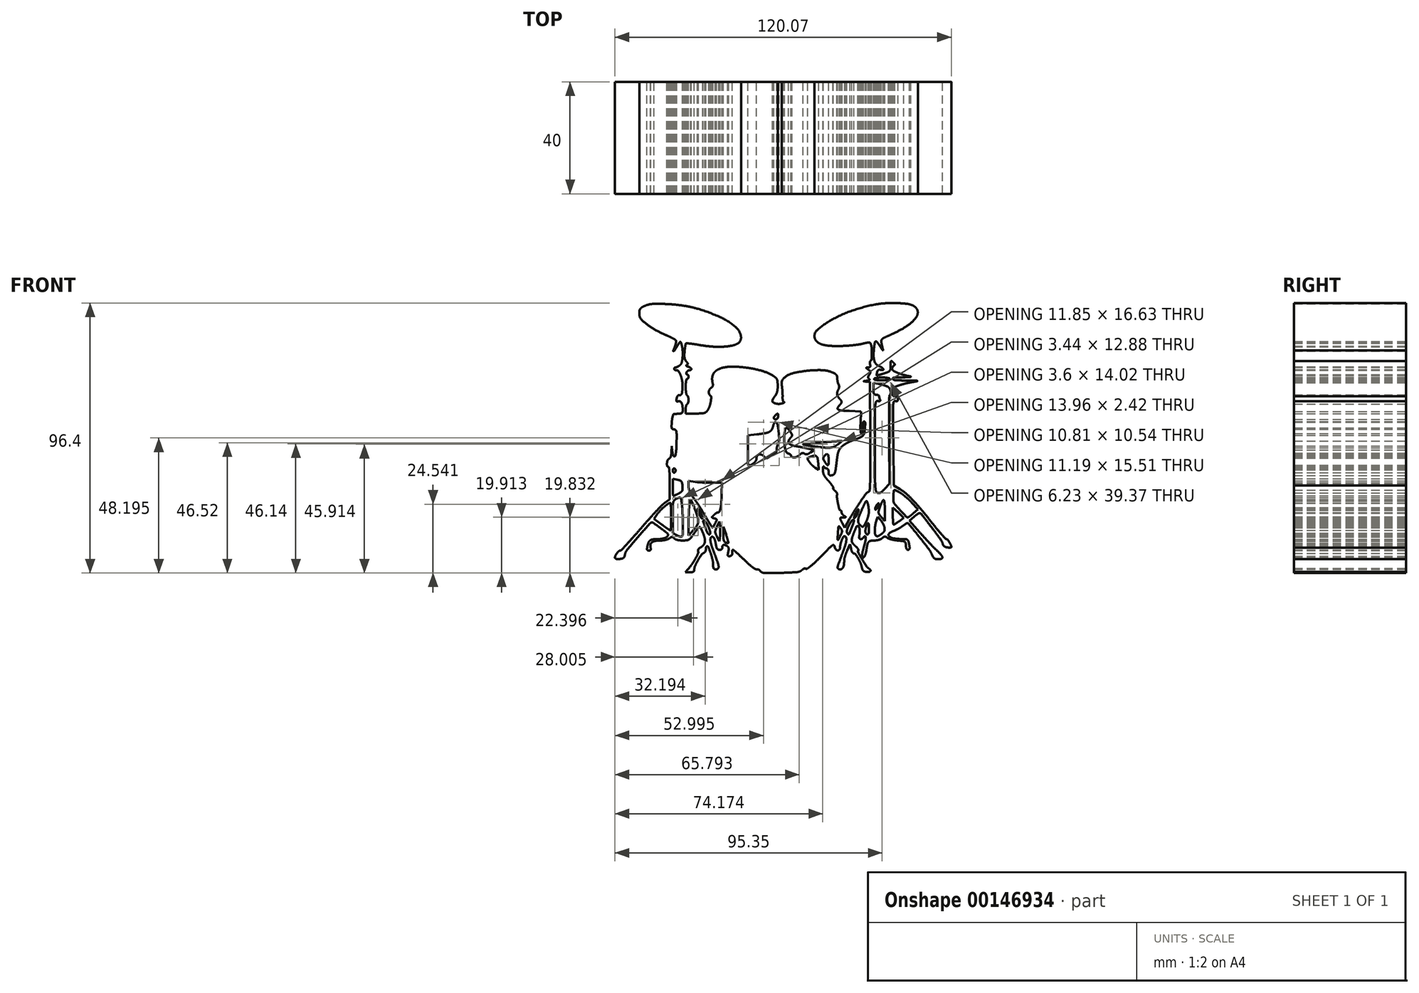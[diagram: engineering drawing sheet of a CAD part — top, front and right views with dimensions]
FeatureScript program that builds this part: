
annotation { "Feature Type Name" : "Feature", "Feature Type Description" : "" }
export const myFeature = defineFeature(function(context is Context, id is Id, definition is map)
    precondition{}
    {
        {
            var Q0;
            Q0=qCreatedBy(makeId("Front.planeOp"),FACE);
            var sketch = newSketch(context, id + "F0", { "sketchPlane" : qUnion([Q0])});
            skArc(sketch, "E0", {"start": v(19.1, 46.98) * mm, "mid": v(14.95, 46.03) * mm, "end": v(10.88, 44.78) * mm});
            skArc(sketch, "E1", {"start": v(10.88, 44.78) * mm, "mid": v(7.16, 43.3) * mm, "end": v(3.58, 41.49) * mm});
            skArc(sketch, "E2", {"start": v(3.58, 41.49) * mm, "mid": v(0.93, 39.82) * mm, "end": v(-1.54, 37.89) * mm});
            skArc(sketch, "E3", {"start": v(-1.54, 37.89) * mm, "mid": v(-2.4, 36.52) * mm, "end": v(-2.38, 34.9) * mm});
            skArc(sketch, "E4", {"start": v(-2.38, 34.9) * mm, "mid": v(-2.03, 34.18) * mm, "end": v(-1.5, 33.6) * mm});
            skArc(sketch, "E5", {"start": v(-1.5, 33.6) * mm, "mid": v(-0.72, 33.08) * mm, "end": v(0.13, 32.72) * mm});
            skArc(sketch, "E6", {"start": v(0.13, 32.72) * mm, "mid": v(1.39, 32.41) * mm, "end": v(2.67, 32.25) * mm});
            skArc(sketch, "E7", {"start": v(2.67, 32.25) * mm, "mid": v(4.53, 32.16) * mm, "end": v(6.4, 32.15) * mm});
            skArc(sketch, "E8", {"start": v(6.4, 32.15) * mm, "mid": v(7.5, 32.17) * mm, "end": v(8.58, 32.22) * mm});
            skArc(sketch, "E9", {"start": v(8.58, 32.22) * mm, "mid": v(9.74, 32.3) * mm, "end": v(10.9, 32.4) * mm});
            skArc(sketch, "E10", {"start": v(10.9, 32.4) * mm, "mid": v(11.95, 32.52) * mm, "end": v(13, 32.65) * mm});
            skArc(sketch, "E11", {"start": v(13, 32.65) * mm, "mid": v(13.74, 32.78) * mm, "end": v(14.47, 32.94) * mm});
            skArc(sketch, "E12", {"start": v(14.47, 32.94) * mm, "mid": v(15.4, 33.16) * mm, "end": v(16.35, 33.37) * mm});
            skArc(sketch, "E13", {"start": v(16.35, 33.37) * mm, "mid": v(16.7, 33.42) * mm, "end": v(17.04, 33.41) * mm});
            skArc(sketch, "E14", {"start": v(17.04, 33.41) * mm, "mid": v(17.25, 33.34) * mm, "end": v(17.42, 33.18) * mm});
            skArc(sketch, "E15", {"start": v(17.42, 33.18) * mm, "mid": v(17.58, 32.89) * mm, "end": v(17.69, 32.57) * mm});
            skArc(sketch, "E16", {"start": v(17.69, 32.57) * mm, "mid": v(17.85, 31.84) * mm, "end": v(17.93, 31.1) * mm});
            skArc(sketch, "E17", {"start": v(17.93, 31.1) * mm, "mid": v(17.98, 30.16) * mm, "end": v(17.97, 29.2) * mm});
            skArc(sketch, "E18", {"start": v(17.97, 29.2) * mm, "mid": v(17.93, 28.31) * mm, "end": v(17.86, 27.42) * mm});
            skArc(sketch, "E19", {"start": v(17.86, 27.42) * mm, "mid": v(17.76, 27.11) * mm, "end": v(17.53, 26.88) * mm});
            skArc(sketch, "E20", {"start": v(17.53, 26.88) * mm, "mid": v(17.43, 26.8) * mm, "end": v(17.37, 26.7) * mm});
            skArc(sketch, "E21", {"start": v(17.37, 26.7) * mm, "mid": v(17.31, 26.54) * mm, "end": v(17.27, 26.38) * mm});
            skArc(sketch, "E22", {"start": v(17.27, 26.38) * mm, "mid": v(17.26, 26.18) * mm, "end": v(17.26, 25.98) * mm});
            skArc(sketch, "E23", {"start": v(17.26, 25.98) * mm, "mid": v(17.28, 25.77) * mm, "end": v(17.33, 25.56) * mm});
            skArc(sketch, "E24", {"start": v(17.33, 25.56) * mm, "mid": v(17.38, 25.32) * mm, "end": v(17.4, 25.08) * mm});
            skArc(sketch, "E25", {"start": v(17.4, 25.08) * mm, "mid": v(17.39, 24.91) * mm, "end": v(17.32, 24.76) * mm});
            skArc(sketch, "E26", {"start": v(17.32, 24.76) * mm, "mid": v(17.21, 24.65) * mm, "end": v(17.07, 24.58) * mm});
            skArc(sketch, "E27", {"start": v(17.07, 24.58) * mm, "mid": v(16.86, 24.54) * mm, "end": v(16.64, 24.52) * mm});
            skArc(sketch, "E28", {"start": v(16.64, 24.52) * mm, "mid": v(16.34, 24.5) * mm, "end": v(16.04, 24.5) * mm});
            skArc(sketch, "E29", {"start": v(16.04, 24.5) * mm, "mid": v(15.98, 24.46) * mm, "end": v(15.96, 24.4) * mm});
            skArc(sketch, "E30", {"start": v(15.96, 24.4) * mm, "mid": v(15.98, 24.3) * mm, "end": v(16.04, 24.23) * mm});
            skArc(sketch, "E31", {"start": v(16.04, 24.23) * mm, "mid": v(16.36, 23.98) * mm, "end": v(16.7, 23.73) * mm});
            skArc(sketch, "E32", {"start": v(16.7, 23.73) * mm, "mid": v(16.97, 23.5) * mm, "end": v(17.22, 23.27) * mm});
            skArc(sketch, "E33", {"start": v(17.22, 23.27) * mm, "mid": v(17.35, 23.1) * mm, "end": v(17.41, 22.9) * mm});
            skArc(sketch, "E34", {"start": v(17.41, 22.9) * mm, "mid": v(17.42, 22.7) * mm, "end": v(17.36, 22.5) * mm});
            skArc(sketch, "E35", {"start": v(17.36, 22.5) * mm, "mid": v(17.2, 22.18) * mm, "end": v(17.03, 21.88) * mm});
            skArc(sketch, "E36", {"start": v(17.03, 21.88) * mm, "mid": v(16.86, 21.59) * mm, "end": v(16.7, 21.3) * mm});
            skArc(sketch, "E37", {"start": v(16.7, 21.3) * mm, "mid": v(16.64, 21.12) * mm, "end": v(16.62, 20.92) * mm});
            skArc(sketch, "E38", {"start": v(16.62, 20.92) * mm, "mid": v(16.64, 20.77) * mm, "end": v(16.71, 20.64) * mm});
            skArc(sketch, "E39", {"start": v(16.71, 20.64) * mm, "mid": v(16.85, 20.5) * mm, "end": v(17, 20.38) * mm});
            skArc(sketch, "E40", {"start": v(17, 20.38) * mm, "mid": v(17.1, 20.3) * mm, "end": v(17.16, 20.2) * mm});
            skArc(sketch, "E41", {"start": v(17.16, 20.2) * mm, "mid": v(17.16, 20.1) * mm, "end": v(17.1, 20.03) * mm});
            skArc(sketch, "E42", {"start": v(17.1, 20.03) * mm, "mid": v(16.96, 19.94) * mm, "end": v(16.79, 19.88) * mm});
            skArc(sketch, "E43", {"start": v(16.79, 19.88) * mm, "mid": v(16.47, 19.81) * mm, "end": v(16.15, 19.76) * mm});
            skArc(sketch, "E44", {"start": v(16.15, 19.76) * mm, "mid": v(15.63, 19.68) * mm, "end": v(15.11, 19.6) * mm});
            skArc(sketch, "E45", {"start": v(15.11, 19.6) * mm, "mid": v(15.07, 19.59) * mm, "end": v(15.04, 19.56) * mm});
            skArc(sketch, "E46", {"start": v(15.04, 19.56) * mm, "mid": v(15.04, 19.53) * mm, "end": v(15.07, 19.51) * mm});
            skArc(sketch, "E47", {"start": v(15.07, 19.51) * mm, "mid": v(15.53, 19.48) * mm, "end": v(16, 19.46) * mm});
            skLineSegment(sketch, "E48", {"start": v(16, 19.46) * mm, "end": v(17.34, 19.38) * mm});
            skLineSegment(sketch, "E49", {"start": v(17.34, 19.38) * mm, "end": v(17.43, -0.14) * mm});
            skArc(sketch, "E50", {"start": v(17.43, -0.14) * mm, "mid": v(17.45, -5.6) * mm, "end": v(17.46, -11.04) * mm});
            skArc(sketch, "E51", {"start": v(17.46, -11.04) * mm, "mid": v(17.44, -13.63) * mm, "end": v(17.37, -16.22) * mm});
            skArc(sketch, "E52", {"start": v(17.37, -16.22) * mm, "mid": v(17.3, -17.8) * mm, "end": v(17.2, -19.36) * mm});
            skArc(sketch, "E53", {"start": v(17.2, -19.36) * mm, "mid": v(17.07, -19.72) * mm, "end": v(16.77, -19.95) * mm});
            skArc(sketch, "E54", {"start": v(16.77, -19.95) * mm, "mid": v(16.29, -20.22) * mm, "end": v(15.9, -20.6) * mm});
            skArc(sketch, "E55", {"start": v(15.9, -20.6) * mm, "mid": v(14.97, -21.86) * mm, "end": v(14.07, -23.13) * mm});
            skArc(sketch, "E56", {"start": v(14.07, -23.13) * mm, "mid": v(13.04, -24.65) * mm, "end": v(12.06, -26.2) * mm});
            skArc(sketch, "E57", {"start": v(12.06, -26.2) * mm, "mid": v(11.07, -27.86) * mm, "end": v(10.11, -29.54) * mm});
            skLineSegment(sketch, "E58", {"start": v(10.11, -29.54) * mm, "end": v(8.3, -32.8) * mm});
            skLineSegment(sketch, "E59", {"start": v(8.3, -32.8) * mm, "end": v(7.47, -31.22) * mm});
            skArc(sketch, "E60", {"start": v(7.47, -31.22) * mm, "mid": v(7.13, -30.54) * mm, "end": v(6.8, -29.86) * mm});
            skArc(sketch, "E61", {"start": v(6.8, -29.86) * mm, "mid": v(6.73, -29.62) * mm, "end": v(6.73, -29.38) * mm});
            skArc(sketch, "E62", {"start": v(6.73, -29.38) * mm, "mid": v(6.81, -29.21) * mm, "end": v(6.98, -29.13) * mm});
            skArc(sketch, "E63", {"start": v(6.98, -29.13) * mm, "mid": v(7.4, -29.07) * mm, "end": v(7.81, -29.05) * mm});
            skArc(sketch, "E64", {"start": v(7.81, -29.05) * mm, "mid": v(8.16, -29.04) * mm, "end": v(8.51, -29.03) * mm});
            skArc(sketch, "E65", {"start": v(8.51, -29.03) * mm, "mid": v(8.58, -29) * mm, "end": v(8.63, -28.95) * mm});
            skArc(sketch, "E66", {"start": v(8.63, -28.95) * mm, "mid": v(8.64, -28.89) * mm, "end": v(8.6, -28.83) * mm});
            skArc(sketch, "E67", {"start": v(8.6, -28.83) * mm, "mid": v(8.34, -28.67) * mm, "end": v(8.07, -28.51) * mm});
            skArc(sketch, "E68", {"start": v(8.07, -28.51) * mm, "mid": v(7.9, -28.4) * mm, "end": v(7.73, -28.25) * mm});
            skArc(sketch, "E69", {"start": v(7.73, -28.25) * mm, "mid": v(7.57, -28.1) * mm, "end": v(7.43, -27.92) * mm});
            skArc(sketch, "E70", {"start": v(7.43, -27.92) * mm, "mid": v(7.32, -27.75) * mm, "end": v(7.23, -27.56) * mm});
            skArc(sketch, "E71", {"start": v(7.23, -27.56) * mm, "mid": v(7.19, -27.4) * mm, "end": v(7.17, -27.24) * mm});
            skArc(sketch, "E72", {"start": v(7.17, -27.24) * mm, "mid": v(7.16, -27.1) * mm, "end": v(7.14, -26.95) * mm});
            skArc(sketch, "E73", {"start": v(7.14, -26.95) * mm, "mid": v(7.1, -26.83) * mm, "end": v(7.03, -26.71) * mm});
            skArc(sketch, "E74", {"start": v(7.03, -26.71) * mm, "mid": v(6.97, -26.62) * mm, "end": v(6.89, -26.55) * mm});
            skArc(sketch, "E75", {"start": v(6.89, -26.55) * mm, "mid": v(6.8, -26.5) * mm, "end": v(6.71, -26.5) * mm});
            skArc(sketch, "E76", {"start": v(6.71, -26.5) * mm, "mid": v(6.48, -26.41) * mm, "end": v(6.34, -26.2) * mm});
            skArc(sketch, "E77", {"start": v(6.34, -26.2) * mm, "mid": v(6.1, -25.18) * mm, "end": v(5.88, -24.16) * mm});
            skArc(sketch, "E78", {"start": v(5.88, -24.16) * mm, "mid": v(5.7, -23.15) * mm, "end": v(5.54, -22.13) * mm});
            skArc(sketch, "E79", {"start": v(5.54, -22.13) * mm, "mid": v(5.5, -21.51) * mm, "end": v(5.57, -20.9) * mm});
            skArc(sketch, "E80", {"start": v(5.57, -20.9) * mm, "mid": v(5.58, -20.75) * mm, "end": v(5.55, -20.6) * mm});
            skArc(sketch, "E81", {"start": v(5.55, -20.6) * mm, "mid": v(5.5, -20.4) * mm, "end": v(5.4, -20.23) * mm});
            skArc(sketch, "E82", {"start": v(5.4, -20.23) * mm, "mid": v(5.3, -20.05) * mm, "end": v(5.16, -19.88) * mm});
            skArc(sketch, "E83", {"start": v(5.16, -19.88) * mm, "mid": v(5.01, -19.73) * mm, "end": v(4.85, -19.6) * mm});
            skArc(sketch, "E84", {"start": v(4.85, -19.6) * mm, "mid": v(4.69, -19.46) * mm, "end": v(4.54, -19.32) * mm});
            skArc(sketch, "E85", {"start": v(4.54, -19.32) * mm, "mid": v(4.4, -19.17) * mm, "end": v(4.3, -19.01) * mm});
            skArc(sketch, "E86", {"start": v(4.3, -19.01) * mm, "mid": v(4.22, -18.87) * mm, "end": v(4.16, -18.72) * mm});
            skArc(sketch, "E87", {"start": v(4.16, -18.72) * mm, "mid": v(4.14, -18.6) * mm, "end": v(4.16, -18.48) * mm});
            skArc(sketch, "E88", {"start": v(4.16, -18.48) * mm, "mid": v(4.17, -18.33) * mm, "end": v(4.12, -18.19) * mm});
            skArc(sketch, "E89", {"start": v(4.12, -18.19) * mm, "mid": v(3.92, -17.85) * mm, "end": v(3.7, -17.53) * mm});
            skArc(sketch, "E90", {"start": v(3.7, -17.53) * mm, "mid": v(3.41, -17.13) * mm, "end": v(3.11, -16.75) * mm});
            skArc(sketch, "E91", {"start": v(3.11, -16.75) * mm, "mid": v(2.76, -16.33) * mm, "end": v(2.4, -15.92) * mm});
            skArc(sketch, "E92", {"start": v(2.4, -15.92) * mm, "mid": v(1.9, -15.38) * mm, "end": v(1.45, -14.82) * mm});
            skArc(sketch, "E93", {"start": v(1.45, -14.82) * mm, "mid": v(1.14, -14.38) * mm, "end": v(0.88, -13.92) * mm});
            skArc(sketch, "E94", {"start": v(0.88, -13.92) * mm, "mid": v(0.7, -13.5) * mm, "end": v(0.6, -13.05) * mm});
            skArc(sketch, "E95", {"start": v(0.6, -13.05) * mm, "mid": v(0.53, -12.56) * mm, "end": v(0.51, -12.06) * mm});
            skArc(sketch, "E96", {"start": v(0.51, -12.06) * mm, "mid": v(0.52, -11.73) * mm, "end": v(0.54, -11.4) * mm});
            skArc(sketch, "E97", {"start": v(0.54, -11.4) * mm, "mid": v(0.57, -11.19) * mm, "end": v(0.62, -10.97) * mm});
            skArc(sketch, "E98", {"start": v(0.62, -10.97) * mm, "mid": v(0.65, -10.9) * mm, "end": v(0.71, -10.86) * mm});
            skArc(sketch, "E99", {"start": v(0.71, -10.86) * mm, "mid": v(0.77, -10.86) * mm, "end": v(0.81, -10.9) * mm});
            skArc(sketch, "E100", {"start": v(0.81, -10.9) * mm, "mid": v(0.88, -11.03) * mm, "end": v(0.96, -11.15) * mm});
            skArc(sketch, "E101", {"start": v(0.96, -11.15) * mm, "mid": v(1.08, -11.26) * mm, "end": v(1.2, -11.35) * mm});
            skArc(sketch, "E102", {"start": v(1.2, -11.35) * mm, "mid": v(1.35, -11.43) * mm, "end": v(1.5, -11.5) * mm});
            skArc(sketch, "E103", {"start": v(1.5, -11.5) * mm, "mid": v(1.65, -11.53) * mm, "end": v(1.8, -11.54) * mm});
            skArc(sketch, "E104", {"start": v(1.8, -11.54) * mm, "mid": v(1.96, -11.57) * mm, "end": v(2.1, -11.64) * mm});
            skArc(sketch, "E105", {"start": v(2.1, -11.64) * mm, "mid": v(2.23, -11.76) * mm, "end": v(2.33, -11.9) * mm});
            skArc(sketch, "E106", {"start": v(2.33, -11.9) * mm, "mid": v(2.42, -12.11) * mm, "end": v(2.48, -12.33) * mm});
            skArc(sketch, "E107", {"start": v(2.48, -12.33) * mm, "mid": v(2.52, -12.6) * mm, "end": v(2.53, -12.87) * mm});
            skArc(sketch, "E108", {"start": v(2.53, -12.87) * mm, "mid": v(2.54, -13.21) * mm, "end": v(2.58, -13.55) * mm});
            skArc(sketch, "E109", {"start": v(2.58, -13.55) * mm, "mid": v(2.64, -13.74) * mm, "end": v(2.76, -13.9) * mm});
            skArc(sketch, "E110", {"start": v(2.76, -13.9) * mm, "mid": v(2.91, -14) * mm, "end": v(3.1, -14.05) * mm});
            skArc(sketch, "E111", {"start": v(3.1, -14.05) * mm, "mid": v(3.4, -14.06) * mm, "end": v(3.7, -14.03) * mm});
            skArc(sketch, "E112", {"start": v(3.7, -14.03) * mm, "mid": v(4.03, -13.93) * mm, "end": v(4.34, -13.75) * mm});
            skArc(sketch, "E113", {"start": v(4.34, -13.75) * mm, "mid": v(4.58, -13.5) * mm, "end": v(4.75, -13.18) * mm});
            skArc(sketch, "E114", {"start": v(4.75, -13.18) * mm, "mid": v(4.92, -12.62) * mm, "end": v(5.03, -12.05) * mm});
            skArc(sketch, "E115", {"start": v(5.03, -12.05) * mm, "mid": v(5.2, -10.75) * mm, "end": v(5.37, -9.44) * mm});
            skArc(sketch, "E116", {"start": v(5.37, -9.44) * mm, "mid": v(5.52, -8.18) * mm, "end": v(5.7, -6.93) * mm});
            skArc(sketch, "E117", {"start": v(5.7, -6.93) * mm, "mid": v(5.84, -6.23) * mm, "end": v(6.04, -5.55) * mm});
            skArc(sketch, "E118", {"start": v(6.04, -5.55) * mm, "mid": v(6.26, -5.05) * mm, "end": v(6.54, -4.58) * mm});
            skArc(sketch, "E119", {"start": v(6.54, -4.58) * mm, "mid": v(6.92, -4.1) * mm, "end": v(7.35, -3.67) * mm});
            skArc(sketch, "E120", {"start": v(7.35, -3.67) * mm, "mid": v(7.7, -3.36) * mm, "end": v(8.1, -3.09) * mm});
            skArc(sketch, "E121", {"start": v(8.1, -3.09) * mm, "mid": v(8.62, -2.76) * mm, "end": v(9.16, -2.46) * mm});
            skArc(sketch, "E122", {"start": v(9.16, -2.46) * mm, "mid": v(9.74, -2.15) * mm, "end": v(10.34, -1.87) * mm});
            skArc(sketch, "E123", {"start": v(10.34, -1.87) * mm, "mid": v(10.9, -1.64) * mm, "end": v(11.46, -1.44) * mm});
            skArc(sketch, "E124", {"start": v(11.46, -1.44) * mm, "mid": v(12, -1.25) * mm, "end": v(12.52, -1.05) * mm});
            skArc(sketch, "E125", {"start": v(12.52, -1.05) * mm, "mid": v(13.02, -0.85) * mm, "end": v(13.52, -0.63) * mm});
            skArc(sketch, "E126", {"start": v(13.52, -0.63) * mm, "mid": v(13.94, -0.42) * mm, "end": v(14.35, -0.21) * mm});
            skArc(sketch, "E127", {"start": v(14.35, -0.21) * mm, "mid": v(14.56, -0.07) * mm, "end": v(14.76, 0.1) * mm});
            skArc(sketch, "E128", {"start": v(14.76, 0.1) * mm, "mid": v(15.08, 0.53) * mm, "end": v(15.27, 1.04) * mm});
            skArc(sketch, "E129", {"start": v(15.27, 1.04) * mm, "mid": v(15.43, 2) * mm, "end": v(15.53, 2.95) * mm});
            skArc(sketch, "E130", {"start": v(15.53, 2.95) * mm, "mid": v(15.58, 3.87) * mm, "end": v(15.58, 4.8) * mm});
            skArc(sketch, "E131", {"start": v(15.58, 4.8) * mm, "mid": v(15.45, 5.09) * mm, "end": v(15.16, 5.2) * mm});
            skArc(sketch, "E132", {"start": v(15.16, 5.2) * mm, "mid": v(15.04, 5.17) * mm, "end": v(14.97, 5.07) * mm});
            skArc(sketch, "E133", {"start": v(14.97, 5.07) * mm, "mid": v(14.89, 4.82) * mm, "end": v(14.83, 4.56) * mm});
            skArc(sketch, "E134", {"start": v(14.83, 4.56) * mm, "mid": v(14.78, 4.21) * mm, "end": v(14.76, 3.86) * mm});
            skArc(sketch, "E135", {"start": v(14.76, 3.86) * mm, "mid": v(14.75, 3.44) * mm, "end": v(14.77, 3.02) * mm});
            skArc(sketch, "E136", {"start": v(14.77, 3.02) * mm, "mid": v(14.78, 2.57) * mm, "end": v(14.78, 2.13) * mm});
            skArc(sketch, "E137", {"start": v(14.78, 2.13) * mm, "mid": v(14.76, 1.78) * mm, "end": v(14.7, 1.43) * mm});
            skArc(sketch, "E138", {"start": v(14.7, 1.43) * mm, "mid": v(14.64, 1.2) * mm, "end": v(14.55, 0.97) * mm});
            skArc(sketch, "E139", {"start": v(14.55, 0.97) * mm, "mid": v(14.47, 0.86) * mm, "end": v(14.34, 0.83) * mm});
            skArc(sketch, "E140", {"start": v(14.34, 0.83) * mm, "mid": v(14.18, 0.88) * mm, "end": v(14.1, 1.02) * mm});
            skArc(sketch, "E141", {"start": v(14.1, 1.02) * mm, "mid": v(14.02, 1.43) * mm, "end": v(13.96, 1.84) * mm});
            skArc(sketch, "E142", {"start": v(13.96, 1.84) * mm, "mid": v(13.92, 2.46) * mm, "end": v(13.9, 3.07) * mm});
            skArc(sketch, "E143", {"start": v(13.9, 3.07) * mm, "mid": v(13.92, 3.95) * mm, "end": v(13.95, 4.82) * mm});
            skLineSegment(sketch, "E144", {"start": v(13.95, 4.82) * mm, "end": v(14.11, 8.81) * mm});
            skLineSegment(sketch, "E145", {"start": v(14.11, 8.81) * mm, "end": v(9.87, 8.96) * mm});
            skArc(sketch, "E146", {"start": v(9.87, 8.96) * mm, "mid": v(8.47, 9.03) * mm, "end": v(7.08, 9.12) * mm});
            skArc(sketch, "E147", {"start": v(7.08, 9.12) * mm, "mid": v(6.5, 9.23) * mm, "end": v(5.97, 9.46) * mm});
            skArc(sketch, "E148", {"start": v(5.97, 9.46) * mm, "mid": v(5.76, 9.72) * mm, "end": v(5.78, 10.04) * mm});
            skArc(sketch, "E149", {"start": v(5.78, 10.04) * mm, "mid": v(6.04, 10.53) * mm, "end": v(6.4, 10.95) * mm});
            skArc(sketch, "E150", {"start": v(6.4, 10.95) * mm, "mid": v(6.69, 11.27) * mm, "end": v(6.95, 11.62) * mm});
            skArc(sketch, "E151", {"start": v(6.95, 11.62) * mm, "mid": v(7.08, 11.87) * mm, "end": v(7.13, 12.16) * mm});
            skArc(sketch, "E152", {"start": v(7.13, 12.16) * mm, "mid": v(7.09, 12.44) * mm, "end": v(6.97, 12.7) * mm});
            skArc(sketch, "E153", {"start": v(6.97, 12.7) * mm, "mid": v(6.72, 13.03) * mm, "end": v(6.44, 13.34) * mm});
            skArc(sketch, "E154", {"start": v(6.44, 13.34) * mm, "mid": v(6.12, 13.7) * mm, "end": v(5.85, 14.1) * mm});
            skArc(sketch, "E155", {"start": v(5.85, 14.1) * mm, "mid": v(5.67, 14.47) * mm, "end": v(5.58, 14.86) * mm});
            skArc(sketch, "E156", {"start": v(5.58, 14.86) * mm, "mid": v(5.56, 15.27) * mm, "end": v(5.63, 15.68) * mm});
            skArc(sketch, "E157", {"start": v(5.63, 15.68) * mm, "mid": v(5.78, 16.14) * mm, "end": v(6, 16.57) * mm});
            skArc(sketch, "E158", {"start": v(6, 16.57) * mm, "mid": v(6.11, 16.81) * mm, "end": v(6.2, 17.07) * mm});
            skArc(sketch, "E159", {"start": v(6.2, 17.07) * mm, "mid": v(6.27, 17.3) * mm, "end": v(6.3, 17.55) * mm});
            skArc(sketch, "E160", {"start": v(6.3, 17.55) * mm, "mid": v(6.3, 17.77) * mm, "end": v(6.27, 18) * mm});
            skArc(sketch, "E161", {"start": v(6.27, 18) * mm, "mid": v(6.2, 18.2) * mm, "end": v(6.11, 18.38) * mm});
            skArc(sketch, "E162", {"start": v(6.11, 18.38) * mm, "mid": v(6, 18.56) * mm, "end": v(5.93, 18.76) * mm});
            skArc(sketch, "E163", {"start": v(5.93, 18.76) * mm, "mid": v(5.84, 19.04) * mm, "end": v(5.77, 19.33) * mm});
            skArc(sketch, "E164", {"start": v(5.77, 19.33) * mm, "mid": v(5.71, 19.64) * mm, "end": v(5.67, 19.96) * mm});
            skArc(sketch, "E165", {"start": v(5.67, 19.96) * mm, "mid": v(5.64, 20.26) * mm, "end": v(5.63, 20.57) * mm});
            skArc(sketch, "E166", {"start": v(5.63, 20.57) * mm, "mid": v(5.6, 20.95) * mm, "end": v(5.54, 21.33) * mm});
            skArc(sketch, "E167", {"start": v(5.54, 21.33) * mm, "mid": v(5.43, 21.61) * mm, "end": v(5.27, 21.87) * mm});
            skArc(sketch, "E168", {"start": v(5.27, 21.87) * mm, "mid": v(5.03, 22.11) * mm, "end": v(4.75, 22.31) * mm});
            skArc(sketch, "E169", {"start": v(4.75, 22.31) * mm, "mid": v(4.3, 22.55) * mm, "end": v(3.84, 22.76) * mm});
            skArc(sketch, "E170", {"start": v(3.84, 22.76) * mm, "mid": v(2.03, 23.32) * mm, "end": v(0.14, 23.54) * mm});
            skArc(sketch, "E171", {"start": v(0.14, 23.54) * mm, "mid": v(-2.56, 23.51) * mm, "end": v(-5.25, 23.3) * mm});
            skArc(sketch, "E172", {"start": v(-5.25, 23.3) * mm, "mid": v(-7.87, 22.93) * mm, "end": v(-10.45, 22.38) * mm});
            skArc(sketch, "E173", {"start": v(-10.45, 22.38) * mm, "mid": v(-11.96, 21.8) * mm, "end": v(-13.27, 20.85) * mm});
            skArc(sketch, "E174", {"start": v(-13.27, 20.85) * mm, "mid": v(-13.57, 20.54) * mm, "end": v(-13.83, 20.2) * mm});
            skArc(sketch, "E175", {"start": v(-13.83, 20.2) * mm, "mid": v(-14, 19.9) * mm, "end": v(-14.13, 19.58) * mm});
            skArc(sketch, "E176", {"start": v(-14.13, 19.58) * mm, "mid": v(-14.2, 19.2) * mm, "end": v(-14.21, 18.8) * mm});
            skArc(sketch, "E177", {"start": v(-14.21, 18.8) * mm, "mid": v(-14.18, 18.23) * mm, "end": v(-14.12, 17.65) * mm});
            skArc(sketch, "E178", {"start": v(-14.12, 17.65) * mm, "mid": v(-14.06, 17.18) * mm, "end": v(-14.01, 16.71) * mm});
            skArc(sketch, "E179", {"start": v(-14.01, 16.71) * mm, "mid": v(-13.97, 16.18) * mm, "end": v(-13.94, 15.65) * mm});
            skArc(sketch, "E180", {"start": v(-13.94, 15.65) * mm, "mid": v(-13.91, 15.14) * mm, "end": v(-13.9, 14.63) * mm});
            skArc(sketch, "E181", {"start": v(-13.9, 14.63) * mm, "mid": v(-13.89, 14.24) * mm, "end": v(-13.9, 13.84) * mm});
            skArc(sketch, "E182", {"start": v(-13.9, 13.84) * mm, "mid": v(-13.9, 13.5) * mm, "end": v(-13.88, 13.15) * mm});
            skArc(sketch, "E183", {"start": v(-13.88, 13.15) * mm, "mid": v(-13.84, 12.88) * mm, "end": v(-13.77, 12.61) * mm});
            skArc(sketch, "E184", {"start": v(-13.77, 12.61) * mm, "mid": v(-13.69, 12.43) * mm, "end": v(-13.58, 12.26) * mm});
            skArc(sketch, "E185", {"start": v(-13.58, 12.26) * mm, "mid": v(-13.46, 12.16) * mm, "end": v(-13.32, 12.12) * mm});
            skArc(sketch, "E186", {"start": v(-13.32, 12.12) * mm, "mid": v(-13.27, 12.1) * mm, "end": v(-13.25, 12.05) * mm});
            skArc(sketch, "E187", {"start": v(-13.25, 12.05) * mm, "mid": v(-13.26, 12) * mm, "end": v(-13.3, 11.96) * mm});
            skArc(sketch, "E188", {"start": v(-13.3, 11.96) * mm, "mid": v(-13.46, 11.87) * mm, "end": v(-13.63, 11.8) * mm});
            skArc(sketch, "E189", {"start": v(-13.63, 11.8) * mm, "mid": v(-13.9, 11.71) * mm, "end": v(-14.17, 11.63) * mm});
            skArc(sketch, "E190", {"start": v(-14.17, 11.63) * mm, "mid": v(-14.72, 11.5) * mm, "end": v(-15.3, 11.47) * mm});
            skArc(sketch, "E191", {"start": v(-15.3, 11.47) * mm, "mid": v(-15.86, 11.5) * mm, "end": v(-16.43, 11.63) * mm});
            skArc(sketch, "E192", {"start": v(-16.43, 11.63) * mm, "mid": v(-16.87, 11.8) * mm, "end": v(-17.28, 12.05) * mm});
            skArc(sketch, "E193", {"start": v(-17.28, 12.05) * mm, "mid": v(-17.5, 12.3) * mm, "end": v(-17.57, 12.63) * mm});
            skArc(sketch, "E194", {"start": v(-17.57, 12.63) * mm, "mid": v(-17.56, 12.75) * mm, "end": v(-17.51, 12.87) * mm});
            skArc(sketch, "E195", {"start": v(-17.51, 12.87) * mm, "mid": v(-17.4, 13.08) * mm, "end": v(-17.28, 13.3) * mm});
            skArc(sketch, "E196", {"start": v(-17.28, 13.3) * mm, "mid": v(-17.13, 13.55) * mm, "end": v(-16.96, 13.8) * mm});
            skArc(sketch, "E197", {"start": v(-16.96, 13.8) * mm, "mid": v(-16.78, 14.06) * mm, "end": v(-16.58, 14.3) * mm});
            skArc(sketch, "E198", {"start": v(-16.58, 14.3) * mm, "mid": v(-16.34, 14.65) * mm, "end": v(-16.15, 15.02) * mm});
            skArc(sketch, "E199", {"start": v(-16.15, 15.02) * mm, "mid": v(-15.98, 15.43) * mm, "end": v(-15.85, 15.86) * mm});
            skArc(sketch, "E200", {"start": v(-15.85, 15.86) * mm, "mid": v(-15.74, 16.35) * mm, "end": v(-15.68, 16.86) * mm});
            skArc(sketch, "E201", {"start": v(-15.68, 16.86) * mm, "mid": v(-15.64, 17.45) * mm, "end": v(-15.64, 18.04) * mm});
            skArc(sketch, "E202", {"start": v(-15.64, 18.04) * mm, "mid": v(-15.66, 18.76) * mm, "end": v(-15.71, 19.47) * mm});
            skArc(sketch, "E203", {"start": v(-15.71, 19.47) * mm, "mid": v(-15.79, 19.88) * mm, "end": v(-15.93, 20.27) * mm});
            skArc(sketch, "E204", {"start": v(-15.93, 20.27) * mm, "mid": v(-16.13, 20.6) * mm, "end": v(-16.4, 20.87) * mm});
            skArc(sketch, "E205", {"start": v(-16.4, 20.87) * mm, "mid": v(-16.82, 21.2) * mm, "end": v(-17.27, 21.5) * mm});
            skArc(sketch, "E206", {"start": v(-17.27, 21.5) * mm, "mid": v(-19.31, 22.58) * mm, "end": v(-21.5, 23.35) * mm});
            skArc(sketch, "E207", {"start": v(-21.5, 23.35) * mm, "mid": v(-24.3, 24.01) * mm, "end": v(-27.16, 24.47) * mm});
            skArc(sketch, "E208", {"start": v(-27.16, 24.47) * mm, "mid": v(-29.96, 24.71) * mm, "end": v(-32.77, 24.75) * mm});
            skArc(sketch, "E209", {"start": v(-32.77, 24.75) * mm, "mid": v(-34.77, 24.5) * mm, "end": v(-36.7, 23.9) * mm});
            skArc(sketch, "E210", {"start": v(-36.7, 23.9) * mm, "mid": v(-37.35, 23.55) * mm, "end": v(-37.94, 23.09) * mm});
            skArc(sketch, "E211", {"start": v(-37.94, 23.09) * mm, "mid": v(-38.4, 22.56) * mm, "end": v(-38.74, 21.94) * mm});
            skArc(sketch, "E212", {"start": v(-38.74, 21.94) * mm, "mid": v(-38.97, 21.25) * mm, "end": v(-39.05, 20.52) * mm});
            skArc(sketch, "E213", {"start": v(-39.05, 20.52) * mm, "mid": v(-39, 19.69) * mm, "end": v(-38.85, 18.88) * mm});
            skArc(sketch, "E214", {"start": v(-38.85, 18.88) * mm, "mid": v(-38.8, 18.6) * mm, "end": v(-38.77, 18.33) * mm});
            skArc(sketch, "E215", {"start": v(-38.77, 18.33) * mm, "mid": v(-38.78, 18.1) * mm, "end": v(-38.83, 17.88) * mm});
            skArc(sketch, "E216", {"start": v(-38.83, 17.88) * mm, "mid": v(-38.92, 17.68) * mm, "end": v(-39.04, 17.51) * mm});
            skArc(sketch, "E217", {"start": v(-39.04, 17.51) * mm, "mid": v(-39.2, 17.35) * mm, "end": v(-39.4, 17.23) * mm});
            skArc(sketch, "E218", {"start": v(-39.4, 17.23) * mm, "mid": v(-39.71, 16.99) * mm, "end": v(-39.95, 16.68) * mm});
            skArc(sketch, "E219", {"start": v(-39.95, 16.68) * mm, "mid": v(-40.13, 16.27) * mm, "end": v(-40.22, 15.84) * mm});
            skArc(sketch, "E220", {"start": v(-40.22, 15.84) * mm, "mid": v(-40.22, 15.43) * mm, "end": v(-40.14, 15.02) * mm});
            skArc(sketch, "E221", {"start": v(-40.14, 15.02) * mm, "mid": v(-39.98, 14.7) * mm, "end": v(-39.72, 14.47) * mm});
            skArc(sketch, "E222", {"start": v(-39.72, 14.47) * mm, "mid": v(-39.46, 14.2) * mm, "end": v(-39.38, 13.85) * mm});
            skArc(sketch, "E223", {"start": v(-39.38, 13.85) * mm, "mid": v(-39.44, 13.05) * mm, "end": v(-39.55, 12.27) * mm});
            skArc(sketch, "E224", {"start": v(-39.55, 12.27) * mm, "mid": v(-39.73, 11.4) * mm, "end": v(-39.98, 10.55) * mm});
            skArc(sketch, "E225", {"start": v(-39.98, 10.55) * mm, "mid": v(-40.27, 9.86) * mm, "end": v(-40.64, 9.2) * mm});
            skArc(sketch, "E226", {"start": v(-40.64, 9.2) * mm, "mid": v(-40.9, 8.87) * mm, "end": v(-41.2, 8.58) * mm});
            skArc(sketch, "E227", {"start": v(-41.2, 8.58) * mm, "mid": v(-41.52, 8.38) * mm, "end": v(-41.88, 8.24) * mm});
            skArc(sketch, "E228", {"start": v(-41.88, 8.24) * mm, "mid": v(-42.4, 8.13) * mm, "end": v(-42.92, 8.08) * mm});
            skArc(sketch, "E229", {"start": v(-42.92, 8.08) * mm, "mid": v(-43.94, 8.05) * mm, "end": v(-44.95, 8.04) * mm});
            skLineSegment(sketch, "E230", {"start": v(-44.95, 8.04) * mm, "end": v(-48.5, 8.04) * mm});
            skLineSegment(sketch, "E231", {"start": v(-48.5, 8.04) * mm, "end": v(-48.5, 9.56) * mm});
            skArc(sketch, "E232", {"start": v(-48.5, 9.56) * mm, "mid": v(-48.48, 9.86) * mm, "end": v(-48.46, 10.16) * mm});
            skArc(sketch, "E233", {"start": v(-48.46, 10.16) * mm, "mid": v(-48.41, 10.44) * mm, "end": v(-48.34, 10.72) * mm});
            skArc(sketch, "E234", {"start": v(-48.34, 10.72) * mm, "mid": v(-48.27, 10.95) * mm, "end": v(-48.18, 11.17) * mm});
            skArc(sketch, "E235", {"start": v(-48.18, 11.17) * mm, "mid": v(-48.1, 11.3) * mm, "end": v(-47.98, 11.4) * mm});
            skArc(sketch, "E236", {"start": v(-47.98, 11.4) * mm, "mid": v(-47.87, 11.48) * mm, "end": v(-47.78, 11.6) * mm});
            skArc(sketch, "E237", {"start": v(-47.78, 11.6) * mm, "mid": v(-47.69, 11.78) * mm, "end": v(-47.61, 11.98) * mm});
            skArc(sketch, "E238", {"start": v(-47.61, 11.98) * mm, "mid": v(-47.55, 12.2) * mm, "end": v(-47.5, 12.44) * mm});
            skArc(sketch, "E239", {"start": v(-47.5, 12.44) * mm, "mid": v(-47.47, 12.7) * mm, "end": v(-47.46, 12.94) * mm});
            skArc(sketch, "E240", {"start": v(-47.46, 12.94) * mm, "mid": v(-47.47, 13.18) * mm, "end": v(-47.5, 13.43) * mm});
            skArc(sketch, "E241", {"start": v(-47.5, 13.43) * mm, "mid": v(-47.55, 13.67) * mm, "end": v(-47.61, 13.9) * mm});
            skArc(sketch, "E242", {"start": v(-47.61, 13.9) * mm, "mid": v(-47.69, 14.1) * mm, "end": v(-47.78, 14.28) * mm});
            skArc(sketch, "E243", {"start": v(-47.78, 14.28) * mm, "mid": v(-47.87, 14.4) * mm, "end": v(-47.98, 14.48) * mm});
            skArc(sketch, "E244", {"start": v(-47.98, 14.48) * mm, "mid": v(-48.1, 14.6) * mm, "end": v(-48.18, 14.76) * mm});
            skArc(sketch, "E245", {"start": v(-48.18, 14.76) * mm, "mid": v(-48.27, 15.14) * mm, "end": v(-48.34, 15.53) * mm});
            skArc(sketch, "E246", {"start": v(-48.34, 15.53) * mm, "mid": v(-48.41, 16.02) * mm, "end": v(-48.46, 16.5) * mm});
            skArc(sketch, "E247", {"start": v(-48.46, 16.5) * mm, "mid": v(-48.49, 17.06) * mm, "end": v(-48.5, 17.6) * mm});
            skArc(sketch, "E248", {"start": v(-48.5, 17.6) * mm, "mid": v(-48.49, 18.14) * mm, "end": v(-48.46, 18.68) * mm});
            skArc(sketch, "E249", {"start": v(-48.46, 18.68) * mm, "mid": v(-48.41, 19.14) * mm, "end": v(-48.34, 19.59) * mm});
            skArc(sketch, "E250", {"start": v(-48.34, 19.59) * mm, "mid": v(-48.27, 19.93) * mm, "end": v(-48.18, 20.26) * mm});
            skArc(sketch, "E251", {"start": v(-48.18, 20.26) * mm, "mid": v(-48.1, 20.37) * mm, "end": v(-47.98, 20.41) * mm});
            skArc(sketch, "E252", {"start": v(-47.98, 20.41) * mm, "mid": v(-47.88, 20.43) * mm, "end": v(-47.78, 20.47) * mm});
            skArc(sketch, "E253", {"start": v(-47.78, 20.47) * mm, "mid": v(-47.7, 20.55) * mm, "end": v(-47.61, 20.64) * mm});
            skArc(sketch, "E254", {"start": v(-47.61, 20.64) * mm, "mid": v(-47.55, 20.76) * mm, "end": v(-47.5, 20.89) * mm});
            skArc(sketch, "E255", {"start": v(-47.5, 20.89) * mm, "mid": v(-47.47, 21.03) * mm, "end": v(-47.46, 21.18) * mm});
            skArc(sketch, "E256", {"start": v(-47.46, 21.18) * mm, "mid": v(-47.47, 21.33) * mm, "end": v(-47.5, 21.48) * mm});
            skArc(sketch, "E257", {"start": v(-47.5, 21.48) * mm, "mid": v(-47.55, 21.6) * mm, "end": v(-47.61, 21.73) * mm});
            skArc(sketch, "E258", {"start": v(-47.61, 21.73) * mm, "mid": v(-47.68, 21.82) * mm, "end": v(-47.77, 21.9) * mm});
            skArc(sketch, "E259", {"start": v(-47.77, 21.9) * mm, "mid": v(-47.86, 21.94) * mm, "end": v(-47.96, 21.96) * mm});
            skArc(sketch, "E260", {"start": v(-47.96, 21.96) * mm, "mid": v(-48.05, 21.97) * mm, "end": v(-48.13, 22.02) * mm});
            skArc(sketch, "E261", {"start": v(-48.13, 22.02) * mm, "mid": v(-48.2, 22.1) * mm, "end": v(-48.23, 22.18) * mm});
            skArc(sketch, "E262", {"start": v(-48.23, 22.18) * mm, "mid": v(-48.25, 22.3) * mm, "end": v(-48.24, 22.43) * mm});
            skArc(sketch, "E263", {"start": v(-48.24, 22.43) * mm, "mid": v(-48.21, 22.58) * mm, "end": v(-48.17, 22.73) * mm});
            skArc(sketch, "E264", {"start": v(-48.17, 22.73) * mm, "mid": v(-48.1, 22.88) * mm, "end": v(-48, 23.03) * mm});
            skArc(sketch, "E265", {"start": v(-48, 23.03) * mm, "mid": v(-47.88, 23.16) * mm, "end": v(-47.74, 23.28) * mm});
            skArc(sketch, "E266", {"start": v(-47.74, 23.28) * mm, "mid": v(-47.6, 23.37) * mm, "end": v(-47.45, 23.45) * mm});
            skArc(sketch, "E267", {"start": v(-47.45, 23.45) * mm, "mid": v(-47.3, 23.49) * mm, "end": v(-47.15, 23.5) * mm});
            skArc(sketch, "E268", {"start": v(-47.15, 23.5) * mm, "mid": v(-46.86, 23.54) * mm, "end": v(-46.6, 23.65) * mm});
            skArc(sketch, "E269", {"start": v(-46.6, 23.65) * mm, "mid": v(-46.47, 23.8) * mm, "end": v(-46.47, 23.99) * mm});
            skArc(sketch, "E270", {"start": v(-46.47, 23.99) * mm, "mid": v(-46.6, 24.24) * mm, "end": v(-46.83, 24.43) * mm});
            skArc(sketch, "E271", {"start": v(-46.83, 24.43) * mm, "mid": v(-47.2, 24.62) * mm, "end": v(-47.6, 24.77) * mm});
            skArc(sketch, "E272", {"start": v(-47.6, 24.77) * mm, "mid": v(-47.83, 24.85) * mm, "end": v(-48.07, 24.94) * mm});
            skArc(sketch, "E273", {"start": v(-48.07, 24.94) * mm, "mid": v(-48.19, 25) * mm, "end": v(-48.28, 25.1) * mm});
            skArc(sketch, "E274", {"start": v(-48.28, 25.1) * mm, "mid": v(-48.3, 25.18) * mm, "end": v(-48.28, 25.25) * mm});
            skArc(sketch, "E275", {"start": v(-48.28, 25.25) * mm, "mid": v(-48.18, 25.34) * mm, "end": v(-48.08, 25.4) * mm});
            skArc(sketch, "E276", {"start": v(-48.08, 25.4) * mm, "mid": v(-47.93, 25.47) * mm, "end": v(-47.8, 25.58) * mm});
            skArc(sketch, "E277", {"start": v(-47.8, 25.58) * mm, "mid": v(-47.73, 25.69) * mm, "end": v(-47.72, 25.81) * mm});
            skArc(sketch, "E278", {"start": v(-47.72, 25.81) * mm, "mid": v(-47.77, 25.98) * mm, "end": v(-47.86, 26.13) * mm});
            skArc(sketch, "E279", {"start": v(-47.86, 26.13) * mm, "mid": v(-48.06, 26.39) * mm, "end": v(-48.27, 26.63) * mm});
            skArc(sketch, "E280", {"start": v(-48.27, 26.63) * mm, "mid": v(-48.5, 26.92) * mm, "end": v(-48.68, 27.24) * mm});
            skArc(sketch, "E281", {"start": v(-48.68, 27.24) * mm, "mid": v(-48.81, 27.59) * mm, "end": v(-48.9, 27.95) * mm});
            skArc(sketch, "E282", {"start": v(-48.9, 27.95) * mm, "mid": v(-48.96, 28.42) * mm, "end": v(-48.97, 28.88) * mm});
            skArc(sketch, "E283", {"start": v(-48.97, 28.88) * mm, "mid": v(-48.94, 29.54) * mm, "end": v(-48.9, 30.2) * mm});
            skArc(sketch, "E284", {"start": v(-48.9, 30.2) * mm, "mid": v(-48.84, 30.7) * mm, "end": v(-48.78, 31.22) * mm});
            skArc(sketch, "E285", {"start": v(-48.78, 31.22) * mm, "mid": v(-48.72, 31.67) * mm, "end": v(-48.64, 32.11) * mm});
            skArc(sketch, "E286", {"start": v(-48.64, 32.11) * mm, "mid": v(-48.57, 32.49) * mm, "end": v(-48.5, 32.85) * mm});
            skArc(sketch, "E287", {"start": v(-48.5, 32.85) * mm, "mid": v(-48.46, 32.97) * mm, "end": v(-48.38, 33.06) * mm});
            skArc(sketch, "E288", {"start": v(-48.38, 33.06) * mm, "mid": v(-48.28, 33.13) * mm, "end": v(-48.15, 33.14) * mm});
            skArc(sketch, "E289", {"start": v(-48.15, 33.14) * mm, "mid": v(-47.47, 33.07) * mm, "end": v(-46.78, 33) * mm});
            skArc(sketch, "E290", {"start": v(-46.78, 33) * mm, "mid": v(-45.97, 32.9) * mm, "end": v(-45.16, 32.78) * mm});
            skArc(sketch, "E291", {"start": v(-45.16, 32.78) * mm, "mid": v(-44.22, 32.64) * mm, "end": v(-43.28, 32.48) * mm});
            skArc(sketch, "E292", {"start": v(-43.28, 32.48) * mm, "mid": v(-41.28, 32.18) * mm, "end": v(-39.25, 31.97) * mm});
            skArc(sketch, "E293", {"start": v(-39.25, 31.97) * mm, "mid": v(-37.38, 31.88) * mm, "end": v(-35.5, 31.9) * mm});
            skArc(sketch, "E294", {"start": v(-35.5, 31.9) * mm, "mid": v(-33.9, 32) * mm, "end": v(-32.32, 32.22) * mm});
            skArc(sketch, "E295", {"start": v(-32.32, 32.22) * mm, "mid": v(-31.16, 32.5) * mm, "end": v(-30.06, 32.97) * mm});
            skArc(sketch, "E296", {"start": v(-30.06, 32.97) * mm, "mid": v(-29, 34.05) * mm, "end": v(-28.76, 35.55) * mm});
            skArc(sketch, "E297", {"start": v(-28.76, 35.55) * mm, "mid": v(-29.37, 37.35) * mm, "end": v(-30.55, 38.83) * mm});
            skArc(sketch, "E298", {"start": v(-30.55, 38.83) * mm, "mid": v(-33.18, 40.83) * mm, "end": v(-36.08, 42.42) * mm});
            skArc(sketch, "E299", {"start": v(-36.08, 42.42) * mm, "mid": v(-40.04, 44.06) * mm, "end": v(-44.11, 45.43) * mm});
            skArc(sketch, "E300", {"start": v(-44.11, 45.43) * mm, "mid": v(-46.54, 46.06) * mm, "end": v(-49.01, 46.52) * mm});
            skArc(sketch, "E301", {"start": v(-49.01, 46.52) * mm, "mid": v(-51.85, 46.89) * mm, "end": v(-54.71, 47.12) * mm});
            skArc(sketch, "E302", {"start": v(-54.71, 47.12) * mm, "mid": v(-57.34, 47.21) * mm, "end": v(-59.98, 47.2) * mm});
            skArc(sketch, "E303", {"start": v(-59.98, 47.2) * mm, "mid": v(-61.55, 47) * mm, "end": v(-63.05, 46.53) * mm});
            skArc(sketch, "E304", {"start": v(-63.05, 46.53) * mm, "mid": v(-63.64, 46.25) * mm, "end": v(-64.2, 45.93) * mm});
            skArc(sketch, "E305", {"start": v(-64.2, 45.93) * mm, "mid": v(-64.55, 45.63) * mm, "end": v(-64.82, 45.26) * mm});
            skArc(sketch, "E306", {"start": v(-64.82, 45.26) * mm, "mid": v(-65, 44.84) * mm, "end": v(-65.07, 44.39) * mm});
            skArc(sketch, "E307", {"start": v(-65.07, 44.39) * mm, "mid": v(-65.06, 43.74) * mm, "end": v(-65, 43.09) * mm});
            skArc(sketch, "E308", {"start": v(-65, 43.09) * mm, "mid": v(-64.74, 42.27) * mm, "end": v(-64.24, 41.57) * mm});
            skArc(sketch, "E309", {"start": v(-64.24, 41.57) * mm, "mid": v(-63.13, 40.56) * mm, "end": v(-61.96, 39.64) * mm});
            skArc(sketch, "E310", {"start": v(-61.96, 39.64) * mm, "mid": v(-60.44, 38.6) * mm, "end": v(-58.84, 37.66) * mm});
            skArc(sketch, "E311", {"start": v(-58.84, 37.66) * mm, "mid": v(-57.04, 36.73) * mm, "end": v(-55.2, 35.9) * mm});
            skArc(sketch, "E312", {"start": v(-55.2, 35.9) * mm, "mid": v(-54.64, 35.66) * mm, "end": v(-54.08, 35.4) * mm});
            skArc(sketch, "E313", {"start": v(-54.08, 35.4) * mm, "mid": v(-53.58, 35.16) * mm, "end": v(-53.09, 34.9) * mm});
            skArc(sketch, "E314", {"start": v(-53.09, 34.9) * mm, "mid": v(-52.69, 34.67) * mm, "end": v(-52.3, 34.44) * mm});
            skArc(sketch, "E315", {"start": v(-52.3, 34.44) * mm, "mid": v(-52.13, 34.31) * mm, "end": v(-52, 34.16) * mm});
            skArc(sketch, "E316", {"start": v(-52, 34.16) * mm, "mid": v(-51.94, 34) * mm, "end": v(-51.92, 33.84) * mm});
            skArc(sketch, "E317", {"start": v(-51.92, 33.84) * mm, "mid": v(-51.93, 33.55) * mm, "end": v(-51.97, 33.27) * mm});
            skArc(sketch, "E318", {"start": v(-51.97, 33.27) * mm, "mid": v(-52.04, 32.93) * mm, "end": v(-52.12, 32.6) * mm});
            skArc(sketch, "E319", {"start": v(-52.12, 32.6) * mm, "mid": v(-52.24, 32.25) * mm, "end": v(-52.37, 31.9) * mm});
            skArc(sketch, "E320", {"start": v(-52.37, 31.9) * mm, "mid": v(-52.67, 31.17) * mm, "end": v(-52.97, 30.42) * mm});
            skArc(sketch, "E321", {"start": v(-52.97, 30.42) * mm, "mid": v(-52.95, 30.32) * mm, "end": v(-52.84, 30.28) * mm});
            skArc(sketch, "E322", {"start": v(-52.84, 30.28) * mm, "mid": v(-52.67, 30.37) * mm, "end": v(-52.53, 30.5) * mm});
            skArc(sketch, "E323", {"start": v(-52.53, 30.5) * mm, "mid": v(-52.02, 31.31) * mm, "end": v(-51.52, 32.12) * mm});
            skArc(sketch, "E324", {"start": v(-51.52, 32.12) * mm, "mid": v(-51.12, 32.76) * mm, "end": v(-50.71, 33.4) * mm});
            skArc(sketch, "E325", {"start": v(-50.71, 33.4) * mm, "mid": v(-50.6, 33.53) * mm, "end": v(-50.44, 33.62) * mm});
            skArc(sketch, "E326", {"start": v(-50.44, 33.62) * mm, "mid": v(-50.32, 33.62) * mm, "end": v(-50.23, 33.53) * mm});
            skArc(sketch, "E327", {"start": v(-50.23, 33.53) * mm, "mid": v(-50.1, 33.15) * mm, "end": v(-49.98, 32.76) * mm});
            skArc(sketch, "E328", {"start": v(-49.98, 32.76) * mm, "mid": v(-49.74, 31.72) * mm, "end": v(-49.6, 30.67) * mm});
            skArc(sketch, "E329", {"start": v(-49.6, 30.67) * mm, "mid": v(-49.54, 29.53) * mm, "end": v(-49.58, 28.4) * mm});
            skArc(sketch, "E330", {"start": v(-49.58, 28.4) * mm, "mid": v(-49.68, 27.4) * mm, "end": v(-49.86, 26.43) * mm});
            skArc(sketch, "E331", {"start": v(-49.86, 26.43) * mm, "mid": v(-50.08, 25.86) * mm, "end": v(-50.47, 25.39) * mm});
            skArc(sketch, "E332", {"start": v(-50.47, 25.39) * mm, "mid": v(-50.67, 25.22) * mm, "end": v(-50.87, 25.06) * mm});
            skArc(sketch, "E333", {"start": v(-50.87, 25.06) * mm, "mid": v(-51.09, 24.92) * mm, "end": v(-51.31, 24.78) * mm});
            skArc(sketch, "E334", {"start": v(-51.31, 24.78) * mm, "mid": v(-51.51, 24.68) * mm, "end": v(-51.72, 24.6) * mm});
            skArc(sketch, "E335", {"start": v(-51.72, 24.6) * mm, "mid": v(-51.86, 24.55) * mm, "end": v(-52.01, 24.53) * mm});
            skArc(sketch, "E336", {"start": v(-52.01, 24.53) * mm, "mid": v(-52.13, 24.52) * mm, "end": v(-52.24, 24.5) * mm});
            skArc(sketch, "E337", {"start": v(-52.24, 24.5) * mm, "mid": v(-52.35, 24.45) * mm, "end": v(-52.44, 24.38) * mm});
            skArc(sketch, "E338", {"start": v(-52.44, 24.38) * mm, "mid": v(-52.51, 24.3) * mm, "end": v(-52.57, 24.22) * mm});
            skArc(sketch, "E339", {"start": v(-52.57, 24.22) * mm, "mid": v(-52.6, 24.12) * mm, "end": v(-52.62, 24.02) * mm});
            skArc(sketch, "E340", {"start": v(-52.62, 24.02) * mm, "mid": v(-52.6, 23.92) * mm, "end": v(-52.56, 23.82) * mm});
            skArc(sketch, "E341", {"start": v(-52.56, 23.82) * mm, "mid": v(-52.48, 23.73) * mm, "end": v(-52.38, 23.65) * mm});
            skArc(sketch, "E342", {"start": v(-52.38, 23.65) * mm, "mid": v(-52.26, 23.59) * mm, "end": v(-52.12, 23.54) * mm});
            skArc(sketch, "E343", {"start": v(-52.12, 23.54) * mm, "mid": v(-51.97, 23.51) * mm, "end": v(-51.82, 23.5) * mm});
            skArc(sketch, "E344", {"start": v(-51.82, 23.5) * mm, "mid": v(-51.32, 23.38) * mm, "end": v(-50.95, 23.03) * mm});
            skArc(sketch, "E345", {"start": v(-50.95, 23.03) * mm, "mid": v(-50.53, 22.26) * mm, "end": v(-50.2, 21.46) * mm});
            skArc(sketch, "E346", {"start": v(-50.2, 21.46) * mm, "mid": v(-49.9, 20.42) * mm, "end": v(-49.7, 19.36) * mm});
            skArc(sketch, "E347", {"start": v(-49.7, 19.36) * mm, "mid": v(-49.62, 18.25) * mm, "end": v(-49.63, 17.15) * mm});
            skArc(sketch, "E348", {"start": v(-49.63, 17.15) * mm, "mid": v(-49.68, 16.46) * mm, "end": v(-49.74, 15.77) * mm});
            skArc(sketch, "E349", {"start": v(-49.74, 15.77) * mm, "mid": v(-49.8, 15.4) * mm, "end": v(-49.92, 15.05) * mm});
            skArc(sketch, "E350", {"start": v(-49.92, 15.05) * mm, "mid": v(-50.04, 14.85) * mm, "end": v(-50.2, 14.7) * mm});
            skArc(sketch, "E351", {"start": v(-50.2, 14.7) * mm, "mid": v(-50.4, 14.62) * mm, "end": v(-50.62, 14.62) * mm});
            skArc(sketch, "E352", {"start": v(-50.62, 14.62) * mm, "mid": v(-50.81, 14.63) * mm, "end": v(-51, 14.59) * mm});
            skArc(sketch, "E353", {"start": v(-51, 14.59) * mm, "mid": v(-51.17, 14.5) * mm, "end": v(-51.31, 14.39) * mm});
            skArc(sketch, "E354", {"start": v(-51.31, 14.39) * mm, "mid": v(-51.45, 14.2) * mm, "end": v(-51.55, 14) * mm});
            skArc(sketch, "E355", {"start": v(-51.55, 14) * mm, "mid": v(-51.65, 13.73) * mm, "end": v(-51.71, 13.45) * mm});
            skArc(sketch, "E356", {"start": v(-51.71, 13.45) * mm, "mid": v(-51.77, 13.1) * mm, "end": v(-51.81, 12.76) * mm});
            skArc(sketch, "E357", {"start": v(-51.81, 12.76) * mm, "mid": v(-51.8, 12.6) * mm, "end": v(-51.74, 12.45) * mm});
            skArc(sketch, "E358", {"start": v(-51.74, 12.45) * mm, "mid": v(-51.64, 12.36) * mm, "end": v(-51.52, 12.34) * mm});
            skArc(sketch, "E359", {"start": v(-51.52, 12.34) * mm, "mid": v(-51.29, 12.37) * mm, "end": v(-51.07, 12.42) * mm});
            skArc(sketch, "E360", {"start": v(-51.07, 12.42) * mm, "mid": v(-50.75, 12.45) * mm, "end": v(-50.44, 12.34) * mm});
            skArc(sketch, "E361", {"start": v(-50.44, 12.34) * mm, "mid": v(-50.16, 12.1) * mm, "end": v(-49.95, 11.8) * mm});
            skArc(sketch, "E362", {"start": v(-49.95, 11.8) * mm, "mid": v(-49.75, 11.27) * mm, "end": v(-49.64, 10.73) * mm});
            skArc(sketch, "E363", {"start": v(-49.64, 10.73) * mm, "mid": v(-49.56, 9.97) * mm, "end": v(-49.53, 9.2) * mm});
            skArc(sketch, "E364", {"start": v(-49.53, 9.2) * mm, "mid": v(-49.55, 8.92) * mm, "end": v(-49.6, 8.64) * mm});
            skArc(sketch, "E365", {"start": v(-49.6, 8.64) * mm, "mid": v(-49.68, 8.44) * mm, "end": v(-49.8, 8.28) * mm});
            skArc(sketch, "E366", {"start": v(-49.8, 8.28) * mm, "mid": v(-49.98, 8.15) * mm, "end": v(-50.19, 8.07) * mm});
            skArc(sketch, "E367", {"start": v(-50.19, 8.07) * mm, "mid": v(-50.5, 8) * mm, "end": v(-50.81, 7.98) * mm});
            skArc(sketch, "E368", {"start": v(-50.81, 7.98) * mm, "mid": v(-51.08, 7.96) * mm, "end": v(-51.35, 7.95) * mm});
            skArc(sketch, "E369", {"start": v(-51.35, 7.95) * mm, "mid": v(-51.62, 7.93) * mm, "end": v(-51.89, 7.91) * mm});
            skArc(sketch, "E370", {"start": v(-51.89, 7.91) * mm, "mid": v(-52.13, 7.9) * mm, "end": v(-52.37, 7.88) * mm});
            skArc(sketch, "E371", {"start": v(-52.37, 7.88) * mm, "mid": v(-52.52, 7.86) * mm, "end": v(-52.67, 7.85) * mm});
            skArc(sketch, "E372", {"start": v(-52.67, 7.85) * mm, "mid": v(-52.8, 7.8) * mm, "end": v(-52.9, 7.67) * mm});
            skArc(sketch, "E373", {"start": v(-52.9, 7.67) * mm, "mid": v(-53.02, 7.34) * mm, "end": v(-53.13, 7) * mm});
            skArc(sketch, "E374", {"start": v(-53.13, 7) * mm, "mid": v(-53.24, 6.57) * mm, "end": v(-53.32, 6.12) * mm});
            skArc(sketch, "E375", {"start": v(-53.32, 6.12) * mm, "mid": v(-53.4, 5.6) * mm, "end": v(-53.44, 5.08) * mm});
            skArc(sketch, "E376", {"start": v(-53.44, 5.08) * mm, "mid": v(-53.5, 4.3) * mm, "end": v(-53.54, 3.51) * mm});
            skArc(sketch, "E377", {"start": v(-53.54, 3.51) * mm, "mid": v(-53.52, 3.16) * mm, "end": v(-53.45, 2.82) * mm});
            skArc(sketch, "E378", {"start": v(-53.45, 2.82) * mm, "mid": v(-53.35, 2.63) * mm, "end": v(-53.18, 2.5) * mm});
            skArc(sketch, "E379", {"start": v(-53.18, 2.5) * mm, "mid": v(-52.93, 2.4) * mm, "end": v(-52.66, 2.37) * mm});
            skArc(sketch, "E380", {"start": v(-52.66, 2.37) * mm, "mid": v(-52.37, 2.32) * mm, "end": v(-52.13, 2.17) * mm});
            skArc(sketch, "E381", {"start": v(-52.13, 2.17) * mm, "mid": v(-51.94, 1.93) * mm, "end": v(-51.83, 1.64) * mm});
            skArc(sketch, "E382", {"start": v(-51.83, 1.64) * mm, "mid": v(-51.75, 1.08) * mm, "end": v(-51.73, 0.5) * mm});
            skArc(sketch, "E383", {"start": v(-51.73, 0.5) * mm, "mid": v(-51.73, -0.92) * mm, "end": v(-51.75, -2.35) * mm});
            skArc(sketch, "E384", {"start": v(-51.75, -2.35) * mm, "mid": v(-51.78, -3.4) * mm, "end": v(-51.83, -4.44) * mm});
            skArc(sketch, "E385", {"start": v(-51.83, -4.44) * mm, "mid": v(-51.89, -5.19) * mm, "end": v(-51.98, -5.94) * mm});
            skArc(sketch, "E386", {"start": v(-51.98, -5.94) * mm, "mid": v(-52.06, -6.46) * mm, "end": v(-52.18, -6.98) * mm});
            skArc(sketch, "E387", {"start": v(-52.18, -6.98) * mm, "mid": v(-52.28, -7.17) * mm, "end": v(-52.46, -7.28) * mm});
            skArc(sketch, "E388", {"start": v(-52.46, -7.28) * mm, "mid": v(-52.6, -7.29) * mm, "end": v(-52.72, -7.23) * mm});
            skArc(sketch, "E389", {"start": v(-52.72, -7.23) * mm, "mid": v(-52.86, -7.08) * mm, "end": v(-52.96, -6.9) * mm});
            skArc(sketch, "E390", {"start": v(-52.96, -6.9) * mm, "mid": v(-53.07, -6.62) * mm, "end": v(-53.15, -6.33) * mm});
            skArc(sketch, "E391", {"start": v(-53.15, -6.33) * mm, "mid": v(-53.22, -5.93) * mm, "end": v(-53.27, -5.52) * mm});
            skLineSegment(sketch, "E392", {"start": v(-53.27, -5.52) * mm, "end": v(-53.48, -3.56) * mm});
            skLineSegment(sketch, "E393", {"start": v(-53.48, -3.56) * mm, "end": v(-53.56, -5.7) * mm});
            skArc(sketch, "E394", {"start": v(-53.56, -5.7) * mm, "mid": v(-53.6, -6.16) * mm, "end": v(-53.65, -6.62) * mm});
            skArc(sketch, "E395", {"start": v(-53.65, -6.62) * mm, "mid": v(-53.72, -6.99) * mm, "end": v(-53.83, -7.35) * mm});
            skArc(sketch, "E396", {"start": v(-53.83, -7.35) * mm, "mid": v(-53.94, -7.61) * mm, "end": v(-54.09, -7.86) * mm});
            skArc(sketch, "E397", {"start": v(-54.09, -7.86) * mm, "mid": v(-54.23, -8.02) * mm, "end": v(-54.42, -8.12) * mm});
            skArc(sketch, "E398", {"start": v(-54.42, -8.12) * mm, "mid": v(-54.73, -8.32) * mm, "end": v(-54.93, -8.63) * mm});
            skArc(sketch, "E399", {"start": v(-54.93, -8.63) * mm, "mid": v(-55.1, -9.16) * mm, "end": v(-55.18, -9.7) * mm});
            skArc(sketch, "E400", {"start": v(-55.18, -9.7) * mm, "mid": v(-55.18, -10.2) * mm, "end": v(-55.1, -10.69) * mm});
            skArc(sketch, "E401", {"start": v(-55.1, -10.69) * mm, "mid": v(-54.95, -10.93) * mm, "end": v(-54.68, -11.03) * mm});
            skArc(sketch, "E402", {"start": v(-54.68, -11.03) * mm, "mid": v(-54.53, -11.08) * mm, "end": v(-54.46, -11.22) * mm});
            skArc(sketch, "E403", {"start": v(-54.46, -11.22) * mm, "mid": v(-54.37, -11.91) * mm, "end": v(-54.3, -12.6) * mm});
            skArc(sketch, "E404", {"start": v(-54.3, -12.6) * mm, "mid": v(-54.24, -13.52) * mm, "end": v(-54.2, -14.43) * mm});
            skArc(sketch, "E405", {"start": v(-54.2, -14.43) * mm, "mid": v(-54.18, -15.63) * mm, "end": v(-54.18, -16.83) * mm});
            skLineSegment(sketch, "E406", {"start": v(-54.18, -16.83) * mm, "end": v(-54.2, -22.63) * mm});
            skLineSegment(sketch, "E407", {"start": v(-54.2, -22.63) * mm, "end": v(-56, -23.91) * mm});
            skArc(sketch, "E408", {"start": v(-56, -23.91) * mm, "mid": v(-56.54, -24.34) * mm, "end": v(-57.04, -24.81) * mm});
            skArc(sketch, "E409", {"start": v(-57.04, -24.81) * mm, "mid": v(-58.16, -25.97) * mm, "end": v(-59.26, -27.13) * mm});
            skArc(sketch, "E410", {"start": v(-59.26, -27.13) * mm, "mid": v(-60.56, -28.54) * mm, "end": v(-61.84, -29.96) * mm});
            skArc(sketch, "E411", {"start": v(-61.84, -29.96) * mm, "mid": v(-63.2, -31.5) * mm, "end": v(-64.55, -33.06) * mm});
            skArc(sketch, "E412", {"start": v(-64.55, -33.06) * mm, "mid": v(-65.86, -34.57) * mm, "end": v(-67.18, -36.08) * mm});
            skArc(sketch, "E413", {"start": v(-67.18, -36.08) * mm, "mid": v(-68.32, -37.35) * mm, "end": v(-69.47, -38.61) * mm});
            skArc(sketch, "E414", {"start": v(-69.47, -38.61) * mm, "mid": v(-70.48, -39.7) * mm, "end": v(-71.49, -40.78) * mm});
            skArc(sketch, "E415", {"start": v(-71.49, -40.78) * mm, "mid": v(-71.64, -40.88) * mm, "end": v(-71.83, -40.92) * mm});
            skArc(sketch, "E416", {"start": v(-71.83, -40.92) * mm, "mid": v(-72.12, -40.98) * mm, "end": v(-72.37, -41.13) * mm});
            skArc(sketch, "E417", {"start": v(-72.37, -41.13) * mm, "mid": v(-72.71, -41.46) * mm, "end": v(-73.02, -41.83) * mm});
            skArc(sketch, "E418", {"start": v(-73.02, -41.83) * mm, "mid": v(-73.3, -42.24) * mm, "end": v(-73.55, -42.68) * mm});
            skArc(sketch, "E419", {"start": v(-73.55, -42.68) * mm, "mid": v(-73.68, -43.03) * mm, "end": v(-73.73, -43.4) * mm});
            skArc(sketch, "E420", {"start": v(-73.73, -43.4) * mm, "mid": v(-73.7, -43.55) * mm, "end": v(-73.63, -43.69) * mm});
            skArc(sketch, "E421", {"start": v(-73.63, -43.69) * mm, "mid": v(-73.5, -43.8) * mm, "end": v(-73.33, -43.87) * mm});
            skArc(sketch, "E422", {"start": v(-73.33, -43.87) * mm, "mid": v(-73.08, -43.93) * mm, "end": v(-72.82, -43.95) * mm});
            skArc(sketch, "E423", {"start": v(-72.82, -43.95) * mm, "mid": v(-72.45, -43.94) * mm, "end": v(-72.07, -43.92) * mm});
            skArc(sketch, "E424", {"start": v(-72.07, -43.92) * mm, "mid": v(-71.64, -43.86) * mm, "end": v(-71.22, -43.78) * mm});
            skArc(sketch, "E425", {"start": v(-71.22, -43.78) * mm, "mid": v(-70.95, -43.68) * mm, "end": v(-70.7, -43.53) * mm});
            skArc(sketch, "E426", {"start": v(-70.7, -43.53) * mm, "mid": v(-70.52, -43.35) * mm, "end": v(-70.4, -43.13) * mm});
            skArc(sketch, "E427", {"start": v(-70.4, -43.13) * mm, "mid": v(-70.29, -42.82) * mm, "end": v(-70.22, -42.5) * mm});
            skArc(sketch, "E428", {"start": v(-70.22, -42.5) * mm, "mid": v(-69.95, -41.54) * mm, "end": v(-69.43, -40.7) * mm});
            skArc(sketch, "E429", {"start": v(-69.43, -40.7) * mm, "mid": v(-67.44, -38.3) * mm, "end": v(-65.41, -35.93) * mm});
            skArc(sketch, "E430", {"start": v(-65.41, -35.93) * mm, "mid": v(-63.29, -33.5) * mm, "end": v(-61.13, -31.1) * mm});
            skArc(sketch, "E431", {"start": v(-61.13, -31.1) * mm, "mid": v(-60.68, -30.86) * mm, "end": v(-60.18, -30.95) * mm});
            skArc(sketch, "E432", {"start": v(-60.18, -30.95) * mm, "mid": v(-59.82, -31.17) * mm, "end": v(-59.48, -31.41) * mm});
            skArc(sketch, "E433", {"start": v(-59.48, -31.41) * mm, "mid": v(-58.57, -32.07) * mm, "end": v(-57.67, -32.74) * mm});
            skArc(sketch, "E434", {"start": v(-57.67, -32.74) * mm, "mid": v(-56.78, -33.4) * mm, "end": v(-55.9, -34.07) * mm});
            skArc(sketch, "E435", {"start": v(-55.9, -34.07) * mm, "mid": v(-55.44, -34.43) * mm, "end": v(-54.98, -34.8) * mm});
            skArc(sketch, "E436", {"start": v(-54.98, -34.8) * mm, "mid": v(-54.8, -35.1) * mm, "end": v(-54.8, -35.46) * mm});
            skArc(sketch, "E437", {"start": v(-54.8, -35.46) * mm, "mid": v(-55.01, -35.84) * mm, "end": v(-55.34, -36.12) * mm});
            skArc(sketch, "E438", {"start": v(-55.34, -36.12) * mm, "mid": v(-55.95, -36.43) * mm, "end": v(-56.6, -36.63) * mm});
            skArc(sketch, "E439", {"start": v(-56.6, -36.63) * mm, "mid": v(-57.4, -36.76) * mm, "end": v(-58.22, -36.8) * mm});
            skArc(sketch, "E440", {"start": v(-58.22, -36.8) * mm, "mid": v(-59.17, -36.83) * mm, "end": v(-60.11, -36.9) * mm});
            skArc(sketch, "E441", {"start": v(-60.11, -36.9) * mm, "mid": v(-60.63, -37.01) * mm, "end": v(-61.1, -37.24) * mm});
            skArc(sketch, "E442", {"start": v(-61.1, -37.24) * mm, "mid": v(-61.46, -37.54) * mm, "end": v(-61.7, -37.93) * mm});
            skArc(sketch, "E443", {"start": v(-61.7, -37.93) * mm, "mid": v(-61.95, -38.58) * mm, "end": v(-62.13, -39.25) * mm});
            skArc(sketch, "E444", {"start": v(-62.13, -39.25) * mm, "mid": v(-62.22, -39.7) * mm, "end": v(-62.29, -40.14) * mm});
            skArc(sketch, "E445", {"start": v(-62.29, -40.14) * mm, "mid": v(-62.3, -40.37) * mm, "end": v(-62.25, -40.6) * mm});
            skArc(sketch, "E446", {"start": v(-62.25, -40.6) * mm, "mid": v(-62.17, -40.74) * mm, "end": v(-62.04, -40.84) * mm});
            skArc(sketch, "E447", {"start": v(-62.04, -40.84) * mm, "mid": v(-61.84, -40.9) * mm, "end": v(-61.62, -40.92) * mm});
            skArc(sketch, "E448", {"start": v(-61.62, -40.92) * mm, "mid": v(-61.42, -40.9) * mm, "end": v(-61.22, -40.85) * mm});
            skArc(sketch, "E449", {"start": v(-61.22, -40.85) * mm, "mid": v(-61.1, -40.78) * mm, "end": v(-61, -40.65) * mm});
            skArc(sketch, "E450", {"start": v(-61, -40.65) * mm, "mid": v(-60.95, -40.47) * mm, "end": v(-60.95, -40.28) * mm});
            skArc(sketch, "E451", {"start": v(-60.95, -40.28) * mm, "mid": v(-61, -39.97) * mm, "end": v(-61.07, -39.65) * mm});
            skArc(sketch, "E452", {"start": v(-61.07, -39.65) * mm, "mid": v(-61.12, -39.15) * mm, "end": v(-61.03, -38.64) * mm});
            skArc(sketch, "E453", {"start": v(-61.03, -38.64) * mm, "mid": v(-60.8, -38.22) * mm, "end": v(-60.45, -37.9) * mm});
            skArc(sketch, "E454", {"start": v(-60.45, -37.9) * mm, "mid": v(-59.88, -37.6) * mm, "end": v(-59.26, -37.45) * mm});
            skArc(sketch, "E455", {"start": v(-59.26, -37.45) * mm, "mid": v(-58.33, -37.35) * mm, "end": v(-57.4, -37.31) * mm});
            skArc(sketch, "E456", {"start": v(-57.4, -37.31) * mm, "mid": v(-56.98, -37.3) * mm, "end": v(-56.57, -37.26) * mm});
            skArc(sketch, "E457", {"start": v(-56.57, -37.26) * mm, "mid": v(-56.12, -37.19) * mm, "end": v(-55.69, -37.09) * mm});
            skArc(sketch, "E458", {"start": v(-55.69, -37.09) * mm, "mid": v(-55.29, -36.98) * mm, "end": v(-54.9, -36.84) * mm});
            skArc(sketch, "E459", {"start": v(-54.9, -36.84) * mm, "mid": v(-54.6, -36.71) * mm, "end": v(-54.33, -36.55) * mm});
            skArc(sketch, "E460", {"start": v(-54.33, -36.55) * mm, "mid": v(-54.02, -36.34) * mm, "end": v(-53.7, -36.15) * mm});
            skArc(sketch, "E461", {"start": v(-53.7, -36.15) * mm, "mid": v(-53.52, -36.07) * mm, "end": v(-53.32, -36.04) * mm});
            skArc(sketch, "E462", {"start": v(-53.32, -36.04) * mm, "mid": v(-53.15, -36.07) * mm, "end": v(-53, -36.16) * mm});
            skArc(sketch, "E463", {"start": v(-53, -36.16) * mm, "mid": v(-52.8, -36.35) * mm, "end": v(-52.6, -36.55) * mm});
            skArc(sketch, "E464", {"start": v(-52.6, -36.55) * mm, "mid": v(-52.42, -36.73) * mm, "end": v(-52.2, -36.87) * mm});
            skArc(sketch, "E465", {"start": v(-52.2, -36.87) * mm, "mid": v(-51.86, -37) * mm, "end": v(-51.5, -37.1) * mm});
            skArc(sketch, "E466", {"start": v(-51.5, -37.1) * mm, "mid": v(-51.07, -37.2) * mm, "end": v(-50.63, -37.26) * mm});
            skArc(sketch, "E467", {"start": v(-50.63, -37.26) * mm, "mid": v(-50.1, -37.3) * mm, "end": v(-49.6, -37.31) * mm});
            skArc(sketch, "E468", {"start": v(-49.6, -37.31) * mm, "mid": v(-48.85, -37.3) * mm, "end": v(-48.12, -37.23) * mm});
            skArc(sketch, "E469", {"start": v(-48.12, -37.23) * mm, "mid": v(-47.7, -37.14) * mm, "end": v(-47.3, -36.95) * mm});
            skArc(sketch, "E470", {"start": v(-47.3, -36.95) * mm, "mid": v(-46.9, -36.66) * mm, "end": v(-46.58, -36.3) * mm});
            skArc(sketch, "E471", {"start": v(-46.58, -36.3) * mm, "mid": v(-46, -35.52) * mm, "end": v(-45.44, -34.72) * mm});
            skArc(sketch, "E472", {"start": v(-45.44, -34.72) * mm, "mid": v(-45.1, -34.24) * mm, "end": v(-44.74, -33.76) * mm});
            skArc(sketch, "E473", {"start": v(-44.74, -33.76) * mm, "mid": v(-44.43, -33.38) * mm, "end": v(-44.1, -33.01) * mm});
            skArc(sketch, "E474", {"start": v(-44.1, -33.01) * mm, "mid": v(-43.83, -32.76) * mm, "end": v(-43.56, -32.51) * mm});
            skArc(sketch, "E475", {"start": v(-43.56, -32.51) * mm, "mid": v(-43.44, -32.48) * mm, "end": v(-43.33, -32.53) * mm});
            skArc(sketch, "E476", {"start": v(-43.33, -32.53) * mm, "mid": v(-43.23, -32.66) * mm, "end": v(-43.15, -32.8) * mm});
            skArc(sketch, "E477", {"start": v(-43.15, -32.8) * mm, "mid": v(-42.99, -33.13) * mm, "end": v(-42.83, -33.47) * mm});
            skArc(sketch, "E478", {"start": v(-42.83, -33.47) * mm, "mid": v(-42.65, -33.87) * mm, "end": v(-42.48, -34.27) * mm});
            skArc(sketch, "E479", {"start": v(-42.48, -34.27) * mm, "mid": v(-42.3, -34.7) * mm, "end": v(-42.12, -35.15) * mm});
            skArc(sketch, "E480", {"start": v(-42.12, -35.15) * mm, "mid": v(-41.85, -35.96) * mm, "end": v(-41.66, -36.8) * mm});
            skArc(sketch, "E481", {"start": v(-41.66, -36.8) * mm, "mid": v(-41.6, -37.43) * mm, "end": v(-41.7, -38.07) * mm});
            skArc(sketch, "E482", {"start": v(-41.7, -38.07) * mm, "mid": v(-41.91, -38.6) * mm, "end": v(-42.25, -39.07) * mm});
            skArc(sketch, "E483", {"start": v(-42.25, -39.07) * mm, "mid": v(-42.76, -39.52) * mm, "end": v(-43.33, -39.89) * mm});
            skArc(sketch, "E484", {"start": v(-43.33, -39.89) * mm, "mid": v(-43.52, -40) * mm, "end": v(-43.7, -40.15) * mm});
            skArc(sketch, "E485", {"start": v(-43.7, -40.15) * mm, "mid": v(-43.84, -40.3) * mm, "end": v(-43.96, -40.48) * mm});
            skArc(sketch, "E486", {"start": v(-43.96, -40.48) * mm, "mid": v(-44.04, -40.64) * mm, "end": v(-44.09, -40.83) * mm});
            skArc(sketch, "E487", {"start": v(-44.09, -40.83) * mm, "mid": v(-44.1, -40.98) * mm, "end": v(-44.06, -41.14) * mm});
            skArc(sketch, "E488", {"start": v(-44.06, -41.14) * mm, "mid": v(-43.99, -41.56) * mm, "end": v(-44.09, -41.97) * mm});
            skArc(sketch, "E489", {"start": v(-44.09, -41.97) * mm, "mid": v(-44.55, -42.92) * mm, "end": v(-45.04, -43.84) * mm});
            skArc(sketch, "E490", {"start": v(-45.04, -43.84) * mm, "mid": v(-45.64, -44.85) * mm, "end": v(-46.29, -45.83) * mm});
            skArc(sketch, "E491", {"start": v(-46.29, -45.83) * mm, "mid": v(-46.93, -46.68) * mm, "end": v(-47.62, -47.5) * mm});
            skLineSegment(sketch, "E492", {"start": v(-47.62, -47.5) * mm, "end": v(-48.67, -48.65) * mm});
            skLineSegment(sketch, "E493", {"start": v(-48.67, -48.65) * mm, "end": v(-47.04, -48.65) * mm});
            skArc(sketch, "E494", {"start": v(-47.04, -48.65) * mm, "mid": v(-46.62, -48.64) * mm, "end": v(-46.2, -48.6) * mm});
            skArc(sketch, "E495", {"start": v(-46.2, -48.6) * mm, "mid": v(-45.95, -48.55) * mm, "end": v(-45.73, -48.44) * mm});
            skArc(sketch, "E496", {"start": v(-45.73, -48.44) * mm, "mid": v(-45.58, -48.3) * mm, "end": v(-45.48, -48.12) * mm});
            skArc(sketch, "E497", {"start": v(-45.48, -48.12) * mm, "mid": v(-45.42, -47.86) * mm, "end": v(-45.4, -47.59) * mm});
            skArc(sketch, "E498", {"start": v(-45.4, -47.59) * mm, "mid": v(-45.33, -46.93) * mm, "end": v(-45.12, -46.3) * mm});
            skArc(sketch, "E499", {"start": v(-45.12, -46.3) * mm, "mid": v(-44.63, -45.3) * mm, "end": v(-44.1, -44.31) * mm});
            skArc(sketch, "E500", {"start": v(-44.1, -44.31) * mm, "mid": v(-43.51, -43.36) * mm, "end": v(-42.89, -42.43) * mm});
            skArc(sketch, "E501", {"start": v(-42.89, -42.43) * mm, "mid": v(-42.5, -42.03) * mm, "end": v(-42.03, -41.76) * mm});
            skArc(sketch, "E502", {"start": v(-42.03, -41.76) * mm, "mid": v(-41.88, -41.68) * mm, "end": v(-41.74, -41.57) * mm});
            skArc(sketch, "E503", {"start": v(-41.74, -41.57) * mm, "mid": v(-41.61, -41.42) * mm, "end": v(-41.5, -41.25) * mm});
            skArc(sketch, "E504", {"start": v(-41.5, -41.25) * mm, "mid": v(-41.4, -41.05) * mm, "end": v(-41.33, -40.84) * mm});
            skArc(sketch, "E505", {"start": v(-41.33, -40.84) * mm, "mid": v(-41.3, -40.64) * mm, "end": v(-41.28, -40.42) * mm});
            skArc(sketch, "E506", {"start": v(-41.28, -40.42) * mm, "mid": v(-41.27, -40.22) * mm, "end": v(-41.25, -40.02) * mm});
            skArc(sketch, "E507", {"start": v(-41.25, -40.02) * mm, "mid": v(-41.21, -39.85) * mm, "end": v(-41.16, -39.68) * mm});
            skArc(sketch, "E508", {"start": v(-41.16, -39.68) * mm, "mid": v(-41.1, -39.56) * mm, "end": v(-41.02, -39.45) * mm});
            skArc(sketch, "E509", {"start": v(-41.02, -39.45) * mm, "mid": v(-40.95, -39.4) * mm, "end": v(-40.87, -39.38) * mm});
            skArc(sketch, "E510", {"start": v(-40.87, -39.38) * mm, "mid": v(-40.55, -39.47) * mm, "end": v(-40.34, -39.73) * mm});
            skArc(sketch, "E511", {"start": v(-40.34, -39.73) * mm, "mid": v(-39.93, -40.84) * mm, "end": v(-39.55, -41.95) * mm});
            skArc(sketch, "E512", {"start": v(-39.55, -41.95) * mm, "mid": v(-39.2, -43.1) * mm, "end": v(-38.9, -44.26) * mm});
            skArc(sketch, "E513", {"start": v(-38.9, -44.26) * mm, "mid": v(-38.75, -45.1) * mm, "end": v(-38.7, -45.95) * mm});
            skArc(sketch, "E514", {"start": v(-38.7, -45.95) * mm, "mid": v(-38.69, -46.38) * mm, "end": v(-38.66, -46.8) * mm});
            skArc(sketch, "E515", {"start": v(-38.66, -46.8) * mm, "mid": v(-38.6, -47.05) * mm, "end": v(-38.5, -47.28) * mm});
            skArc(sketch, "E516", {"start": v(-38.5, -47.28) * mm, "mid": v(-38.36, -47.44) * mm, "end": v(-38.18, -47.54) * mm});
            skArc(sketch, "E517", {"start": v(-38.18, -47.54) * mm, "mid": v(-37.93, -47.6) * mm, "end": v(-37.67, -47.62) * mm});
            skArc(sketch, "E518", {"start": v(-37.67, -47.62) * mm, "mid": v(-37.3, -47.55) * mm, "end": v(-36.97, -47.33) * mm});
            skArc(sketch, "E519", {"start": v(-36.97, -47.33) * mm, "mid": v(-36.78, -47.02) * mm, "end": v(-36.73, -46.65) * mm});
            skArc(sketch, "E520", {"start": v(-36.73, -46.65) * mm, "mid": v(-36.84, -45.93) * mm, "end": v(-37.04, -45.23) * mm});
            skArc(sketch, "E521", {"start": v(-37.04, -45.23) * mm, "mid": v(-37.6, -43.67) * mm, "end": v(-38.19, -42.13) * mm});
            skArc(sketch, "E522", {"start": v(-38.19, -42.13) * mm, "mid": v(-38.7, -40.75) * mm, "end": v(-39.2, -39.36) * mm});
            skArc(sketch, "E523", {"start": v(-39.2, -39.36) * mm, "mid": v(-39.44, -38.54) * mm, "end": v(-39.63, -37.7) * mm});
            skArc(sketch, "E524", {"start": v(-39.63, -37.7) * mm, "mid": v(-39.68, -37.17) * mm, "end": v(-39.64, -36.64) * mm});
            skArc(sketch, "E525", {"start": v(-39.64, -36.64) * mm, "mid": v(-39.51, -36.3) * mm, "end": v(-39.25, -36.05) * mm});
            skArc(sketch, "E526", {"start": v(-39.25, -36.05) * mm, "mid": v(-39.02, -35.98) * mm, "end": v(-38.8, -36.04) * mm});
            skArc(sketch, "E527", {"start": v(-38.8, -36.04) * mm, "mid": v(-38.55, -36.23) * mm, "end": v(-38.36, -36.47) * mm});
            skArc(sketch, "E528", {"start": v(-38.36, -36.47) * mm, "mid": v(-38.15, -36.93) * mm, "end": v(-38, -37.4) * mm});
            skArc(sketch, "E529", {"start": v(-38, -37.4) * mm, "mid": v(-37.83, -38.12) * mm, "end": v(-37.7, -38.84) * mm});
            skArc(sketch, "E530", {"start": v(-37.7, -38.84) * mm, "mid": v(-37.6, -39.29) * mm, "end": v(-37.5, -39.73) * mm});
            skArc(sketch, "E531", {"start": v(-37.5, -39.73) * mm, "mid": v(-37.4, -40.01) * mm, "end": v(-37.24, -40.27) * mm});
            skArc(sketch, "E532", {"start": v(-37.24, -40.27) * mm, "mid": v(-37.08, -40.44) * mm, "end": v(-36.87, -40.56) * mm});
            skArc(sketch, "E533", {"start": v(-36.87, -40.56) * mm, "mid": v(-36.63, -40.64) * mm, "end": v(-36.37, -40.66) * mm});
            skArc(sketch, "E534", {"start": v(-36.37, -40.66) * mm, "mid": v(-36.16, -40.65) * mm, "end": v(-35.94, -40.6) * mm});
            skArc(sketch, "E535", {"start": v(-35.94, -40.6) * mm, "mid": v(-35.78, -40.54) * mm, "end": v(-35.63, -40.43) * mm});
            skArc(sketch, "E536", {"start": v(-35.63, -40.43) * mm, "mid": v(-35.53, -40.3) * mm, "end": v(-35.46, -40.14) * mm});
            skArc(sketch, "E537", {"start": v(-35.46, -40.14) * mm, "mid": v(-35.43, -39.96) * mm, "end": v(-35.42, -39.76) * mm});
            skArc(sketch, "E538", {"start": v(-35.42, -39.76) * mm, "mid": v(-35.4, -39.48) * mm, "end": v(-35.32, -39.2) * mm});
            skArc(sketch, "E539", {"start": v(-35.32, -39.2) * mm, "mid": v(-35.18, -39.01) * mm, "end": v(-34.97, -38.9) * mm});
            skArc(sketch, "E540", {"start": v(-34.97, -38.9) * mm, "mid": v(-34.68, -38.88) * mm, "end": v(-34.39, -38.94) * mm});
            skArc(sketch, "E541", {"start": v(-34.39, -38.94) * mm, "mid": v(-34, -39.11) * mm, "end": v(-33.62, -39.32) * mm});
            skArc(sketch, "E542", {"start": v(-33.62, -39.32) * mm, "mid": v(-33.46, -39.45) * mm, "end": v(-33.33, -39.62) * mm});
            skArc(sketch, "E543", {"start": v(-33.33, -39.62) * mm, "mid": v(-33.23, -39.83) * mm, "end": v(-33.17, -40.05) * mm});
            skArc(sketch, "E544", {"start": v(-33.17, -40.05) * mm, "mid": v(-33.15, -40.34) * mm, "end": v(-33.16, -40.64) * mm});
            skArc(sketch, "E545", {"start": v(-33.16, -40.64) * mm, "mid": v(-33.21, -41.03) * mm, "end": v(-33.29, -41.42) * mm});
            skArc(sketch, "E546", {"start": v(-33.29, -41.42) * mm, "mid": v(-33.38, -41.89) * mm, "end": v(-33.46, -42.36) * mm});
            skArc(sketch, "E547", {"start": v(-33.46, -42.36) * mm, "mid": v(-33.47, -42.56) * mm, "end": v(-33.42, -42.76) * mm});
            skArc(sketch, "E548", {"start": v(-33.42, -42.76) * mm, "mid": v(-33.33, -42.87) * mm, "end": v(-33.2, -42.92) * mm});
            skArc(sketch, "E549", {"start": v(-33.2, -42.92) * mm, "mid": v(-32.94, -42.92) * mm, "end": v(-32.7, -42.9) * mm});
            skArc(sketch, "E550", {"start": v(-32.7, -42.9) * mm, "mid": v(-32.47, -42.83) * mm, "end": v(-32.27, -42.73) * mm});
            skArc(sketch, "E551", {"start": v(-32.27, -42.73) * mm, "mid": v(-32.11, -42.6) * mm, "end": v(-32, -42.44) * mm});
            skArc(sketch, "E552", {"start": v(-32, -42.44) * mm, "mid": v(-31.91, -42.23) * mm, "end": v(-31.88, -42) * mm});
            skArc(sketch, "E553", {"start": v(-31.88, -42) * mm, "mid": v(-31.88, -41.67) * mm, "end": v(-31.9, -41.35) * mm});
            skArc(sketch, "E554", {"start": v(-31.9, -41.35) * mm, "mid": v(-31.9, -41.07) * mm, "end": v(-31.83, -40.79) * mm});
            skArc(sketch, "E555", {"start": v(-31.83, -40.79) * mm, "mid": v(-31.71, -40.67) * mm, "end": v(-31.54, -40.68) * mm});
            skArc(sketch, "E556", {"start": v(-31.54, -40.68) * mm, "mid": v(-31.17, -40.91) * mm, "end": v(-30.83, -41.19) * mm});
            skArc(sketch, "E557", {"start": v(-30.83, -41.19) * mm, "mid": v(-29.86, -42.09) * mm, "end": v(-28.9, -43) * mm});
            skArc(sketch, "E558", {"start": v(-28.9, -43) * mm, "mid": v(-27.5, -44.3) * mm, "end": v(-26.1, -45.61) * mm});
            skArc(sketch, "E559", {"start": v(-26.1, -45.61) * mm, "mid": v(-25.4, -46.23) * mm, "end": v(-24.67, -46.83) * mm});
            skArc(sketch, "E560", {"start": v(-24.67, -46.83) * mm, "mid": v(-24.22, -47.15) * mm, "end": v(-23.75, -47.44) * mm});
            skArc(sketch, "E561", {"start": v(-23.75, -47.44) * mm, "mid": v(-23.4, -47.57) * mm, "end": v(-23.01, -47.62) * mm});
            skArc(sketch, "E562", {"start": v(-23.01, -47.62) * mm, "mid": v(-22.86, -47.63) * mm, "end": v(-22.7, -47.65) * mm});
            skArc(sketch, "E563", {"start": v(-22.7, -47.65) * mm, "mid": v(-22.56, -47.7) * mm, "end": v(-22.4, -47.75) * mm});
            skArc(sketch, "E564", {"start": v(-22.4, -47.75) * mm, "mid": v(-22.28, -47.81) * mm, "end": v(-22.16, -47.89) * mm});
            skArc(sketch, "E565", {"start": v(-22.16, -47.89) * mm, "mid": v(-22.07, -47.96) * mm, "end": v(-22, -48.05) * mm});
            skArc(sketch, "E566", {"start": v(-22, -48.05) * mm, "mid": v(-21.4, -48.64) * mm, "end": v(-20.59, -48.86) * mm});
            skArc(sketch, "E567", {"start": v(-20.59, -48.86) * mm, "mid": v(-17.62, -48.9) * mm, "end": v(-14.65, -48.87) * mm});
            skArc(sketch, "E568", {"start": v(-14.65, -48.87) * mm, "mid": v(-11.71, -48.78) * mm, "end": v(-8.78, -48.6) * mm});
            skArc(sketch, "E569", {"start": v(-8.78, -48.6) * mm, "mid": v(-7.73, -48.34) * mm, "end": v(-6.83, -47.75) * mm});
            skArc(sketch, "E570", {"start": v(-6.83, -47.75) * mm, "mid": v(-6.7, -47.62) * mm, "end": v(-6.54, -47.52) * mm});
            skArc(sketch, "E571", {"start": v(-6.54, -47.52) * mm, "mid": v(-6.39, -47.43) * mm, "end": v(-6.22, -47.37) * mm});
            skArc(sketch, "E572", {"start": v(-6.22, -47.37) * mm, "mid": v(-6.08, -47.33) * mm, "end": v(-5.93, -47.3) * mm});
            skArc(sketch, "E573", {"start": v(-5.93, -47.3) * mm, "mid": v(-5.82, -47.32) * mm, "end": v(-5.72, -47.36) * mm});
            skArc(sketch, "E574", {"start": v(-5.72, -47.36) * mm, "mid": v(-5.4, -47.45) * mm, "end": v(-5.08, -47.35) * mm});
            skArc(sketch, "E575", {"start": v(-5.08, -47.35) * mm, "mid": v(-4.36, -46.83) * mm, "end": v(-3.66, -46.29) * mm});
            skArc(sketch, "E576", {"start": v(-3.66, -46.29) * mm, "mid": v(-2.66, -45.43) * mm, "end": v(-1.7, -44.53) * mm});
            skArc(sketch, "E577", {"start": v(-1.7, -44.53) * mm, "mid": v(-0.3, -43.16) * mm, "end": v(1.06, -41.77) * mm});
            skArc(sketch, "E578", {"start": v(1.06, -41.77) * mm, "mid": v(2.1, -40.72) * mm, "end": v(3.13, -39.68) * mm});
            skArc(sketch, "E579", {"start": v(3.13, -39.68) * mm, "mid": v(3.54, -39.32) * mm, "end": v(3.98, -39) * mm});
            skArc(sketch, "E580", {"start": v(3.98, -39) * mm, "mid": v(4.2, -38.94) * mm, "end": v(4.41, -39) * mm});
            skArc(sketch, "E581", {"start": v(4.41, -39) * mm, "mid": v(4.59, -39.2) * mm, "end": v(4.68, -39.45) * mm});
            skArc(sketch, "E582", {"start": v(4.68, -39.45) * mm, "mid": v(4.81, -39.96) * mm, "end": v(5.05, -40.43) * mm});
            skArc(sketch, "E583", {"start": v(5.05, -40.43) * mm, "mid": v(5.36, -40.72) * mm, "end": v(5.76, -40.86) * mm});
            skArc(sketch, "E584", {"start": v(5.76, -40.86) * mm, "mid": v(6.12, -40.8) * mm, "end": v(6.4, -40.57) * mm});
            skArc(sketch, "E585", {"start": v(6.4, -40.57) * mm, "mid": v(6.59, -40.15) * mm, "end": v(6.65, -39.7) * mm});
            skArc(sketch, "E586", {"start": v(6.65, -39.7) * mm, "mid": v(6.69, -39.1) * mm, "end": v(6.8, -38.52) * mm});
            skArc(sketch, "E587", {"start": v(6.8, -38.52) * mm, "mid": v(6.98, -37.85) * mm, "end": v(7.22, -37.19) * mm});
            skArc(sketch, "E588", {"start": v(7.22, -37.19) * mm, "mid": v(7.48, -36.6) * mm, "end": v(7.77, -36.04) * mm});
            skArc(sketch, "E589", {"start": v(7.77, -36.04) * mm, "mid": v(7.96, -35.84) * mm, "end": v(8.23, -35.77) * mm});
            skArc(sketch, "E590", {"start": v(8.23, -35.77) * mm, "mid": v(8.57, -35.88) * mm, "end": v(8.77, -36.19) * mm});
            skArc(sketch, "E591", {"start": v(8.77, -36.19) * mm, "mid": v(8.86, -36.76) * mm, "end": v(8.84, -37.33) * mm});
            skArc(sketch, "E592", {"start": v(8.84, -37.33) * mm, "mid": v(8.67, -38.3) * mm, "end": v(8.4, -39.25) * mm});
            skArc(sketch, "E593", {"start": v(8.4, -39.25) * mm, "mid": v(7.94, -40.65) * mm, "end": v(7.42, -42.04) * mm});
            skArc(sketch, "E594", {"start": v(7.42, -42.04) * mm, "mid": v(6.73, -43.85) * mm, "end": v(6.05, -45.66) * mm});
            skArc(sketch, "E595", {"start": v(6.05, -45.66) * mm, "mid": v(5.86, -46.26) * mm, "end": v(5.74, -46.87) * mm});
            skArc(sketch, "E596", {"start": v(5.74, -46.87) * mm, "mid": v(5.78, -47.16) * mm, "end": v(5.97, -47.4) * mm});
            skArc(sketch, "E597", {"start": v(5.97, -47.4) * mm, "mid": v(6.29, -47.56) * mm, "end": v(6.64, -47.62) * mm});
            skArc(sketch, "E598", {"start": v(6.64, -47.62) * mm, "mid": v(6.98, -47.57) * mm, "end": v(7.29, -47.4) * mm});
            skArc(sketch, "E599", {"start": v(7.29, -47.4) * mm, "mid": v(7.55, -47.15) * mm, "end": v(7.74, -46.83) * mm});
            skArc(sketch, "E600", {"start": v(7.74, -46.83) * mm, "mid": v(7.92, -46.33) * mm, "end": v(8.02, -45.81) * mm});
            skArc(sketch, "E601", {"start": v(8.02, -45.81) * mm, "mid": v(8.08, -45.04) * mm, "end": v(8.11, -44.27) * mm});
            skArc(sketch, "E602", {"start": v(8.11, -44.27) * mm, "mid": v(8.13, -44) * mm, "end": v(8.18, -43.73) * mm});
            skArc(sketch, "E603", {"start": v(8.18, -43.73) * mm, "mid": v(8.3, -43.3) * mm, "end": v(8.42, -42.86) * mm});
            skArc(sketch, "E604", {"start": v(8.42, -42.86) * mm, "mid": v(8.58, -42.37) * mm, "end": v(8.76, -41.89) * mm});
            skArc(sketch, "E605", {"start": v(8.76, -41.89) * mm, "mid": v(8.95, -41.4) * mm, "end": v(9.15, -40.92) * mm});
            skLineSegment(sketch, "E606", {"start": v(9.15, -40.92) * mm, "end": v(10.17, -38.6) * mm});
            skLineSegment(sketch, "E607", {"start": v(10.17, -38.6) * mm, "end": v(10.54, -40.28) * mm});
            skArc(sketch, "E608", {"start": v(10.54, -40.28) * mm, "mid": v(10.62, -40.6) * mm, "end": v(10.72, -40.92) * mm});
            skArc(sketch, "E609", {"start": v(10.72, -40.92) * mm, "mid": v(10.84, -41.2) * mm, "end": v(10.97, -41.46) * mm});
            skArc(sketch, "E610", {"start": v(10.97, -41.46) * mm, "mid": v(11.1, -41.66) * mm, "end": v(11.25, -41.84) * mm});
            skArc(sketch, "E611", {"start": v(11.25, -41.84) * mm, "mid": v(11.36, -41.92) * mm, "end": v(11.5, -41.95) * mm});
            skArc(sketch, "E612", {"start": v(11.5, -41.95) * mm, "mid": v(11.87, -42.04) * mm, "end": v(12.16, -42.28) * mm});
            skArc(sketch, "E613", {"start": v(12.16, -42.28) * mm, "mid": v(12.64, -42.94) * mm, "end": v(13.07, -43.63) * mm});
            skArc(sketch, "E614", {"start": v(13.07, -43.63) * mm, "mid": v(13.5, -44.43) * mm, "end": v(13.88, -45.26) * mm});
            skArc(sketch, "E615", {"start": v(13.88, -45.26) * mm, "mid": v(14.16, -46.02) * mm, "end": v(14.36, -46.81) * mm});
            skArc(sketch, "E616", {"start": v(14.36, -46.81) * mm, "mid": v(14.46, -47.21) * mm, "end": v(14.59, -47.6) * mm});
            skArc(sketch, "E617", {"start": v(14.59, -47.6) * mm, "mid": v(14.72, -47.87) * mm, "end": v(14.9, -48.1) * mm});
            skArc(sketch, "E618", {"start": v(14.9, -48.1) * mm, "mid": v(15.12, -48.28) * mm, "end": v(15.37, -48.4) * mm});
            skArc(sketch, "E619", {"start": v(15.37, -48.4) * mm, "mid": v(15.72, -48.5) * mm, "end": v(16.08, -48.56) * mm});
            skArc(sketch, "E620", {"start": v(16.08, -48.56) * mm, "mid": v(16.51, -48.58) * mm, "end": v(16.94, -48.55) * mm});
            skArc(sketch, "E621", {"start": v(16.94, -48.55) * mm, "mid": v(17.21, -48.45) * mm, "end": v(17.42, -48.25) * mm});
            skArc(sketch, "E622", {"start": v(17.42, -48.25) * mm, "mid": v(17.49, -48.03) * mm, "end": v(17.42, -47.81) * mm});
            skArc(sketch, "E623", {"start": v(17.42, -47.81) * mm, "mid": v(17.2, -47.55) * mm, "end": v(16.92, -47.34) * mm});
            skArc(sketch, "E624", {"start": v(16.92, -47.34) * mm, "mid": v(16.4, -46.94) * mm, "end": v(16, -46.45) * mm});
            skArc(sketch, "E625", {"start": v(16, -46.45) * mm, "mid": v(15.24, -45.27) * mm, "end": v(14.51, -44.08) * mm});
            skArc(sketch, "E626", {"start": v(14.51, -44.08) * mm, "mid": v(13.8, -42.84) * mm, "end": v(13.1, -41.58) * mm});
            skArc(sketch, "E627", {"start": v(13.1, -41.58) * mm, "mid": v(13.01, -41.23) * mm, "end": v(13.12, -40.89) * mm});
            skArc(sketch, "E628", {"start": v(13.12, -40.89) * mm, "mid": v(13.16, -40.76) * mm, "end": v(13.15, -40.61) * mm});
            skArc(sketch, "E629", {"start": v(13.15, -40.61) * mm, "mid": v(13.06, -40.4) * mm, "end": v(12.95, -40.21) * mm});
            skArc(sketch, "E630", {"start": v(12.95, -40.21) * mm, "mid": v(12.79, -39.98) * mm, "end": v(12.6, -39.76) * mm});
            skArc(sketch, "E631", {"start": v(12.6, -39.76) * mm, "mid": v(12.36, -39.53) * mm, "end": v(12.1, -39.32) * mm});
            skArc(sketch, "E632", {"start": v(12.1, -39.32) * mm, "mid": v(11.85, -39.1) * mm, "end": v(11.6, -38.85) * mm});
            skArc(sketch, "E633", {"start": v(11.6, -38.85) * mm, "mid": v(11.37, -38.6) * mm, "end": v(11.17, -38.33) * mm});
            skArc(sketch, "E634", {"start": v(11.17, -38.33) * mm, "mid": v(11, -38.08) * mm, "end": v(10.87, -37.82) * mm});
            skArc(sketch, "E635", {"start": v(10.87, -37.82) * mm, "mid": v(10.8, -37.63) * mm, "end": v(10.78, -37.42) * mm});
            skArc(sketch, "E636", {"start": v(10.78, -37.42) * mm, "mid": v(10.82, -36.83) * mm, "end": v(10.96, -36.26) * mm});
            skArc(sketch, "E637", {"start": v(10.96, -36.26) * mm, "mid": v(11.28, -35.3) * mm, "end": v(11.64, -34.34) * mm});
            skArc(sketch, "E638", {"start": v(11.64, -34.34) * mm, "mid": v(12.03, -33.38) * mm, "end": v(12.44, -32.43) * mm});
            skArc(sketch, "E639", {"start": v(12.44, -32.43) * mm, "mid": v(12.6, -32.23) * mm, "end": v(12.85, -32.16) * mm});
            skArc(sketch, "E640", {"start": v(12.85, -32.16) * mm, "mid": v(13.1, -32.22) * mm, "end": v(13.28, -32.4) * mm});
            skArc(sketch, "E641", {"start": v(13.28, -32.4) * mm, "mid": v(13.45, -32.74) * mm, "end": v(13.57, -33.1) * mm});
            skArc(sketch, "E642", {"start": v(13.57, -33.1) * mm, "mid": v(13.64, -33.61) * mm, "end": v(13.66, -34.12) * mm});
            skArc(sketch, "E643", {"start": v(13.66, -34.12) * mm, "mid": v(13.62, -34.7) * mm, "end": v(13.53, -35.26) * mm});
            skArc(sketch, "E644", {"start": v(13.53, -35.26) * mm, "mid": v(13.47, -35.64) * mm, "end": v(13.42, -36.02) * mm});
            skArc(sketch, "E645", {"start": v(13.42, -36.02) * mm, "mid": v(13.41, -36.25) * mm, "end": v(13.46, -36.47) * mm});
            skArc(sketch, "E646", {"start": v(13.46, -36.47) * mm, "mid": v(13.54, -36.6) * mm, "end": v(13.66, -36.7) * mm});
            skArc(sketch, "E647", {"start": v(13.66, -36.7) * mm, "mid": v(13.83, -36.78) * mm, "end": v(14.02, -36.8) * mm});
            skArc(sketch, "E648", {"start": v(14.02, -36.8) * mm, "mid": v(14.18, -36.79) * mm, "end": v(14.34, -36.75) * mm});
            skArc(sketch, "E649", {"start": v(14.34, -36.75) * mm, "mid": v(14.5, -36.7) * mm, "end": v(14.65, -36.6) * mm});
            skArc(sketch, "E650", {"start": v(14.65, -36.6) * mm, "mid": v(14.78, -36.51) * mm, "end": v(14.9, -36.4) * mm});
            skArc(sketch, "E651", {"start": v(14.9, -36.4) * mm, "mid": v(14.98, -36.28) * mm, "end": v(15.04, -36.15) * mm});
            skArc(sketch, "E652", {"start": v(15.04, -36.15) * mm, "mid": v(15.1, -36.04) * mm, "end": v(15.16, -35.94) * mm});
            skArc(sketch, "E653", {"start": v(15.16, -35.94) * mm, "mid": v(15.23, -35.86) * mm, "end": v(15.32, -35.8) * mm});
            skArc(sketch, "E654", {"start": v(15.32, -35.8) * mm, "mid": v(15.41, -35.78) * mm, "end": v(15.5, -35.79) * mm});
            skArc(sketch, "E655", {"start": v(15.5, -35.79) * mm, "mid": v(15.6, -35.82) * mm, "end": v(15.67, -35.88) * mm});
            skArc(sketch, "E656", {"start": v(15.67, -35.88) * mm, "mid": v(15.76, -36) * mm, "end": v(15.79, -36.15) * mm});
            skArc(sketch, "E657", {"start": v(15.79, -36.15) * mm, "mid": v(15.79, -36.47) * mm, "end": v(15.77, -36.79) * mm});
            skArc(sketch, "E658", {"start": v(15.77, -36.79) * mm, "mid": v(15.72, -37.19) * mm, "end": v(15.65, -37.58) * mm});
            skArc(sketch, "E659", {"start": v(15.65, -37.58) * mm, "mid": v(15.55, -38.02) * mm, "end": v(15.44, -38.46) * mm});
            skArc(sketch, "E660", {"start": v(15.44, -38.46) * mm, "mid": v(15.07, -39.77) * mm, "end": v(14.73, -41.1) * mm});
            skArc(sketch, "E661", {"start": v(14.73, -41.1) * mm, "mid": v(14.57, -41.81) * mm, "end": v(14.48, -42.54) * mm});
            skArc(sketch, "E662", {"start": v(14.48, -42.54) * mm, "mid": v(14.49, -42.88) * mm, "end": v(14.58, -43.22) * mm});
            skArc(sketch, "E663", {"start": v(14.58, -43.22) * mm, "mid": v(14.74, -43.38) * mm, "end": v(14.96, -43.4) * mm});
            skArc(sketch, "E664", {"start": v(14.96, -43.4) * mm, "mid": v(15.13, -43.3) * mm, "end": v(15.26, -43.15) * mm});
            skArc(sketch, "E665", {"start": v(15.26, -43.15) * mm, "mid": v(15.42, -42.85) * mm, "end": v(15.56, -42.53) * mm});
            skArc(sketch, "E666", {"start": v(15.56, -42.53) * mm, "mid": v(15.71, -42.12) * mm, "end": v(15.83, -41.7) * mm});
            skArc(sketch, "E667", {"start": v(15.83, -41.7) * mm, "mid": v(15.93, -41.24) * mm, "end": v(16.01, -40.78) * mm});
            skArc(sketch, "E668", {"start": v(16.01, -40.78) * mm, "mid": v(16.18, -39.76) * mm, "end": v(16.37, -38.74) * mm});
            skArc(sketch, "E669", {"start": v(16.37, -38.74) * mm, "mid": v(16.53, -38.27) * mm, "end": v(16.8, -37.86) * mm});
            skArc(sketch, "E670", {"start": v(16.8, -37.86) * mm, "mid": v(17.12, -37.58) * mm, "end": v(17.52, -37.44) * mm});
            skArc(sketch, "E671", {"start": v(17.52, -37.44) * mm, "mid": v(18.2, -37.34) * mm, "end": v(18.88, -37.31) * mm});
            skArc(sketch, "E672", {"start": v(18.88, -37.31) * mm, "mid": v(19.28, -37.3) * mm, "end": v(19.67, -37.25) * mm});
            skArc(sketch, "E673", {"start": v(19.67, -37.25) * mm, "mid": v(20.07, -37.17) * mm, "end": v(20.47, -37.07) * mm});
            skArc(sketch, "E674", {"start": v(20.47, -37.07) * mm, "mid": v(20.84, -36.94) * mm, "end": v(21.19, -36.8) * mm});
            skArc(sketch, "E675", {"start": v(21.19, -36.8) * mm, "mid": v(21.45, -36.65) * mm, "end": v(21.68, -36.47) * mm});
            skArc(sketch, "E676", {"start": v(21.68, -36.47) * mm, "mid": v(21.94, -36.25) * mm, "end": v(22.22, -36.04) * mm});
            skArc(sketch, "E677", {"start": v(22.22, -36.04) * mm, "mid": v(22.4, -35.94) * mm, "end": v(22.6, -35.9) * mm});
            skArc(sketch, "E678", {"start": v(22.6, -35.9) * mm, "mid": v(22.8, -35.92) * mm, "end": v(22.97, -35.99) * mm});
            skArc(sketch, "E679", {"start": v(22.97, -35.99) * mm, "mid": v(23.23, -36.15) * mm, "end": v(23.47, -36.34) * mm});
            skArc(sketch, "E680", {"start": v(23.47, -36.34) * mm, "mid": v(23.72, -36.51) * mm, "end": v(23.99, -36.63) * mm});
            skArc(sketch, "E681", {"start": v(23.99, -36.63) * mm, "mid": v(24.46, -36.79) * mm, "end": v(24.93, -36.92) * mm});
            skArc(sketch, "E682", {"start": v(24.93, -36.92) * mm, "mid": v(25.49, -37.05) * mm, "end": v(26.05, -37.16) * mm});
            skArc(sketch, "E683", {"start": v(26.05, -37.16) * mm, "mid": v(26.63, -37.25) * mm, "end": v(27.22, -37.31) * mm});
            skArc(sketch, "E684", {"start": v(27.22, -37.31) * mm, "mid": v(28.13, -37.4) * mm, "end": v(29.05, -37.51) * mm});
            skArc(sketch, "E685", {"start": v(29.05, -37.51) * mm, "mid": v(29.4, -37.6) * mm, "end": v(29.71, -37.75) * mm});
            skArc(sketch, "E686", {"start": v(29.71, -37.75) * mm, "mid": v(29.91, -37.94) * mm, "end": v(30.02, -38.2) * mm});
            skArc(sketch, "E687", {"start": v(30.02, -38.2) * mm, "mid": v(30.1, -38.65) * mm, "end": v(30.12, -39.12) * mm});
            skArc(sketch, "E688", {"start": v(30.12, -39.12) * mm, "mid": v(30.14, -39.42) * mm, "end": v(30.18, -39.71) * mm});
            skArc(sketch, "E689", {"start": v(30.18, -39.71) * mm, "mid": v(30.23, -39.97) * mm, "end": v(30.32, -40.21) * mm});
            skArc(sketch, "E690", {"start": v(30.32, -40.21) * mm, "mid": v(30.4, -40.4) * mm, "end": v(30.52, -40.55) * mm});
            skArc(sketch, "E691", {"start": v(30.52, -40.55) * mm, "mid": v(30.63, -40.63) * mm, "end": v(30.77, -40.66) * mm});
            skArc(sketch, "E692", {"start": v(30.77, -40.66) * mm, "mid": v(31, -40.63) * mm, "end": v(31.2, -40.55) * mm});
            skArc(sketch, "E693", {"start": v(31.2, -40.55) * mm, "mid": v(31.35, -40.41) * mm, "end": v(31.42, -40.24) * mm});
            skArc(sketch, "E694", {"start": v(31.42, -40.24) * mm, "mid": v(31.46, -39.92) * mm, "end": v(31.44, -39.61) * mm});
            skArc(sketch, "E695", {"start": v(31.44, -39.61) * mm, "mid": v(31.33, -38.97) * mm, "end": v(31.21, -38.33) * mm});
            skArc(sketch, "E696", {"start": v(31.21, -38.33) * mm, "mid": v(31.1, -37.89) * mm, "end": v(30.96, -37.45) * mm});
            skArc(sketch, "E697", {"start": v(30.96, -37.45) * mm, "mid": v(30.81, -37.21) * mm, "end": v(30.6, -37.03) * mm});
            skArc(sketch, "E698", {"start": v(30.6, -37.03) * mm, "mid": v(30.3, -36.9) * mm, "end": v(29.98, -36.84) * mm});
            skArc(sketch, "E699", {"start": v(29.98, -36.84) * mm, "mid": v(29.3, -36.8) * mm, "end": v(28.6, -36.8) * mm});
            skArc(sketch, "E700", {"start": v(28.6, -36.8) * mm, "mid": v(27.15, -36.74) * mm, "end": v(25.7, -36.57) * mm});
            skArc(sketch, "E701", {"start": v(25.7, -36.57) * mm, "mid": v(24.85, -36.3) * mm, "end": v(24.12, -35.8) * mm});
            skArc(sketch, "E702", {"start": v(24.12, -35.8) * mm, "mid": v(23.91, -35.31) * mm, "end": v(24.12, -34.83) * mm});
            skArc(sketch, "E703", {"start": v(24.12, -34.83) * mm, "mid": v(24.82, -34.3) * mm, "end": v(25.62, -33.94) * mm});
            skArc(sketch, "E704", {"start": v(25.62, -33.94) * mm, "mid": v(25.99, -33.8) * mm, "end": v(26.35, -33.66) * mm});
            skArc(sketch, "E705", {"start": v(26.35, -33.66) * mm, "mid": v(26.79, -33.45) * mm, "end": v(27.22, -33.23) * mm});
            skArc(sketch, "E706", {"start": v(27.22, -33.23) * mm, "mid": v(27.65, -33) * mm, "end": v(28.07, -32.74) * mm});
            skArc(sketch, "E707", {"start": v(28.07, -32.74) * mm, "mid": v(28.43, -32.51) * mm, "end": v(28.78, -32.27) * mm});
            skArc(sketch, "E708", {"start": v(28.78, -32.27) * mm, "mid": v(29.08, -32.05) * mm, "end": v(29.39, -31.83) * mm});
            skArc(sketch, "E709", {"start": v(29.39, -31.83) * mm, "mid": v(29.66, -31.65) * mm, "end": v(29.93, -31.46) * mm});
            skArc(sketch, "E710", {"start": v(29.93, -31.46) * mm, "mid": v(30.16, -31.31) * mm, "end": v(30.4, -31.17) * mm});
            skArc(sketch, "E711", {"start": v(30.4, -31.17) * mm, "mid": v(30.46, -31.14) * mm, "end": v(30.53, -31.13) * mm});
            skArc(sketch, "E712", {"start": v(30.53, -31.13) * mm, "mid": v(30.9, -31.21) * mm, "end": v(31.21, -31.45) * mm});
            skArc(sketch, "E713", {"start": v(31.21, -31.45) * mm, "mid": v(33.06, -33.75) * mm, "end": v(34.9, -36.05) * mm});
            skArc(sketch, "E714", {"start": v(34.9, -36.05) * mm, "mid": v(36.62, -38.23) * mm, "end": v(38.32, -40.41) * mm});
            skArc(sketch, "E715", {"start": v(38.32, -40.41) * mm, "mid": v(38.88, -41.26) * mm, "end": v(39.33, -42.17) * mm});
            skArc(sketch, "E716", {"start": v(39.33, -42.17) * mm, "mid": v(39.55, -42.66) * mm, "end": v(39.8, -43.15) * mm});
            skArc(sketch, "E717", {"start": v(39.8, -43.15) * mm, "mid": v(40, -43.43) * mm, "end": v(40.25, -43.67) * mm});
            skArc(sketch, "E718", {"start": v(40.25, -43.67) * mm, "mid": v(40.52, -43.84) * mm, "end": v(40.82, -43.93) * mm});
            skArc(sketch, "E719", {"start": v(40.82, -43.93) * mm, "mid": v(41.25, -44) * mm, "end": v(41.67, -44.01) * mm});
            skArc(sketch, "E720", {"start": v(41.67, -44.01) * mm, "mid": v(42.26, -43.97) * mm, "end": v(42.83, -43.83) * mm});
            skArc(sketch, "E721", {"start": v(42.83, -43.83) * mm, "mid": v(43.08, -43.62) * mm, "end": v(43.14, -43.3) * mm});
            skArc(sketch, "E722", {"start": v(43.14, -43.3) * mm, "mid": v(42.96, -42.8) * mm, "end": v(42.66, -42.37) * mm});
            skArc(sketch, "E723", {"start": v(42.66, -42.37) * mm, "mid": v(41.84, -41.53) * mm, "end": v(41, -40.71) * mm});
            skArc(sketch, "E724", {"start": v(41, -40.71) * mm, "mid": v(40.44, -40.17) * mm, "end": v(39.89, -39.62) * mm});
            skArc(sketch, "E725", {"start": v(39.89, -39.62) * mm, "mid": v(39.1, -38.8) * mm, "end": v(38.33, -37.98) * mm});
            skArc(sketch, "E726", {"start": v(38.33, -37.98) * mm, "mid": v(37.49, -37.07) * mm, "end": v(36.65, -36.16) * mm});
            skArc(sketch, "E727", {"start": v(36.65, -36.16) * mm, "mid": v(35.86, -35.28) * mm, "end": v(35.08, -34.4) * mm});
            skLineSegment(sketch, "E728", {"start": v(35.08, -34.4) * mm, "end": v(31.4, -30.18) * mm});
            skLineSegment(sketch, "E729", {"start": v(31.4, -30.18) * mm, "end": v(32.99, -28.85) * mm});
            skArc(sketch, "E730", {"start": v(32.99, -28.85) * mm, "mid": v(33.3, -28.6) * mm, "end": v(33.62, -28.34) * mm});
            skArc(sketch, "E731", {"start": v(33.62, -28.34) * mm, "mid": v(33.91, -28.12) * mm, "end": v(34.22, -27.91) * mm});
            skArc(sketch, "E732", {"start": v(34.22, -27.91) * mm, "mid": v(34.47, -27.75) * mm, "end": v(34.73, -27.59) * mm});
            skArc(sketch, "E733", {"start": v(34.73, -27.59) * mm, "mid": v(34.84, -27.54) * mm, "end": v(34.96, -27.52) * mm});
            skArc(sketch, "E734", {"start": v(34.96, -27.52) * mm, "mid": v(35.35, -27.61) * mm, "end": v(35.67, -27.87) * mm});
            skArc(sketch, "E735", {"start": v(35.67, -27.87) * mm, "mid": v(37.46, -30.2) * mm, "end": v(39.24, -32.54) * mm});
            skArc(sketch, "E736", {"start": v(39.24, -32.54) * mm, "mid": v(40.93, -34.79) * mm, "end": v(42.6, -37.05) * mm});
            skArc(sketch, "E737", {"start": v(42.6, -37.05) * mm, "mid": v(43, -37.74) * mm, "end": v(43.27, -38.49) * mm});
            skArc(sketch, "E738", {"start": v(43.27, -38.49) * mm, "mid": v(43.35, -38.75) * mm, "end": v(43.48, -39) * mm});
            skArc(sketch, "E739", {"start": v(43.48, -39) * mm, "mid": v(43.63, -39.21) * mm, "end": v(43.82, -39.4) * mm});
            skArc(sketch, "E740", {"start": v(43.82, -39.4) * mm, "mid": v(44.06, -39.54) * mm, "end": v(44.3, -39.65) * mm});
            skArc(sketch, "E741", {"start": v(44.3, -39.65) * mm, "mid": v(44.62, -39.74) * mm, "end": v(44.94, -39.8) * mm});
            skArc(sketch, "E742", {"start": v(44.94, -39.8) * mm, "mid": v(45.21, -39.82) * mm, "end": v(45.48, -39.84) * mm});
            skArc(sketch, "E743", {"start": v(45.48, -39.84) * mm, "mid": v(45.7, -39.84) * mm, "end": v(45.93, -39.83) * mm});
            skArc(sketch, "E744", {"start": v(45.93, -39.83) * mm, "mid": v(46.1, -39.82) * mm, "end": v(46.26, -39.79) * mm});
            skArc(sketch, "E745", {"start": v(46.26, -39.79) * mm, "mid": v(46.32, -39.75) * mm, "end": v(46.34, -39.7) * mm});
            skArc(sketch, "E746", {"start": v(46.34, -39.7) * mm, "mid": v(46.3, -39.32) * mm, "end": v(46.18, -38.97) * mm});
            skArc(sketch, "E747", {"start": v(46.18, -38.97) * mm, "mid": v(45.93, -38.45) * mm, "end": v(45.64, -37.95) * mm});
            skArc(sketch, "E748", {"start": v(45.64, -37.95) * mm, "mid": v(45.33, -37.47) * mm, "end": v(45, -37) * mm});
            skArc(sketch, "E749", {"start": v(45, -37) * mm, "mid": v(44.82, -36.85) * mm, "end": v(44.58, -36.8) * mm});
            skArc(sketch, "E750", {"start": v(44.58, -36.8) * mm, "mid": v(44.4, -36.76) * mm, "end": v(44.24, -36.64) * mm});
            skArc(sketch, "E751", {"start": v(44.24, -36.64) * mm, "mid": v(43.57, -35.9) * mm, "end": v(42.9, -35.17) * mm});
            skArc(sketch, "E752", {"start": v(42.9, -35.17) * mm, "mid": v(42.12, -34.28) * mm, "end": v(41.36, -33.38) * mm});
            skArc(sketch, "E753", {"start": v(41.36, -33.38) * mm, "mid": v(40.5, -32.32) * mm, "end": v(39.65, -31.26) * mm});
            skArc(sketch, "E754", {"start": v(39.65, -31.26) * mm, "mid": v(37.7, -28.81) * mm, "end": v(35.7, -26.4) * mm});
            skArc(sketch, "E755", {"start": v(35.7, -26.4) * mm, "mid": v(34.2, -24.64) * mm, "end": v(32.63, -22.94) * mm});
            skArc(sketch, "E756", {"start": v(32.63, -22.94) * mm, "mid": v(31.4, -21.7) * mm, "end": v(30.1, -20.5) * mm});
            skArc(sketch, "E757", {"start": v(30.1, -20.5) * mm, "mid": v(29.07, -19.67) * mm, "end": v(27.96, -18.94) * mm});
            skLineSegment(sketch, "E758", {"start": v(27.96, -18.94) * mm, "end": v(25.8, -17.67) * mm});
            skLineSegment(sketch, "E759", {"start": v(25.8, -17.67) * mm, "end": v(25.63, -3.4) * mm});
            skArc(sketch, "E760", {"start": v(25.63, -3.4) * mm, "mid": v(25.6, -0.63) * mm, "end": v(25.58, 2.14) * mm});
            skArc(sketch, "E761", {"start": v(25.58, 2.14) * mm, "mid": v(25.57, 4.55) * mm, "end": v(25.57, 6.96) * mm});
            skArc(sketch, "E762", {"start": v(25.57, 6.96) * mm, "mid": v(25.58, 9.03) * mm, "end": v(25.59, 11.1) * mm});
            skArc(sketch, "E763", {"start": v(25.59, 11.1) * mm, "mid": v(25.6, 11.46) * mm, "end": v(25.66, 11.8) * mm});
            skArc(sketch, "E764", {"start": v(25.66, 11.8) * mm, "mid": v(25.71, 11.99) * mm, "end": v(25.8, 12.16) * mm});
            skArc(sketch, "E765", {"start": v(25.8, 12.16) * mm, "mid": v(25.88, 12.29) * mm, "end": v(26, 12.4) * mm});
            skArc(sketch, "E766", {"start": v(26, 12.4) * mm, "mid": v(26.13, 12.47) * mm, "end": v(26.27, 12.5) * mm});
            skArc(sketch, "E767", {"start": v(26.27, 12.5) * mm, "mid": v(26.42, 12.5) * mm, "end": v(26.56, 12.47) * mm});
            skArc(sketch, "E768", {"start": v(26.56, 12.47) * mm, "mid": v(26.71, 12.43) * mm, "end": v(26.86, 12.42) * mm});
            skArc(sketch, "E769", {"start": v(26.86, 12.42) * mm, "mid": v(26.98, 12.46) * mm, "end": v(27.09, 12.53) * mm});
            skArc(sketch, "E770", {"start": v(27.09, 12.53) * mm, "mid": v(27.17, 12.65) * mm, "end": v(27.23, 12.8) * mm});
            skArc(sketch, "E771", {"start": v(27.23, 12.8) * mm, "mid": v(27.26, 13) * mm, "end": v(27.27, 13.21) * mm});
            skArc(sketch, "E772", {"start": v(27.27, 13.21) * mm, "mid": v(27.25, 13.43) * mm, "end": v(27.2, 13.65) * mm});
            skArc(sketch, "E773", {"start": v(27.2, 13.65) * mm, "mid": v(27.13, 13.82) * mm, "end": v(27, 13.97) * mm});
            skArc(sketch, "E774", {"start": v(27, 13.97) * mm, "mid": v(26.86, 14.09) * mm, "end": v(26.69, 14.16) * mm});
            skArc(sketch, "E775", {"start": v(26.69, 14.16) * mm, "mid": v(26.46, 14.2) * mm, "end": v(26.24, 14.23) * mm});
            skArc(sketch, "E776", {"start": v(26.24, 14.23) * mm, "mid": v(25.99, 14.25) * mm, "end": v(25.74, 14.3) * mm});
            skArc(sketch, "E777", {"start": v(25.74, 14.3) * mm, "mid": v(25.56, 14.4) * mm, "end": v(25.43, 14.54) * mm});
            skArc(sketch, "E778", {"start": v(25.43, 14.54) * mm, "mid": v(25.31, 14.75) * mm, "end": v(25.26, 14.98) * mm});
            skArc(sketch, "E779", {"start": v(25.26, 14.98) * mm, "mid": v(25.22, 15.36) * mm, "end": v(25.2, 15.73) * mm});
            skArc(sketch, "E780", {"start": v(25.2, 15.73) * mm, "mid": v(25.23, 16.15) * mm, "end": v(25.3, 16.57) * mm});
            skArc(sketch, "E781", {"start": v(25.3, 16.57) * mm, "mid": v(25.4, 16.86) * mm, "end": v(25.6, 17.1) * mm});
            skArc(sketch, "E782", {"start": v(25.6, 17.1) * mm, "mid": v(25.87, 17.35) * mm, "end": v(26.19, 17.53) * mm});
            skArc(sketch, "E783", {"start": v(26.19, 17.53) * mm, "mid": v(26.79, 17.78) * mm, "end": v(27.4, 18) * mm});
            skArc(sketch, "E784", {"start": v(27.4, 18) * mm, "mid": v(27.92, 18.18) * mm, "end": v(28.44, 18.34) * mm});
            skArc(sketch, "E785", {"start": v(28.44, 18.34) * mm, "mid": v(29.1, 18.53) * mm, "end": v(29.78, 18.7) * mm});
            skArc(sketch, "E786", {"start": v(29.78, 18.7) * mm, "mid": v(30.48, 18.87) * mm, "end": v(31.18, 19.03) * mm});
            skArc(sketch, "E787", {"start": v(31.18, 19.03) * mm, "mid": v(31.8, 19.16) * mm, "end": v(32.42, 19.27) * mm});
            skArc(sketch, "E788", {"start": v(32.42, 19.27) * mm, "mid": v(33.3, 19.43) * mm, "end": v(34.2, 19.6) * mm});
            skArc(sketch, "E789", {"start": v(34.2, 19.6) * mm, "mid": v(34.24, 19.65) * mm, "end": v(34.2, 19.7) * mm});
            skArc(sketch, "E790", {"start": v(34.2, 19.7) * mm, "mid": v(33.92, 19.76) * mm, "end": v(33.64, 19.78) * mm});
            skArc(sketch, "E791", {"start": v(33.64, 19.78) * mm, "mid": v(31.92, 19.8) * mm, "end": v(30.2, 19.83) * mm});
            skArc(sketch, "E792", {"start": v(30.2, 19.83) * mm, "mid": v(28.22, 19.87) * mm, "end": v(26.24, 19.94) * mm});
            skArc(sketch, "E793", {"start": v(26.24, 19.94) * mm, "mid": v(25.8, 20.07) * mm, "end": v(25.46, 20.4) * mm});
            skArc(sketch, "E794", {"start": v(25.46, 20.4) * mm, "mid": v(25.45, 20.7) * mm, "end": v(25.7, 20.86) * mm});
            skArc(sketch, "E795", {"start": v(25.7, 20.86) * mm, "mid": v(27.6, 20.95) * mm, "end": v(29.5, 21) * mm});
            skArc(sketch, "E796", {"start": v(29.5, 21) * mm, "mid": v(30.16, 21.01) * mm, "end": v(30.84, 21.04) * mm});
            skArc(sketch, "E797", {"start": v(30.84, 21.04) * mm, "mid": v(31.28, 21.06) * mm, "end": v(31.73, 21.1) * mm});
            skArc(sketch, "E798", {"start": v(31.73, 21.1) * mm, "mid": v(31.84, 21.14) * mm, "end": v(31.93, 21.2) * mm});
            skArc(sketch, "E799", {"start": v(31.93, 21.2) * mm, "mid": v(31.95, 21.24) * mm, "end": v(31.9, 21.28) * mm});
            skArc(sketch, "E800", {"start": v(31.9, 21.28) * mm, "mid": v(30.65, 21.52) * mm, "end": v(29.4, 21.81) * mm});
            skArc(sketch, "E801", {"start": v(29.4, 21.81) * mm, "mid": v(28.3, 22.14) * mm, "end": v(27.22, 22.55) * mm});
            skArc(sketch, "E802", {"start": v(27.22, 22.55) * mm, "mid": v(26.4, 22.92) * mm, "end": v(25.6, 23.35) * mm});
            skArc(sketch, "E803", {"start": v(25.6, 23.35) * mm, "mid": v(25.32, 23.64) * mm, "end": v(25.2, 24.05) * mm});
            skArc(sketch, "E804", {"start": v(25.2, 24.05) * mm, "mid": v(25.22, 24.23) * mm, "end": v(25.26, 24.41) * mm});
            skArc(sketch, "E805", {"start": v(25.26, 24.41) * mm, "mid": v(25.31, 24.59) * mm, "end": v(25.4, 24.76) * mm});
            skArc(sketch, "E806", {"start": v(25.4, 24.76) * mm, "mid": v(25.5, 24.9) * mm, "end": v(25.6, 25.03) * mm});
            skArc(sketch, "E807", {"start": v(25.6, 25.03) * mm, "mid": v(25.72, 25.12) * mm, "end": v(25.85, 25.18) * mm});
            skArc(sketch, "E808", {"start": v(25.85, 25.18) * mm, "mid": v(25.97, 25.24) * mm, "end": v(26.08, 25.33) * mm});
            skArc(sketch, "E809", {"start": v(26.08, 25.33) * mm, "mid": v(26.13, 25.43) * mm, "end": v(26.13, 25.55) * mm});
            skArc(sketch, "E810", {"start": v(26.13, 25.55) * mm, "mid": v(26.08, 25.7) * mm, "end": v(25.98, 25.85) * mm});
            skArc(sketch, "E811", {"start": v(25.98, 25.85) * mm, "mid": v(25.8, 26.07) * mm, "end": v(25.6, 26.29) * mm});
            skArc(sketch, "E812", {"start": v(25.6, 26.29) * mm, "mid": v(25.32, 26.54) * mm, "end": v(25.04, 26.79) * mm});
            skArc(sketch, "E813", {"start": v(25.04, 26.79) * mm, "mid": v(24.93, 26.82) * mm, "end": v(24.82, 26.77) * mm});
            skArc(sketch, "E814", {"start": v(24.82, 26.77) * mm, "mid": v(24.74, 26.62) * mm, "end": v(24.7, 26.45) * mm});
            skArc(sketch, "E815", {"start": v(24.7, 26.45) * mm, "mid": v(24.7, 25.8) * mm, "end": v(24.7, 25.16) * mm});
            skArc(sketch, "E816", {"start": v(24.7, 25.16) * mm, "mid": v(24.68, 24.54) * mm, "end": v(24.62, 23.91) * mm});
            skArc(sketch, "E817", {"start": v(24.62, 23.91) * mm, "mid": v(24.54, 23.6) * mm, "end": v(24.36, 23.3) * mm});
            skArc(sketch, "E818", {"start": v(24.36, 23.3) * mm, "mid": v(24.09, 23.06) * mm, "end": v(23.76, 22.89) * mm});
            skArc(sketch, "E819", {"start": v(23.76, 22.89) * mm, "mid": v(23, 22.6) * mm, "end": v(22.24, 22.35) * mm});
            skArc(sketch, "E820", {"start": v(22.24, 22.35) * mm, "mid": v(21.77, 22.2) * mm, "end": v(21.3, 22.05) * mm});
            skArc(sketch, "E821", {"start": v(21.3, 22.05) * mm, "mid": v(20.9, 21.93) * mm, "end": v(20.48, 21.82) * mm});
            skArc(sketch, "E822", {"start": v(20.48, 21.82) * mm, "mid": v(20.13, 21.72) * mm, "end": v(19.78, 21.63) * mm});
            skArc(sketch, "E823", {"start": v(19.78, 21.63) * mm, "mid": v(19.73, 21.63) * mm, "end": v(19.69, 21.65) * mm});
            skArc(sketch, "E824", {"start": v(19.69, 21.65) * mm, "mid": v(19.66, 21.69) * mm, "end": v(19.66, 21.73) * mm});
            skArc(sketch, "E825", {"start": v(19.66, 21.73) * mm, "mid": v(19.67, 21.88) * mm, "end": v(19.7, 22.03) * mm});
            skArc(sketch, "E826", {"start": v(19.7, 22.03) * mm, "mid": v(19.72, 22.22) * mm, "end": v(19.76, 22.4) * mm});
            skArc(sketch, "E827", {"start": v(19.76, 22.4) * mm, "mid": v(19.8, 22.61) * mm, "end": v(19.86, 22.82) * mm});
            skArc(sketch, "E828", {"start": v(19.86, 22.82) * mm, "mid": v(19.94, 23.06) * mm, "end": v(20.05, 23.3) * mm});
            skArc(sketch, "E829", {"start": v(20.05, 23.3) * mm, "mid": v(20.16, 23.46) * mm, "end": v(20.3, 23.58) * mm});
            skArc(sketch, "E830", {"start": v(20.3, 23.58) * mm, "mid": v(20.48, 23.66) * mm, "end": v(20.67, 23.7) * mm});
            skArc(sketch, "E831", {"start": v(20.67, 23.7) * mm, "mid": v(20.9, 23.68) * mm, "end": v(21.13, 23.64) * mm});
            skArc(sketch, "E832", {"start": v(21.13, 23.64) * mm, "mid": v(21.51, 23.58) * mm, "end": v(21.9, 23.58) * mm});
            skArc(sketch, "E833", {"start": v(21.9, 23.58) * mm, "mid": v(22.06, 23.68) * mm, "end": v(22.08, 23.87) * mm});
            skArc(sketch, "E834", {"start": v(22.08, 23.87) * mm, "mid": v(21.9, 24.17) * mm, "end": v(21.62, 24.4) * mm});
            skArc(sketch, "E835", {"start": v(21.62, 24.4) * mm, "mid": v(21.12, 24.7) * mm, "end": v(20.59, 24.96) * mm});
            skArc(sketch, "E836", {"start": v(20.59, 24.96) * mm, "mid": v(20.2, 25.15) * mm, "end": v(19.85, 25.38) * mm});
            skArc(sketch, "E837", {"start": v(19.85, 25.38) * mm, "mid": v(19.57, 25.6) * mm, "end": v(19.32, 25.88) * mm});
            skArc(sketch, "E838", {"start": v(19.32, 25.88) * mm, "mid": v(19.12, 26.2) * mm, "end": v(18.97, 26.54) * mm});
            skArc(sketch, "E839", {"start": v(18.97, 26.54) * mm, "mid": v(18.83, 26.97) * mm, "end": v(18.72, 27.4) * mm});
            skArc(sketch, "E840", {"start": v(18.72, 27.4) * mm, "mid": v(18.6, 28.26) * mm, "end": v(18.58, 29.12) * mm});
            skArc(sketch, "E841", {"start": v(18.58, 29.12) * mm, "mid": v(18.63, 30.24) * mm, "end": v(18.73, 31.35) * mm});
            skArc(sketch, "E842", {"start": v(18.73, 31.35) * mm, "mid": v(18.87, 32.4) * mm, "end": v(19.04, 33.46) * mm});
            skArc(sketch, "E843", {"start": v(19.04, 33.46) * mm, "mid": v(19.2, 33.71) * mm, "end": v(19.47, 33.81) * mm});
            skArc(sketch, "E844", {"start": v(19.47, 33.81) * mm, "mid": v(19.58, 33.79) * mm, "end": v(19.67, 33.72) * mm});
            skArc(sketch, "E845", {"start": v(19.67, 33.72) * mm, "mid": v(19.88, 33.49) * mm, "end": v(20.08, 33.24) * mm});
            skArc(sketch, "E846", {"start": v(20.08, 33.24) * mm, "mid": v(20.32, 32.94) * mm, "end": v(20.55, 32.62) * mm});
            skArc(sketch, "E847", {"start": v(20.55, 32.62) * mm, "mid": v(20.79, 32.25) * mm, "end": v(21.02, 31.88) * mm});
            skArc(sketch, "E848", {"start": v(21.02, 31.88) * mm, "mid": v(21.31, 31.4) * mm, "end": v(21.6, 30.94) * mm});
            skArc(sketch, "E849", {"start": v(21.6, 30.94) * mm, "mid": v(21.72, 30.8) * mm, "end": v(21.86, 30.66) * mm});
            skArc(sketch, "E850", {"start": v(21.86, 30.66) * mm, "mid": v(21.93, 30.66) * mm, "end": v(21.96, 30.72) * mm});
            skArc(sketch, "E851", {"start": v(21.96, 30.72) * mm, "mid": v(21.91, 30.98) * mm, "end": v(21.86, 31.23) * mm});
            skArc(sketch, "E852", {"start": v(21.86, 31.23) * mm, "mid": v(21.58, 32.37) * mm, "end": v(21.34, 33.51) * mm});
            skArc(sketch, "E853", {"start": v(21.34, 33.51) * mm, "mid": v(21.33, 33.97) * mm, "end": v(21.5, 34.4) * mm});
            skArc(sketch, "E854", {"start": v(21.5, 34.4) * mm, "mid": v(21.8, 34.78) * mm, "end": v(22.22, 35.06) * mm});
            skArc(sketch, "E855", {"start": v(22.22, 35.06) * mm, "mid": v(23.58, 35.7) * mm, "end": v(24.95, 36.33) * mm});
            skArc(sketch, "E856", {"start": v(24.95, 36.33) * mm, "mid": v(27.16, 37.39) * mm, "end": v(29.33, 38.55) * mm});
            skArc(sketch, "E857", {"start": v(29.33, 38.55) * mm, "mid": v(30.9, 39.57) * mm, "end": v(32.35, 40.75) * mm});
            skArc(sketch, "E858", {"start": v(32.35, 40.75) * mm, "mid": v(33.28, 41.73) * mm, "end": v(34.03, 42.85) * mm});
            skArc(sketch, "E859", {"start": v(34.03, 42.85) * mm, "mid": v(34.35, 43.8) * mm, "end": v(34.3, 44.8) * mm});
            skArc(sketch, "E860", {"start": v(34.3, 44.8) * mm, "mid": v(34.2, 45.06) * mm, "end": v(34.08, 45.3) * mm});
            skArc(sketch, "E861", {"start": v(34.08, 45.3) * mm, "mid": v(33.89, 45.58) * mm, "end": v(33.67, 45.84) * mm});
            skArc(sketch, "E862", {"start": v(33.67, 45.84) * mm, "mid": v(33.43, 46.08) * mm, "end": v(33.16, 46.3) * mm});
            skArc(sketch, "E863", {"start": v(33.16, 46.3) * mm, "mid": v(32.89, 46.49) * mm, "end": v(32.6, 46.64) * mm});
            skArc(sketch, "E864", {"start": v(32.6, 46.64) * mm, "mid": v(31.53, 47.03) * mm, "end": v(30.4, 47.24) * mm});
            skArc(sketch, "E865", {"start": v(30.4, 47.24) * mm, "mid": v(28.53, 47.4) * mm, "end": v(26.65, 47.48) * mm});
            skArc(sketch, "E866", {"start": v(26.65, 47.48) * mm, "mid": v(24.62, 47.49) * mm, "end": v(22.59, 47.41) * mm});
            skArc(sketch, "E867", {"start": v(22.59, 47.41) * mm, "mid": v(20.84, 47.25) * mm, "end": v(19.1, 46.98) * mm});
            skArc(sketch, "E868", {"start": v(24.43, 20.41) * mm, "mid": v(24.45, 20.29) * mm, "end": v(24.37, 20.2) * mm});
            skArc(sketch, "E869", {"start": v(24.37, 20.2) * mm, "mid": v(24.1, 20.1) * mm, "end": v(23.83, 20.03) * mm});
            skArc(sketch, "E870", {"start": v(23.83, 20.03) * mm, "mid": v(23.37, 19.96) * mm, "end": v(22.91, 19.93) * mm});
            skArc(sketch, "E871", {"start": v(22.91, 19.93) * mm, "mid": v(22.26, 19.9) * mm, "end": v(21.6, 19.9) * mm});
            skArc(sketch, "E872", {"start": v(21.6, 19.9) * mm, "mid": v(20.94, 19.9) * mm, "end": v(20.29, 19.93) * mm});
            skArc(sketch, "E873", {"start": v(20.29, 19.93) * mm, "mid": v(19.83, 19.96) * mm, "end": v(19.37, 20.03) * mm});
            skArc(sketch, "E874", {"start": v(19.37, 20.03) * mm, "mid": v(19.1, 20.1) * mm, "end": v(18.83, 20.2) * mm});
            skArc(sketch, "E875", {"start": v(18.83, 20.2) * mm, "mid": v(18.75, 20.29) * mm, "end": v(18.77, 20.41) * mm});
            skArc(sketch, "E876", {"start": v(18.77, 20.41) * mm, "mid": v(18.88, 20.54) * mm, "end": v(19.03, 20.61) * mm});
            skArc(sketch, "E877", {"start": v(19.03, 20.61) * mm, "mid": v(19.38, 20.7) * mm, "end": v(19.73, 20.77) * mm});
            skArc(sketch, "E878", {"start": v(19.73, 20.77) * mm, "mid": v(20.17, 20.84) * mm, "end": v(20.61, 20.89) * mm});
            skArc(sketch, "E879", {"start": v(20.61, 20.89) * mm, "mid": v(21.1, 20.92) * mm, "end": v(21.6, 20.93) * mm});
            skArc(sketch, "E880", {"start": v(21.6, 20.93) * mm, "mid": v(22.1, 20.92) * mm, "end": v(22.59, 20.89) * mm});
            skArc(sketch, "E881", {"start": v(22.59, 20.89) * mm, "mid": v(23.03, 20.84) * mm, "end": v(23.47, 20.77) * mm});
            skArc(sketch, "E882", {"start": v(23.47, 20.77) * mm, "mid": v(23.82, 20.7) * mm, "end": v(24.17, 20.61) * mm});
            skArc(sketch, "E883", {"start": v(24.17, 20.61) * mm, "mid": v(24.32, 20.54) * mm, "end": v(24.43, 20.41) * mm});
            skArc(sketch, "E884", {"start": v(23.45, 17.72) * mm, "mid": v(23.85, 17.47) * mm, "end": v(24.19, 17.14) * mm});
            skArc(sketch, "E885", {"start": v(24.19, 17.14) * mm, "mid": v(24.46, 16.71) * mm, "end": v(24.64, 16.24) * mm});
            skArc(sketch, "E886", {"start": v(24.64, 16.24) * mm, "mid": v(24.73, 15.77) * mm, "end": v(24.71, 15.3) * mm});
            skArc(sketch, "E887", {"start": v(24.71, 15.3) * mm, "mid": v(24.6, 14.9) * mm, "end": v(24.35, 14.57) * mm});
            skArc(sketch, "E888", {"start": v(24.35, 14.57) * mm, "mid": v(24.25, 14.42) * mm, "end": v(24.22, 14.25) * mm});
            skArc(sketch, "E889", {"start": v(24.22, 14.25) * mm, "mid": v(24.18, 12) * mm, "end": v(24.15, 9.75) * mm});
            skArc(sketch, "E890", {"start": v(24.15, 9.75) * mm, "mid": v(24.12, 7.19) * mm, "end": v(24.11, 4.63) * mm});
            skArc(sketch, "E891", {"start": v(24.11, 4.63) * mm, "mid": v(24.11, 1.62) * mm, "end": v(24.13, -1.39) * mm});
            skLineSegment(sketch, "E892", {"start": v(24.13, -1.39) * mm, "end": v(24.25, -17) * mm});
            skLineSegment(sketch, "E893", {"start": v(24.25, -17) * mm, "end": v(22.54, -18.88) * mm});
            skArc(sketch, "E894", {"start": v(22.54, -18.88) * mm, "mid": v(22.09, -19.35) * mm, "end": v(21.62, -19.81) * mm});
            skArc(sketch, "E895", {"start": v(21.62, -19.81) * mm, "mid": v(21.32, -20.06) * mm, "end": v(20.99, -20.27) * mm});
            skArc(sketch, "E896", {"start": v(20.99, -20.27) * mm, "mid": v(20.73, -20.36) * mm, "end": v(20.46, -20.4) * mm});
            skArc(sketch, "E897", {"start": v(20.46, -20.4) * mm, "mid": v(20.18, -20.35) * mm, "end": v(19.92, -20.24) * mm});
            skArc(sketch, "E898", {"start": v(19.92, -20.24) * mm, "mid": v(19.57, -19.92) * mm, "end": v(19.4, -19.48) * mm});
            skArc(sketch, "E899", {"start": v(19.4, -19.48) * mm, "mid": v(19.25, -18.39) * mm, "end": v(19.16, -17.29) * mm});
            skArc(sketch, "E900", {"start": v(19.16, -17.29) * mm, "mid": v(19.08, -15.28) * mm, "end": v(19.05, -13.27) * mm});
            skArc(sketch, "E901", {"start": v(19.05, -13.27) * mm, "mid": v(19.03, -8.37) * mm, "end": v(19.02, -3.47) * mm});
            skArc(sketch, "E902", {"start": v(19.02, -3.47) * mm, "mid": v(19.03, 1.95) * mm, "end": v(19.04, 7.37) * mm});
            skArc(sketch, "E903", {"start": v(19.04, 7.37) * mm, "mid": v(19.07, 9.04) * mm, "end": v(19.16, 10.71) * mm});
            skArc(sketch, "E904", {"start": v(19.16, 10.71) * mm, "mid": v(19.26, 11.46) * mm, "end": v(19.46, 12.18) * mm});
            skArc(sketch, "E905", {"start": v(19.46, 12.18) * mm, "mid": v(19.7, 12.47) * mm, "end": v(20.1, 12.52) * mm});
            skArc(sketch, "E906", {"start": v(20.1, 12.52) * mm, "mid": v(20.35, 12.46) * mm, "end": v(20.61, 12.42) * mm});
            skArc(sketch, "E907", {"start": v(20.61, 12.42) * mm, "mid": v(20.74, 12.42) * mm, "end": v(20.87, 12.47) * mm});
            skArc(sketch, "E908", {"start": v(20.87, 12.47) * mm, "mid": v(20.94, 12.55) * mm, "end": v(20.96, 12.66) * mm});
            skArc(sketch, "E909", {"start": v(20.96, 12.66) * mm, "mid": v(20.92, 12.84) * mm, "end": v(20.87, 13.02) * mm});
            skArc(sketch, "E910", {"start": v(20.87, 13.02) * mm, "mid": v(20.8, 13.18) * mm, "end": v(20.75, 13.35) * mm});
            skArc(sketch, "E911", {"start": v(20.75, 13.35) * mm, "mid": v(20.7, 13.53) * mm, "end": v(20.66, 13.7) * mm});
            skArc(sketch, "E912", {"start": v(20.66, 13.7) * mm, "mid": v(20.62, 13.87) * mm, "end": v(20.59, 14.03) * mm});
            skArc(sketch, "E913", {"start": v(20.59, 14.03) * mm, "mid": v(20.57, 14.15) * mm, "end": v(20.57, 14.27) * mm});
            skArc(sketch, "E914", {"start": v(20.57, 14.27) * mm, "mid": v(20.55, 14.37) * mm, "end": v(20.5, 14.45) * mm});
            skArc(sketch, "E915", {"start": v(20.5, 14.45) * mm, "mid": v(20.39, 14.54) * mm, "end": v(20.27, 14.6) * mm});
            skArc(sketch, "E916", {"start": v(20.27, 14.6) * mm, "mid": v(20.1, 14.67) * mm, "end": v(19.93, 14.7) * mm});
            skArc(sketch, "E917", {"start": v(19.93, 14.7) * mm, "mid": v(19.74, 14.73) * mm, "end": v(19.54, 14.74) * mm});
            skArc(sketch, "E918", {"start": v(19.54, 14.74) * mm, "mid": v(19.27, 14.77) * mm, "end": v(19.01, 14.84) * mm});
            skArc(sketch, "E919", {"start": v(19.01, 14.84) * mm, "mid": v(18.83, 14.96) * mm, "end": v(18.7, 15.14) * mm});
            skArc(sketch, "E920", {"start": v(18.7, 15.14) * mm, "mid": v(18.6, 15.42) * mm, "end": v(18.55, 15.71) * mm});
            skArc(sketch, "E921", {"start": v(18.55, 15.71) * mm, "mid": v(18.52, 16.29) * mm, "end": v(18.5, 16.86) * mm});
            skLineSegment(sketch, "E922", {"start": v(18.5, 16.86) * mm, "end": v(18.5, 18.98) * mm});
            skLineSegment(sketch, "E923", {"start": v(18.5, 18.98) * mm, "end": v(20.36, 18.63) * mm});
            skArc(sketch, "E924", {"start": v(20.36, 18.63) * mm, "mid": v(20.76, 18.55) * mm, "end": v(21.16, 18.46) * mm});
            skArc(sketch, "E925", {"start": v(21.16, 18.46) * mm, "mid": v(21.6, 18.34) * mm, "end": v(22.03, 18.22) * mm});
            skArc(sketch, "E926", {"start": v(22.03, 18.22) * mm, "mid": v(22.44, 18.1) * mm, "end": v(22.84, 17.96) * mm});
            skArc(sketch, "E927", {"start": v(22.84, 17.96) * mm, "mid": v(23.15, 17.85) * mm, "end": v(23.45, 17.72) * mm});
            skArc(sketch, "E928", {"start": v(-15.5, 7.01) * mm, "mid": v(-15.52, 6.81) * mm, "end": v(-15.57, 6.61) * mm});
            skArc(sketch, "E929", {"start": v(-15.57, 6.61) * mm, "mid": v(-15.64, 6.44) * mm, "end": v(-15.73, 6.28) * mm});
            skArc(sketch, "E930", {"start": v(-15.73, 6.28) * mm, "mid": v(-15.85, 6.16) * mm, "end": v(-15.99, 6.06) * mm});
            skArc(sketch, "E931", {"start": v(-15.99, 6.06) * mm, "mid": v(-16.13, 6) * mm, "end": v(-16.28, 5.98) * mm});
            skArc(sketch, "E932", {"start": v(-16.28, 5.98) * mm, "mid": v(-16.55, 6) * mm, "end": v(-16.8, 6.09) * mm});
            skArc(sketch, "E933", {"start": v(-16.8, 6.09) * mm, "mid": v(-16.95, 6.2) * mm, "end": v(-17.02, 6.39) * mm});
            skArc(sketch, "E934", {"start": v(-17.02, 6.39) * mm, "mid": v(-17, 6.62) * mm, "end": v(-16.91, 6.84) * mm});
            skArc(sketch, "E935", {"start": v(-16.91, 6.84) * mm, "mid": v(-16.69, 7.14) * mm, "end": v(-16.44, 7.42) * mm});
            skArc(sketch, "E936", {"start": v(-16.44, 7.42) * mm, "mid": v(-16.16, 7.69) * mm, "end": v(-15.88, 7.94) * mm});
            skArc(sketch, "E937", {"start": v(-15.88, 7.94) * mm, "mid": v(-15.78, 8) * mm, "end": v(-15.66, 7.98) * mm});
            skArc(sketch, "E938", {"start": v(-15.66, 7.98) * mm, "mid": v(-15.57, 7.9) * mm, "end": v(-15.53, 7.8) * mm});
            skArc(sketch, "E939", {"start": v(-15.53, 7.8) * mm, "mid": v(-15.51, 7.4) * mm, "end": v(-15.5, 7.01) * mm});
            skArc(sketch, "E940", {"start": v(-15.28, 1.28) * mm, "mid": v(-15.2, 0.46) * mm, "end": v(-15.16, -0.35) * mm});
            skArc(sketch, "E941", {"start": v(-15.16, -0.35) * mm, "mid": v(-15.14, -0.98) * mm, "end": v(-15.15, -1.6) * mm});
            skArc(sketch, "E942", {"start": v(-15.15, -1.6) * mm, "mid": v(-15.19, -2.06) * mm, "end": v(-15.25, -2.51) * mm});
            skArc(sketch, "E943", {"start": v(-15.25, -2.51) * mm, "mid": v(-15.32, -2.75) * mm, "end": v(-15.47, -2.95) * mm});
            skArc(sketch, "E944", {"start": v(-15.47, -2.95) * mm, "mid": v(-15.6, -3.1) * mm, "end": v(-15.68, -3.26) * mm});
            skArc(sketch, "E945", {"start": v(-15.68, -3.26) * mm, "mid": v(-15.78, -3.5) * mm, "end": v(-15.86, -3.75) * mm});
            skArc(sketch, "E946", {"start": v(-15.86, -3.75) * mm, "mid": v(-15.93, -4.03) * mm, "end": v(-15.98, -4.32) * mm});
            skArc(sketch, "E947", {"start": v(-15.98, -4.32) * mm, "mid": v(-16.01, -4.6) * mm, "end": v(-16.02, -4.89) * mm});
            skArc(sketch, "E948", {"start": v(-16.02, -4.89) * mm, "mid": v(-16.04, -5.19) * mm, "end": v(-16.08, -5.48) * mm});
            skArc(sketch, "E949", {"start": v(-16.08, -5.48) * mm, "mid": v(-16.16, -5.74) * mm, "end": v(-16.27, -5.98) * mm});
            skArc(sketch, "E950", {"start": v(-16.27, -5.98) * mm, "mid": v(-16.4, -6.18) * mm, "end": v(-16.55, -6.35) * mm});
            skArc(sketch, "E951", {"start": v(-16.55, -6.35) * mm, "mid": v(-16.73, -6.48) * mm, "end": v(-16.93, -6.57) * mm});
            skArc(sketch, "E952", {"start": v(-16.93, -6.57) * mm, "mid": v(-17.13, -6.65) * mm, "end": v(-17.33, -6.73) * mm});
            skArc(sketch, "E953", {"start": v(-17.33, -6.73) * mm, "mid": v(-17.58, -6.85) * mm, "end": v(-17.82, -6.97) * mm});
            skArc(sketch, "E954", {"start": v(-17.82, -6.97) * mm, "mid": v(-18.06, -7.1) * mm, "end": v(-18.3, -7.25) * mm});
            skArc(sketch, "E955", {"start": v(-18.3, -7.25) * mm, "mid": v(-18.5, -7.38) * mm, "end": v(-18.7, -7.51) * mm});
            skArc(sketch, "E956", {"start": v(-18.7, -7.51) * mm, "mid": v(-18.94, -7.67) * mm, "end": v(-19.2, -7.8) * mm});
            skArc(sketch, "E957", {"start": v(-19.2, -7.8) * mm, "mid": v(-19.4, -7.85) * mm, "end": v(-19.6, -7.85) * mm});
            skArc(sketch, "E958", {"start": v(-19.6, -7.85) * mm, "mid": v(-19.83, -7.78) * mm, "end": v(-20.03, -7.67) * mm});
            skArc(sketch, "E959", {"start": v(-20.03, -7.67) * mm, "mid": v(-20.33, -7.45) * mm, "end": v(-20.61, -7.2) * mm});
            skArc(sketch, "E960", {"start": v(-20.61, -7.2) * mm, "mid": v(-21.06, -6.87) * mm, "end": v(-21.55, -6.63) * mm});
            skArc(sketch, "E961", {"start": v(-21.55, -6.63) * mm, "mid": v(-21.98, -6.54) * mm, "end": v(-22.41, -6.6) * mm});
            skArc(sketch, "E962", {"start": v(-22.41, -6.6) * mm, "mid": v(-22.77, -6.8) * mm, "end": v(-23.02, -7.13) * mm});
            skArc(sketch, "E963", {"start": v(-23.02, -7.13) * mm, "mid": v(-23.18, -7.6) * mm, "end": v(-23.24, -8.1) * mm});
            skArc(sketch, "E964", {"start": v(-23.24, -8.1) * mm, "mid": v(-23.3, -8.5) * mm, "end": v(-23.48, -8.88) * mm});
            skArc(sketch, "E965", {"start": v(-23.48, -8.88) * mm, "mid": v(-23.82, -9.31) * mm, "end": v(-24.21, -9.7) * mm});
            skArc(sketch, "E966", {"start": v(-24.21, -9.7) * mm, "mid": v(-24.67, -10.03) * mm, "end": v(-25.17, -10.3) * mm});
            skArc(sketch, "E967", {"start": v(-25.17, -10.3) * mm, "mid": v(-25.62, -10.46) * mm, "end": v(-26.1, -10.51) * mm});
            skArc(sketch, "E968", {"start": v(-26.1, -10.51) * mm, "mid": v(-26.16, -10.49) * mm, "end": v(-26.2, -10.42) * mm});
            skArc(sketch, "E969", {"start": v(-26.2, -10.42) * mm, "mid": v(-26.23, -9.68) * mm, "end": v(-26.26, -8.94) * mm});
            skArc(sketch, "E970", {"start": v(-26.26, -8.94) * mm, "mid": v(-26.3, -8.07) * mm, "end": v(-26.32, -7.2) * mm});
            skArc(sketch, "E971", {"start": v(-26.32, -7.2) * mm, "mid": v(-26.33, -6.18) * mm, "end": v(-26.33, -5.15) * mm});
            skLineSegment(sketch, "E972", {"start": v(-26.33, -5.15) * mm, "end": v(-26.33, 0.2) * mm});
            skLineSegment(sketch, "E973", {"start": v(-26.33, 0.2) * mm, "end": v(-23.11, 0.58) * mm});
            skArc(sketch, "E974", {"start": v(-23.11, 0.58) * mm, "mid": v(-21.66, 0.77) * mm, "end": v(-20.2, 1) * mm});
            skArc(sketch, "E975", {"start": v(-20.2, 1) * mm, "mid": v(-19.43, 1.18) * mm, "end": v(-18.68, 1.48) * mm});
            skArc(sketch, "E976", {"start": v(-18.68, 1.48) * mm, "mid": v(-18.2, 1.8) * mm, "end": v(-17.82, 2.22) * mm});
            skArc(sketch, "E977", {"start": v(-17.82, 2.22) * mm, "mid": v(-17.51, 2.77) * mm, "end": v(-17.32, 3.37) * mm});
            skArc(sketch, "E978", {"start": v(-17.32, 3.37) * mm, "mid": v(-17.1, 4.1) * mm, "end": v(-16.8, 4.8) * mm});
            skArc(sketch, "E979", {"start": v(-16.8, 4.8) * mm, "mid": v(-16.53, 5) * mm, "end": v(-16.2, 4.88) * mm});
            skArc(sketch, "E980", {"start": v(-16.2, 4.88) * mm, "mid": v(-15.84, 4.38) * mm, "end": v(-15.64, 3.78) * mm});
            skArc(sketch, "E981", {"start": v(-15.64, 3.78) * mm, "mid": v(-15.43, 2.53) * mm, "end": v(-15.28, 1.28) * mm});
            skArc(sketch, "E982", {"start": v(-11.15, 1.56) * mm, "mid": v(-10.9, 1.15) * mm, "end": v(-10.65, 0.73) * mm});
            skArc(sketch, "E983", {"start": v(-10.65, 0.73) * mm, "mid": v(-10.56, 0.51) * mm, "end": v(-10.53, 0.28) * mm});
            skArc(sketch, "E984", {"start": v(-10.53, 0.28) * mm, "mid": v(-10.57, 0.06) * mm, "end": v(-10.66, -0.13) * mm});
            skArc(sketch, "E985", {"start": v(-10.66, -0.13) * mm, "mid": v(-10.9, -0.45) * mm, "end": v(-11.15, -0.74) * mm});
            skArc(sketch, "E986", {"start": v(-11.15, -0.74) * mm, "mid": v(-11.48, -1.2) * mm, "end": v(-11.72, -1.7) * mm});
            skArc(sketch, "E987", {"start": v(-11.72, -1.7) * mm, "mid": v(-11.77, -2.12) * mm, "end": v(-11.64, -2.53) * mm});
            skArc(sketch, "E988", {"start": v(-11.64, -2.53) * mm, "mid": v(-11.31, -2.9) * mm, "end": v(-10.89, -3.17) * mm});
            skArc(sketch, "E989", {"start": v(-10.89, -3.17) * mm, "mid": v(-10.2, -3.4) * mm, "end": v(-9.48, -3.56) * mm});
            skArc(sketch, "E990", {"start": v(-9.48, -3.56) * mm, "mid": v(-9.02, -3.64) * mm, "end": v(-8.55, -3.72) * mm});
            skArc(sketch, "E991", {"start": v(-8.55, -3.72) * mm, "mid": v(-7.96, -3.83) * mm, "end": v(-7.36, -3.94) * mm});
            skArc(sketch, "E992", {"start": v(-7.36, -3.94) * mm, "mid": v(-6.74, -4.06) * mm, "end": v(-6.12, -4.19) * mm});
            skArc(sketch, "E993", {"start": v(-6.12, -4.19) * mm, "mid": v(-5.57, -4.3) * mm, "end": v(-5.03, -4.42) * mm});
            skLineSegment(sketch, "E994", {"start": v(-5.03, -4.42) * mm, "end": v(-2.53, -4.97) * mm});
            skLineSegment(sketch, "E995", {"start": v(-2.53, -4.97) * mm, "end": v(-3.97, -5.91) * mm});
            skArc(sketch, "E996", {"start": v(-3.97, -5.91) * mm, "mid": v(-4.33, -6.14) * mm, "end": v(-4.7, -6.34) * mm});
            skArc(sketch, "E997", {"start": v(-4.7, -6.34) * mm, "mid": v(-4.96, -6.45) * mm, "end": v(-5.24, -6.52) * mm});
            skArc(sketch, "E998", {"start": v(-5.24, -6.52) * mm, "mid": v(-5.47, -6.54) * mm, "end": v(-5.69, -6.5) * mm});
            skArc(sketch, "E999", {"start": v(-5.69, -6.5) * mm, "mid": v(-5.9, -6.42) * mm, "end": v(-6.1, -6.3) * mm});
            skArc(sketch, "E1000", {"start": v(-6.1, -6.3) * mm, "mid": v(-6.28, -6.17) * mm, "end": v(-6.49, -6.09) * mm});
            skArc(sketch, "E1001", {"start": v(-6.49, -6.09) * mm, "mid": v(-6.69, -6.06) * mm, "end": v(-6.89, -6.09) * mm});
            skArc(sketch, "E1002", {"start": v(-6.89, -6.09) * mm, "mid": v(-7.13, -6.19) * mm, "end": v(-7.36, -6.33) * mm});
            skArc(sketch, "E1003", {"start": v(-7.36, -6.33) * mm, "mid": v(-7.67, -6.58) * mm, "end": v(-7.97, -6.84) * mm});
            skArc(sketch, "E1004", {"start": v(-7.97, -6.84) * mm, "mid": v(-8.39, -7.17) * mm, "end": v(-8.85, -7.43) * mm});
            skArc(sketch, "E1005", {"start": v(-8.85, -7.43) * mm, "mid": v(-9.33, -7.59) * mm, "end": v(-9.84, -7.65) * mm});
            skArc(sketch, "E1006", {"start": v(-9.84, -7.65) * mm, "mid": v(-10.22, -7.6) * mm, "end": v(-10.57, -7.45) * mm});
            skArc(sketch, "E1007", {"start": v(-10.57, -7.45) * mm, "mid": v(-10.8, -7.22) * mm, "end": v(-10.87, -6.91) * mm});
            skArc(sketch, "E1008", {"start": v(-10.87, -6.91) * mm, "mid": v(-10.89, -6.82) * mm, "end": v(-10.94, -6.74) * mm});
            skArc(sketch, "E1009", {"start": v(-10.94, -6.74) * mm, "mid": v(-11.04, -6.64) * mm, "end": v(-11.16, -6.55) * mm});
            skArc(sketch, "E1010", {"start": v(-11.16, -6.55) * mm, "mid": v(-11.32, -6.46) * mm, "end": v(-11.48, -6.38) * mm});
            skArc(sketch, "E1011", {"start": v(-11.48, -6.38) * mm, "mid": v(-11.67, -6.3) * mm, "end": v(-11.86, -6.25) * mm});
            skArc(sketch, "E1012", {"start": v(-11.86, -6.25) * mm, "mid": v(-12.12, -6.14) * mm, "end": v(-12.35, -5.97) * mm});
            skArc(sketch, "E1013", {"start": v(-12.35, -5.97) * mm, "mid": v(-12.56, -5.73) * mm, "end": v(-12.7, -5.45) * mm});
            skArc(sketch, "E1014", {"start": v(-12.7, -5.45) * mm, "mid": v(-12.87, -5.02) * mm, "end": v(-12.98, -4.58) * mm});
            skArc(sketch, "E1015", {"start": v(-12.98, -4.58) * mm, "mid": v(-13.1, -3.87) * mm, "end": v(-13.2, -3.15) * mm});
            skArc(sketch, "E1016", {"start": v(-13.2, -3.15) * mm, "mid": v(-13.3, -2.1) * mm, "end": v(-13.34, -1.03) * mm});
            skArc(sketch, "E1017", {"start": v(-13.34, -1.03) * mm, "mid": v(-13.32, -0.03) * mm, "end": v(-13.23, 0.96) * mm});
            skArc(sketch, "E1018", {"start": v(-13.23, 0.96) * mm, "mid": v(-13.1, 1.74) * mm, "end": v(-12.93, 2.51) * mm});
            skArc(sketch, "E1019", {"start": v(-12.93, 2.51) * mm, "mid": v(-12.74, 2.78) * mm, "end": v(-12.43, 2.89) * mm});
            skArc(sketch, "E1020", {"start": v(-12.43, 2.89) * mm, "mid": v(-12.32, 2.87) * mm, "end": v(-12.22, 2.81) * mm});
            skArc(sketch, "E1021", {"start": v(-12.22, 2.81) * mm, "mid": v(-12.05, 2.66) * mm, "end": v(-11.88, 2.5) * mm});
            skArc(sketch, "E1022", {"start": v(-11.88, 2.5) * mm, "mid": v(-11.7, 2.29) * mm, "end": v(-11.51, 2.07) * mm});
            skArc(sketch, "E1023", {"start": v(-11.51, 2.07) * mm, "mid": v(-11.32, 1.81) * mm, "end": v(-11.15, 1.56) * mm});
            skArc(sketch, "E1024", {"start": v(6.14, -2.79) * mm, "mid": v(5.42, -3.3) * mm, "end": v(4.65, -3.72) * mm});
            skArc(sketch, "E1025", {"start": v(4.65, -3.72) * mm, "mid": v(3.97, -4) * mm, "end": v(3.25, -4.14) * mm});
            skArc(sketch, "E1026", {"start": v(3.25, -4.14) * mm, "mid": v(2.3, -4.2) * mm, "end": v(1.33, -4.16) * mm});
            skArc(sketch, "E1027", {"start": v(1.33, -4.16) * mm, "mid": v(-0.48, -3.97) * mm, "end": v(-2.29, -3.76) * mm});
            skArc(sketch, "E1028", {"start": v(-2.29, -3.76) * mm, "mid": v(-3.26, -3.63) * mm, "end": v(-4.23, -3.49) * mm});
            skArc(sketch, "E1029", {"start": v(-4.23, -3.49) * mm, "mid": v(-4.96, -3.37) * mm, "end": v(-5.68, -3.23) * mm});
            skArc(sketch, "E1030", {"start": v(-5.68, -3.23) * mm, "mid": v(-6.1, -3.14) * mm, "end": v(-6.5, -3.03) * mm});
            skArc(sketch, "E1031", {"start": v(-6.5, -3.03) * mm, "mid": v(-6.54, -2.97) * mm, "end": v(-6.49, -2.92) * mm});
            skArc(sketch, "E1032", {"start": v(-6.49, -2.92) * mm, "mid": v(-5.69, -2.8) * mm, "end": v(-4.88, -2.71) * mm});
            skArc(sketch, "E1033", {"start": v(-4.88, -2.71) * mm, "mid": v(-2.7, -2.52) * mm, "end": v(-0.54, -2.32) * mm});
            skArc(sketch, "E1034", {"start": v(-0.54, -2.32) * mm, "mid": v(1.6, -2.14) * mm, "end": v(3.75, -1.96) * mm});
            skArc(sketch, "E1035", {"start": v(3.75, -1.96) * mm, "mid": v(4.81, -1.89) * mm, "end": v(5.88, -1.83) * mm});
            skLineSegment(sketch, "E1036", {"start": v(5.88, -1.83) * mm, "end": v(7.43, -1.77) * mm});
            skLineSegment(sketch, "E1037", {"start": v(7.43, -1.77) * mm, "end": v(6.14, -2.79) * mm});
            skArc(sketch, "E1038", {"start": v(2.53, -8.45) * mm, "mid": v(2.52, -9.25) * mm, "end": v(2.5, -10.05) * mm});
            skArc(sketch, "E1039", {"start": v(2.5, -10.05) * mm, "mid": v(2.44, -10.25) * mm, "end": v(2.3, -10.4) * mm});
            skArc(sketch, "E1040", {"start": v(2.3, -10.4) * mm, "mid": v(2.11, -10.42) * mm, "end": v(1.96, -10.33) * mm});
            skArc(sketch, "E1041", {"start": v(1.96, -10.33) * mm, "mid": v(1.57, -9.78) * mm, "end": v(1.2, -9.22) * mm});
            skArc(sketch, "E1042", {"start": v(1.2, -9.22) * mm, "mid": v(0.98, -8.88) * mm, "end": v(0.79, -8.52) * mm});
            skArc(sketch, "E1043", {"start": v(0.79, -8.52) * mm, "mid": v(0.7, -8.29) * mm, "end": v(0.64, -8.03) * mm});
            skArc(sketch, "E1044", {"start": v(0.64, -8.03) * mm, "mid": v(0.65, -7.82) * mm, "end": v(0.7, -7.61) * mm});
            skArc(sketch, "E1045", {"start": v(0.7, -7.61) * mm, "mid": v(0.83, -7.38) * mm, "end": v(0.99, -7.16) * mm});
            skArc(sketch, "E1046", {"start": v(0.99, -7.16) * mm, "mid": v(1.32, -6.8) * mm, "end": v(1.68, -6.5) * mm});
            skArc(sketch, "E1047", {"start": v(1.68, -6.5) * mm, "mid": v(1.92, -6.42) * mm, "end": v(2.16, -6.51) * mm});
            skArc(sketch, "E1048", {"start": v(2.16, -6.51) * mm, "mid": v(2.36, -6.77) * mm, "end": v(2.46, -7.08) * mm});
            skArc(sketch, "E1049", {"start": v(2.46, -7.08) * mm, "mid": v(2.51, -7.76) * mm, "end": v(2.53, -8.45) * mm});
            skLineSegment(sketch, "E1050", {"start": v(-1.18, -9.65) * mm, "end": v(-1.02, -12.12) * mm});
            skLineSegment(sketch, "E1051", {"start": v(-1.02, -12.12) * mm, "end": v(-2.3, -11.28) * mm});
            skArc(sketch, "E1052", {"start": v(-2.3, -11.28) * mm, "mid": v(-2.58, -11.08) * mm, "end": v(-2.85, -10.87) * mm});
            skArc(sketch, "E1053", {"start": v(-2.85, -10.87) * mm, "mid": v(-3.16, -10.6) * mm, "end": v(-3.45, -10.32) * mm});
            skArc(sketch, "E1054", {"start": v(-3.45, -10.32) * mm, "mid": v(-3.73, -10.03) * mm, "end": v(-4, -9.72) * mm});
            skArc(sketch, "E1055", {"start": v(-4, -9.72) * mm, "mid": v(-4.21, -9.46) * mm, "end": v(-4.41, -9.18) * mm});
            skArc(sketch, "E1056", {"start": v(-4.41, -9.18) * mm, "mid": v(-4.66, -8.79) * mm, "end": v(-4.9, -8.39) * mm});
            skArc(sketch, "E1057", {"start": v(-4.9, -8.39) * mm, "mid": v(-4.95, -8.21) * mm, "end": v(-4.95, -8.03) * mm});
            skArc(sketch, "E1058", {"start": v(-4.95, -8.03) * mm, "mid": v(-4.88, -7.87) * mm, "end": v(-4.75, -7.76) * mm});
            skArc(sketch, "E1059", {"start": v(-4.75, -7.76) * mm, "mid": v(-4.4, -7.6) * mm, "end": v(-4.06, -7.44) * mm});
            skArc(sketch, "E1060", {"start": v(-4.06, -7.44) * mm, "mid": v(-3.38, -7.2) * mm, "end": v(-2.68, -7.03) * mm});
            skArc(sketch, "E1061", {"start": v(-2.68, -7.03) * mm, "mid": v(-2.26, -7.04) * mm, "end": v(-1.87, -7.22) * mm});
            skArc(sketch, "E1062", {"start": v(-1.87, -7.22) * mm, "mid": v(-1.57, -7.56) * mm, "end": v(-1.4, -7.98) * mm});
            skArc(sketch, "E1063", {"start": v(-1.4, -7.98) * mm, "mid": v(-1.26, -8.81) * mm, "end": v(-1.18, -9.65) * mm});
            skArc(sketch, "E1064", {"start": v(-52.1, -12.32) * mm, "mid": v(-52.11, -12.47) * mm, "end": v(-52.14, -12.61) * mm});
            skArc(sketch, "E1065", {"start": v(-52.14, -12.61) * mm, "mid": v(-52.19, -12.74) * mm, "end": v(-52.25, -12.86) * mm});
            skArc(sketch, "E1066", {"start": v(-52.25, -12.86) * mm, "mid": v(-52.33, -12.96) * mm, "end": v(-52.42, -13.03) * mm});
            skArc(sketch, "E1067", {"start": v(-52.42, -13.03) * mm, "mid": v(-52.51, -13.08) * mm, "end": v(-52.62, -13.1) * mm});
            skArc(sketch, "E1068", {"start": v(-52.62, -13.1) * mm, "mid": v(-52.72, -13.08) * mm, "end": v(-52.81, -13.03) * mm});
            skArc(sketch, "E1069", {"start": v(-52.81, -13.03) * mm, "mid": v(-52.9, -12.96) * mm, "end": v(-52.98, -12.86) * mm});
            skArc(sketch, "E1070", {"start": v(-52.98, -12.86) * mm, "mid": v(-53.05, -12.74) * mm, "end": v(-53.1, -12.61) * mm});
            skArc(sketch, "E1071", {"start": v(-53.1, -12.61) * mm, "mid": v(-53.12, -12.47) * mm, "end": v(-53.13, -12.32) * mm});
            skArc(sketch, "E1072", {"start": v(-53.13, -12.32) * mm, "mid": v(-53.12, -12.17) * mm, "end": v(-53.1, -12.02) * mm});
            skArc(sketch, "E1073", {"start": v(-53.1, -12.02) * mm, "mid": v(-53.05, -11.9) * mm, "end": v(-52.98, -11.77) * mm});
            skArc(sketch, "E1074", {"start": v(-52.98, -11.77) * mm, "mid": v(-52.9, -11.68) * mm, "end": v(-52.81, -11.6) * mm});
            skArc(sketch, "E1075", {"start": v(-52.81, -11.6) * mm, "mid": v(-52.72, -11.56) * mm, "end": v(-52.62, -11.54) * mm});
            skArc(sketch, "E1076", {"start": v(-52.62, -11.54) * mm, "mid": v(-52.51, -11.56) * mm, "end": v(-52.42, -11.6) * mm});
            skArc(sketch, "E1077", {"start": v(-52.42, -11.6) * mm, "mid": v(-52.33, -11.68) * mm, "end": v(-52.25, -11.77) * mm});
            skArc(sketch, "E1078", {"start": v(-52.25, -11.77) * mm, "mid": v(-52.19, -11.9) * mm, "end": v(-52.14, -12.02) * mm});
            skArc(sketch, "E1079", {"start": v(-52.14, -12.02) * mm, "mid": v(-52.11, -12.17) * mm, "end": v(-52.1, -12.32) * mm});
            skArc(sketch, "E1080", {"start": v(-49.62, -17.85) * mm, "mid": v(-49.6, -18.38) * mm, "end": v(-49.6, -18.91) * mm});
            skArc(sketch, "E1081", {"start": v(-49.6, -18.91) * mm, "mid": v(-49.64, -19.24) * mm, "end": v(-49.76, -19.55) * mm});
            skArc(sketch, "E1082", {"start": v(-49.76, -19.55) * mm, "mid": v(-49.94, -19.81) * mm, "end": v(-50.18, -20.02) * mm});
            skArc(sketch, "E1083", {"start": v(-50.18, -20.02) * mm, "mid": v(-50.59, -20.3) * mm, "end": v(-51.02, -20.54) * mm});
            skArc(sketch, "E1084", {"start": v(-51.02, -20.54) * mm, "mid": v(-51.32, -20.7) * mm, "end": v(-51.63, -20.84) * mm});
            skArc(sketch, "E1085", {"start": v(-51.63, -20.84) * mm, "mid": v(-51.91, -20.97) * mm, "end": v(-52.2, -21.1) * mm});
            skArc(sketch, "E1086", {"start": v(-52.2, -21.1) * mm, "mid": v(-52.43, -21.2) * mm, "end": v(-52.67, -21.3) * mm});
            skArc(sketch, "E1087", {"start": v(-52.67, -21.3) * mm, "mid": v(-52.76, -21.33) * mm, "end": v(-52.85, -21.34) * mm});
            skArc(sketch, "E1088", {"start": v(-52.85, -21.34) * mm, "mid": v(-52.93, -21.3) * mm, "end": v(-52.96, -21.24) * mm});
            skArc(sketch, "E1089", {"start": v(-52.96, -21.24) * mm, "mid": v(-53, -20.84) * mm, "end": v(-53.05, -20.45) * mm});
            skArc(sketch, "E1090", {"start": v(-53.05, -20.45) * mm, "mid": v(-53.09, -19.96) * mm, "end": v(-53.11, -19.47) * mm});
            skArc(sketch, "E1091", {"start": v(-53.11, -19.47) * mm, "mid": v(-53.13, -18.89) * mm, "end": v(-53.13, -18.3) * mm});
            skLineSegment(sketch, "E1092", {"start": v(-53.13, -18.3) * mm, "end": v(-53.13, -15.28) * mm});
            skLineSegment(sketch, "E1093", {"start": v(-53.13, -15.28) * mm, "end": v(-51.46, -15.62) * mm});
            skArc(sketch, "E1094", {"start": v(-51.46, -15.62) * mm, "mid": v(-50.99, -15.73) * mm, "end": v(-50.53, -15.88) * mm});
            skArc(sketch, "E1095", {"start": v(-50.53, -15.88) * mm, "mid": v(-50.26, -16.02) * mm, "end": v(-50.04, -16.22) * mm});
            skArc(sketch, "E1096", {"start": v(-50.04, -16.22) * mm, "mid": v(-49.87, -16.49) * mm, "end": v(-49.77, -16.78) * mm});
            skArc(sketch, "E1097", {"start": v(-49.77, -16.78) * mm, "mid": v(-49.68, -17.31) * mm, "end": v(-49.62, -17.85) * mm});
            skLineSegment(sketch, "E1098", {"start": v(-39.15, -16.7) * mm, "end": v(-35.6, -16.7) * mm});
            skLineSegment(sketch, "E1099", {"start": v(-35.6, -16.7) * mm, "end": v(-35.66, -20.7) * mm});
            skArc(sketch, "E1100", {"start": v(-35.66, -20.7) * mm, "mid": v(-35.7, -22.15) * mm, "end": v(-35.77, -23.6) * mm});
            skArc(sketch, "E1101", {"start": v(-35.77, -23.6) * mm, "mid": v(-35.86, -24.62) * mm, "end": v(-36.03, -25.63) * mm});
            skArc(sketch, "E1102", {"start": v(-36.03, -25.63) * mm, "mid": v(-36.19, -26.27) * mm, "end": v(-36.41, -26.9) * mm});
            skArc(sketch, "E1103", {"start": v(-36.41, -26.9) * mm, "mid": v(-36.63, -27.16) * mm, "end": v(-36.96, -27.26) * mm});
            skArc(sketch, "E1104", {"start": v(-36.96, -27.26) * mm, "mid": v(-37.1, -27.28) * mm, "end": v(-37.22, -27.32) * mm});
            skArc(sketch, "E1105", {"start": v(-37.22, -27.32) * mm, "mid": v(-37.42, -27.43) * mm, "end": v(-37.6, -27.54) * mm});
            skArc(sketch, "E1106", {"start": v(-37.6, -27.54) * mm, "mid": v(-37.82, -27.68) * mm, "end": v(-38.02, -27.84) * mm});
            skArc(sketch, "E1107", {"start": v(-38.02, -27.84) * mm, "mid": v(-38.23, -28.01) * mm, "end": v(-38.42, -28.2) * mm});
            skArc(sketch, "E1108", {"start": v(-38.42, -28.2) * mm, "mid": v(-38.71, -28.5) * mm, "end": v(-39, -28.8) * mm});
            skArc(sketch, "E1109", {"start": v(-39, -28.8) * mm, "mid": v(-39.06, -28.91) * mm, "end": v(-39.07, -29.04) * mm});
            skArc(sketch, "E1110", {"start": v(-39.07, -29.04) * mm, "mid": v(-39.03, -29.15) * mm, "end": v(-38.93, -29.21) * mm});
            skArc(sketch, "E1111", {"start": v(-38.93, -29.21) * mm, "mid": v(-38.6, -29.32) * mm, "end": v(-38.27, -29.41) * mm});
            skArc(sketch, "E1112", {"start": v(-38.27, -29.41) * mm, "mid": v(-37.96, -29.5) * mm, "end": v(-37.65, -29.62) * mm});
            skArc(sketch, "E1113", {"start": v(-37.65, -29.62) * mm, "mid": v(-37.53, -29.72) * mm, "end": v(-37.46, -29.87) * mm});
            skArc(sketch, "E1114", {"start": v(-37.46, -29.87) * mm, "mid": v(-37.45, -30.07) * mm, "end": v(-37.5, -30.26) * mm});
            skArc(sketch, "E1115", {"start": v(-37.5, -30.26) * mm, "mid": v(-37.73, -30.73) * mm, "end": v(-37.96, -31.19) * mm});
            skArc(sketch, "E1116", {"start": v(-37.96, -31.19) * mm, "mid": v(-38.1, -31.47) * mm, "end": v(-38.27, -31.76) * mm});
            skArc(sketch, "E1117", {"start": v(-38.27, -31.76) * mm, "mid": v(-38.41, -32) * mm, "end": v(-38.56, -32.24) * mm});
            skArc(sketch, "E1118", {"start": v(-38.56, -32.24) * mm, "mid": v(-38.69, -32.43) * mm, "end": v(-38.82, -32.62) * mm});
            skArc(sketch, "E1119", {"start": v(-38.82, -32.62) * mm, "mid": v(-38.87, -32.66) * mm, "end": v(-38.93, -32.68) * mm});
            skArc(sketch, "E1120", {"start": v(-38.93, -32.68) * mm, "mid": v(-39, -32.66) * mm, "end": v(-39.05, -32.61) * mm});
            skArc(sketch, "E1121", {"start": v(-39.05, -32.61) * mm, "mid": v(-39.4, -32.05) * mm, "end": v(-39.75, -31.49) * mm});
            skArc(sketch, "E1122", {"start": v(-39.75, -31.49) * mm, "mid": v(-40.15, -30.84) * mm, "end": v(-40.55, -30.19) * mm});
            skArc(sketch, "E1123", {"start": v(-40.55, -30.19) * mm, "mid": v(-41, -29.41) * mm, "end": v(-41.45, -28.64) * mm});
            skArc(sketch, "E1124", {"start": v(-41.45, -28.64) * mm, "mid": v(-41.96, -27.78) * mm, "end": v(-42.48, -26.92) * mm});
            skArc(sketch, "E1125", {"start": v(-42.48, -26.92) * mm, "mid": v(-43.06, -26) * mm, "end": v(-43.64, -25.08) * mm});
            skArc(sketch, "E1126", {"start": v(-43.64, -25.08) * mm, "mid": v(-44.2, -24.24) * mm, "end": v(-44.76, -23.4) * mm});
            skArc(sketch, "E1127", {"start": v(-44.76, -23.4) * mm, "mid": v(-45.18, -22.79) * mm, "end": v(-45.62, -22.2) * mm});
            skArc(sketch, "E1128", {"start": v(-45.62, -22.2) * mm, "mid": v(-46.06, -21.59) * mm, "end": v(-46.48, -20.97) * mm});
            skArc(sketch, "E1129", {"start": v(-46.48, -20.97) * mm, "mid": v(-46.78, -20.45) * mm, "end": v(-47.04, -19.9) * mm});
            skArc(sketch, "E1130", {"start": v(-47.04, -19.9) * mm, "mid": v(-47.22, -19.42) * mm, "end": v(-47.36, -18.92) * mm});
            skArc(sketch, "E1131", {"start": v(-47.36, -18.92) * mm, "mid": v(-47.44, -18.42) * mm, "end": v(-47.46, -17.91) * mm});
            skLineSegment(sketch, "E1132", {"start": v(-47.46, -17.91) * mm, "end": v(-47.46, -16.04) * mm});
            skLineSegment(sketch, "E1133", {"start": v(-47.46, -16.04) * mm, "end": v(-45.07, -16.37) * mm});
            skArc(sketch, "E1134", {"start": v(-45.07, -16.37) * mm, "mid": v(-44.5, -16.44) * mm, "end": v(-43.9, -16.5) * mm});
            skArc(sketch, "E1135", {"start": v(-43.9, -16.5) * mm, "mid": v(-43.13, -16.55) * mm, "end": v(-42.34, -16.6) * mm});
            skArc(sketch, "E1136", {"start": v(-42.34, -16.6) * mm, "mid": v(-41.5, -16.64) * mm, "end": v(-40.67, -16.67) * mm});
            skArc(sketch, "E1137", {"start": v(-40.67, -16.67) * mm, "mid": v(-39.9, -16.7) * mm, "end": v(-39.15, -16.7) * mm});
            skArc(sketch, "E1138", {"start": v(28.18, -20.3) * mm, "mid": v(28.59, -20.57) * mm, "end": v(28.98, -20.86) * mm});
            skArc(sketch, "E1139", {"start": v(28.98, -20.86) * mm, "mid": v(29.51, -21.3) * mm, "end": v(30.04, -21.73) * mm});
            skArc(sketch, "E1140", {"start": v(30.04, -21.73) * mm, "mid": v(30.6, -22.23) * mm, "end": v(31.16, -22.74) * mm});
            skArc(sketch, "E1141", {"start": v(31.16, -22.74) * mm, "mid": v(31.67, -23.24) * mm, "end": v(32.17, -23.74) * mm});
            skLineSegment(sketch, "E1142", {"start": v(32.17, -23.74) * mm, "end": v(34.48, -26.16) * mm});
            skLineSegment(sketch, "E1143", {"start": v(34.48, -26.16) * mm, "end": v(32.8, -27.6) * mm});
            skArc(sketch, "E1144", {"start": v(32.8, -27.6) * mm, "mid": v(32.48, -27.87) * mm, "end": v(32.15, -28.14) * mm});
            skArc(sketch, "E1145", {"start": v(32.15, -28.14) * mm, "mid": v(31.85, -28.38) * mm, "end": v(31.55, -28.61) * mm});
            skArc(sketch, "E1146", {"start": v(31.55, -28.61) * mm, "mid": v(31.29, -28.8) * mm, "end": v(31.03, -28.98) * mm});
            skArc(sketch, "E1147", {"start": v(31.03, -28.98) * mm, "mid": v(30.95, -29.03) * mm, "end": v(30.86, -29.05) * mm});
            skArc(sketch, "E1148", {"start": v(30.86, -29.05) * mm, "mid": v(30.53, -29) * mm, "end": v(30.25, -28.81) * mm});
            skArc(sketch, "E1149", {"start": v(30.25, -28.81) * mm, "mid": v(29.17, -27.67) * mm, "end": v(28.11, -26.52) * mm});
            skArc(sketch, "E1150", {"start": v(28.11, -26.52) * mm, "mid": v(27.08, -25.38) * mm, "end": v(26.07, -24.22) * mm});
            skArc(sketch, "E1151", {"start": v(26.07, -24.22) * mm, "mid": v(25.83, -23.84) * mm, "end": v(25.7, -23.4) * mm});
            skArc(sketch, "E1152", {"start": v(25.7, -23.4) * mm, "mid": v(25.64, -22.76) * mm, "end": v(25.62, -22.13) * mm});
            skArc(sketch, "E1153", {"start": v(25.62, -22.13) * mm, "mid": v(25.64, -21.43) * mm, "end": v(25.69, -20.73) * mm});
            skArc(sketch, "E1154", {"start": v(25.69, -20.73) * mm, "mid": v(25.76, -20.11) * mm, "end": v(25.85, -19.5) * mm});
            skArc(sketch, "E1155", {"start": v(25.85, -19.5) * mm, "mid": v(25.94, -19.34) * mm, "end": v(26.11, -19.28) * mm});
            skArc(sketch, "E1156", {"start": v(26.11, -19.28) * mm, "mid": v(26.23, -19.3) * mm, "end": v(26.34, -19.33) * mm});
            skArc(sketch, "E1157", {"start": v(26.34, -19.33) * mm, "mid": v(26.61, -19.45) * mm, "end": v(26.88, -19.58) * mm});
            skArc(sketch, "E1158", {"start": v(26.88, -19.58) * mm, "mid": v(27.2, -19.74) * mm, "end": v(27.5, -19.91) * mm});
            skArc(sketch, "E1159", {"start": v(27.5, -19.91) * mm, "mid": v(27.84, -20.1) * mm, "end": v(28.18, -20.3) * mm});
            skArc(sketch, "E1160", {"start": v(-49.85, -24.24) * mm, "mid": v(-49.7, -25.65) * mm, "end": v(-49.6, -27.06) * mm});
            skArc(sketch, "E1161", {"start": v(-49.6, -27.06) * mm, "mid": v(-49.55, -29.07) * mm, "end": v(-49.53, -31.08) * mm});
            skArc(sketch, "E1162", {"start": v(-49.53, -31.08) * mm, "mid": v(-49.54, -33.16) * mm, "end": v(-49.56, -35.24) * mm});
            skArc(sketch, "E1163", {"start": v(-49.56, -35.24) * mm, "mid": v(-49.64, -35.6) * mm, "end": v(-49.85, -35.92) * mm});
            skArc(sketch, "E1164", {"start": v(-49.85, -35.92) * mm, "mid": v(-49.95, -35.98) * mm, "end": v(-50.06, -36) * mm});
            skArc(sketch, "E1165", {"start": v(-50.06, -36) * mm, "mid": v(-50.29, -35.97) * mm, "end": v(-50.51, -35.92) * mm});
            skArc(sketch, "E1166", {"start": v(-50.51, -35.92) * mm, "mid": v(-50.79, -35.84) * mm, "end": v(-51.06, -35.75) * mm});
            skArc(sketch, "E1167", {"start": v(-51.06, -35.75) * mm, "mid": v(-51.36, -35.62) * mm, "end": v(-51.65, -35.48) * mm});
            skLineSegment(sketch, "E1168", {"start": v(-51.65, -35.48) * mm, "end": v(-53.13, -34.71) * mm});
            skLineSegment(sketch, "E1169", {"start": v(-53.13, -34.71) * mm, "end": v(-53.13, -28.88) * mm});
            skArc(sketch, "E1170", {"start": v(-53.13, -28.88) * mm, "mid": v(-53.13, -27.06) * mm, "end": v(-53.1, -25.24) * mm});
            skArc(sketch, "E1171", {"start": v(-53.1, -25.24) * mm, "mid": v(-53.07, -24.52) * mm, "end": v(-52.97, -23.8) * mm});
            skArc(sketch, "E1172", {"start": v(-52.97, -23.8) * mm, "mid": v(-52.84, -23.39) * mm, "end": v(-52.63, -23.02) * mm});
            skArc(sketch, "E1173", {"start": v(-52.63, -23.02) * mm, "mid": v(-52.33, -22.71) * mm, "end": v(-51.97, -22.48) * mm});
            skArc(sketch, "E1174", {"start": v(-51.97, -22.48) * mm, "mid": v(-51.42, -22.23) * mm, "end": v(-50.85, -22) * mm});
            skArc(sketch, "E1175", {"start": v(-50.85, -22) * mm, "mid": v(-50.61, -21.98) * mm, "end": v(-50.4, -22.08) * mm});
            skArc(sketch, "E1176", {"start": v(-50.4, -22.08) * mm, "mid": v(-50.21, -22.3) * mm, "end": v(-50.12, -22.55) * mm});
            skArc(sketch, "E1177", {"start": v(-50.12, -22.55) * mm, "mid": v(-49.98, -23.4) * mm, "end": v(-49.85, -24.24) * mm});
            skArc(sketch, "E1178", {"start": v(-44.04, -29.84) * mm, "mid": v(-44, -30.27) * mm, "end": v(-44.02, -30.7) * mm});
            skArc(sketch, "E1179", {"start": v(-44.02, -30.7) * mm, "mid": v(-44.1, -31.1) * mm, "end": v(-44.23, -31.5) * mm});
            skArc(sketch, "E1180", {"start": v(-44.23, -31.5) * mm, "mid": v(-44.45, -31.93) * mm, "end": v(-44.72, -32.34) * mm});
            skArc(sketch, "E1181", {"start": v(-44.72, -32.34) * mm, "mid": v(-45.16, -32.9) * mm, "end": v(-45.62, -33.45) * mm});
            skLineSegment(sketch, "E1182", {"start": v(-45.62, -33.45) * mm, "end": v(-47.42, -35.51) * mm});
            skLineSegment(sketch, "E1183", {"start": v(-47.42, -35.51) * mm, "end": v(-47.44, -30.8) * mm});
            skArc(sketch, "E1184", {"start": v(-47.44, -30.8) * mm, "mid": v(-47.44, -29.84) * mm, "end": v(-47.43, -28.88) * mm});
            skArc(sketch, "E1185", {"start": v(-47.43, -28.88) * mm, "mid": v(-47.4, -27.93) * mm, "end": v(-47.36, -26.97) * mm});
            skArc(sketch, "E1186", {"start": v(-47.36, -26.97) * mm, "mid": v(-47.3, -26.15) * mm, "end": v(-47.25, -25.33) * mm});
            skArc(sketch, "E1187", {"start": v(-47.25, -25.33) * mm, "mid": v(-47.2, -24.84) * mm, "end": v(-47.11, -24.36) * mm});
            skLineSegment(sketch, "E1188", {"start": v(-47.11, -24.36) * mm, "end": v(-46.77, -22.63) * mm});
            skLineSegment(sketch, "E1189", {"start": v(-46.77, -22.63) * mm, "end": v(-45.52, -25.46) * mm});
            skArc(sketch, "E1190", {"start": v(-45.52, -25.46) * mm, "mid": v(-45.26, -26.06) * mm, "end": v(-45.02, -26.66) * mm});
            skArc(sketch, "E1191", {"start": v(-45.02, -26.66) * mm, "mid": v(-44.8, -27.28) * mm, "end": v(-44.57, -27.92) * mm});
            skArc(sketch, "E1192", {"start": v(-44.57, -27.92) * mm, "mid": v(-44.39, -28.48) * mm, "end": v(-44.21, -29.06) * mm});
            skArc(sketch, "E1193", {"start": v(-44.21, -29.06) * mm, "mid": v(-44.11, -29.45) * mm, "end": v(-44.04, -29.84) * mm});
            skArc(sketch, "E1194", {"start": v(16.91, -26.9) * mm, "mid": v(16.9, -27.3) * mm, "end": v(16.85, -27.7) * mm});
            skArc(sketch, "E1195", {"start": v(16.85, -27.7) * mm, "mid": v(16.76, -28.2) * mm, "end": v(16.63, -28.7) * mm});
            skArc(sketch, "E1196", {"start": v(16.63, -28.7) * mm, "mid": v(16.48, -29.24) * mm, "end": v(16.3, -29.76) * mm});
            skArc(sketch, "E1197", {"start": v(16.3, -29.76) * mm, "mid": v(16.11, -30.23) * mm, "end": v(15.9, -30.68) * mm});
            skArc(sketch, "E1198", {"start": v(15.9, -30.68) * mm, "mid": v(15.55, -31.35) * mm, "end": v(15.19, -32.02) * mm});
            skArc(sketch, "E1199", {"start": v(15.19, -32.02) * mm, "mid": v(15.04, -32.22) * mm, "end": v(14.84, -32.37) * mm});
            skArc(sketch, "E1200", {"start": v(14.84, -32.37) * mm, "mid": v(14.65, -32.41) * mm, "end": v(14.46, -32.35) * mm});
            skArc(sketch, "E1201", {"start": v(14.46, -32.35) * mm, "mid": v(14.12, -32.11) * mm, "end": v(13.8, -31.84) * mm});
            skArc(sketch, "E1202", {"start": v(13.8, -31.84) * mm, "mid": v(13.45, -31.44) * mm, "end": v(13.2, -30.96) * mm});
            skArc(sketch, "E1203", {"start": v(13.2, -30.96) * mm, "mid": v(13.07, -30.46) * mm, "end": v(13.08, -29.94) * mm});
            skArc(sketch, "E1204", {"start": v(13.08, -29.94) * mm, "mid": v(13.24, -29.17) * mm, "end": v(13.5, -28.42) * mm});
            skArc(sketch, "E1205", {"start": v(13.5, -28.42) * mm, "mid": v(14.1, -27) * mm, "end": v(14.73, -25.57) * mm});
            skArc(sketch, "E1206", {"start": v(14.73, -25.57) * mm, "mid": v(15.15, -24.66) * mm, "end": v(15.58, -23.75) * mm});
            skArc(sketch, "E1207", {"start": v(15.58, -23.75) * mm, "mid": v(15.73, -23.5) * mm, "end": v(15.93, -23.27) * mm});
            skArc(sketch, "E1208", {"start": v(15.93, -23.27) * mm, "mid": v(16.07, -23.22) * mm, "end": v(16.2, -23.3) * mm});
            skArc(sketch, "E1209", {"start": v(16.2, -23.3) * mm, "mid": v(16.35, -23.6) * mm, "end": v(16.46, -23.91) * mm});
            skArc(sketch, "E1210", {"start": v(16.46, -23.91) * mm, "mid": v(16.55, -24.22) * mm, "end": v(16.62, -24.53) * mm});
            skArc(sketch, "E1211", {"start": v(16.62, -24.53) * mm, "mid": v(16.7, -24.92) * mm, "end": v(16.76, -25.32) * mm});
            skArc(sketch, "E1212", {"start": v(16.76, -25.32) * mm, "mid": v(16.82, -25.74) * mm, "end": v(16.86, -26.15) * mm});
            skArc(sketch, "E1213", {"start": v(16.86, -26.15) * mm, "mid": v(16.9, -26.53) * mm, "end": v(16.91, -26.9) * mm});
            skLineSegment(sketch, "E1214", {"start": v(22.61, -26.62) * mm, "end": v(22.6, -30.36) * mm});
            skLineSegment(sketch, "E1215", {"start": v(22.6, -30.36) * mm, "end": v(21.36, -28.94) * mm});
            skArc(sketch, "E1216", {"start": v(21.36, -28.94) * mm, "mid": v(20.98, -28.5) * mm, "end": v(20.62, -28.02) * mm});
            skArc(sketch, "E1217", {"start": v(20.62, -28.02) * mm, "mid": v(20.47, -27.73) * mm, "end": v(20.39, -27.4) * mm});
            skArc(sketch, "E1218", {"start": v(20.39, -27.4) * mm, "mid": v(20.38, -27.05) * mm, "end": v(20.44, -26.69) * mm});
            skArc(sketch, "E1219", {"start": v(20.44, -26.69) * mm, "mid": v(20.66, -25.94) * mm, "end": v(20.9, -25.2) * mm});
            skArc(sketch, "E1220", {"start": v(20.9, -25.2) * mm, "mid": v(21.07, -24.76) * mm, "end": v(21.24, -24.32) * mm});
            skArc(sketch, "E1221", {"start": v(21.24, -24.32) * mm, "mid": v(21.41, -23.94) * mm, "end": v(21.6, -23.57) * mm});
            skArc(sketch, "E1222", {"start": v(21.6, -23.57) * mm, "mid": v(21.76, -23.28) * mm, "end": v(21.94, -23) * mm});
            skArc(sketch, "E1223", {"start": v(21.94, -23) * mm, "mid": v(22.04, -22.91) * mm, "end": v(22.16, -22.88) * mm});
            skArc(sketch, "E1224", {"start": v(22.16, -22.88) * mm, "mid": v(22.28, -22.93) * mm, "end": v(22.35, -23.04) * mm});
            skArc(sketch, "E1225", {"start": v(22.35, -23.04) * mm, "mid": v(22.43, -23.5) * mm, "end": v(22.49, -23.98) * mm});
            skArc(sketch, "E1226", {"start": v(22.49, -23.98) * mm, "mid": v(22.55, -24.58) * mm, "end": v(22.59, -25.19) * mm});
            skArc(sketch, "E1227", {"start": v(22.59, -25.19) * mm, "mid": v(22.6, -25.9) * mm, "end": v(22.61, -26.62) * mm});
            skArc(sketch, "E1228", {"start": v(-53.65, -28.81) * mm, "mid": v(-53.65, -29.75) * mm, "end": v(-53.67, -30.69) * mm});
            skArc(sketch, "E1229", {"start": v(-53.67, -30.69) * mm, "mid": v(-53.7, -31.48) * mm, "end": v(-53.73, -32.27) * mm});
            skArc(sketch, "E1230", {"start": v(-53.73, -32.27) * mm, "mid": v(-53.77, -32.93) * mm, "end": v(-53.82, -33.6) * mm});
            skArc(sketch, "E1231", {"start": v(-53.82, -33.6) * mm, "mid": v(-53.85, -33.68) * mm, "end": v(-53.93, -33.7) * mm});
            skArc(sketch, "E1232", {"start": v(-53.93, -33.7) * mm, "mid": v(-54.03, -33.7) * mm, "end": v(-54.12, -33.65) * mm});
            skArc(sketch, "E1233", {"start": v(-54.12, -33.65) * mm, "mid": v(-54.54, -33.37) * mm, "end": v(-54.95, -33.1) * mm});
            skArc(sketch, "E1234", {"start": v(-54.95, -33.1) * mm, "mid": v(-55.44, -32.76) * mm, "end": v(-55.93, -32.42) * mm});
            skArc(sketch, "E1235", {"start": v(-55.93, -32.42) * mm, "mid": v(-56.48, -32.02) * mm, "end": v(-57.03, -31.62) * mm});
            skLineSegment(sketch, "E1236", {"start": v(-57.03, -31.62) * mm, "end": v(-59.85, -29.54) * mm});
            skLineSegment(sketch, "E1237", {"start": v(-59.85, -29.54) * mm, "end": v(-58.49, -27.75) * mm});
            skArc(sketch, "E1238", {"start": v(-58.49, -27.75) * mm, "mid": v(-57.95, -27.09) * mm, "end": v(-57.37, -26.45) * mm});
            skArc(sketch, "E1239", {"start": v(-57.37, -26.45) * mm, "mid": v(-56.72, -25.8) * mm, "end": v(-56.04, -25.2) * mm});
            skArc(sketch, "E1240", {"start": v(-56.04, -25.2) * mm, "mid": v(-55.41, -24.67) * mm, "end": v(-54.76, -24.18) * mm});
            skArc(sketch, "E1241", {"start": v(-54.76, -24.18) * mm, "mid": v(-54.42, -24) * mm, "end": v(-54.03, -23.93) * mm});
            skArc(sketch, "E1242", {"start": v(-54.03, -23.93) * mm, "mid": v(-53.93, -23.97) * mm, "end": v(-53.88, -24.06) * mm});
            skArc(sketch, "E1243", {"start": v(-53.88, -24.06) * mm, "mid": v(-53.82, -24.71) * mm, "end": v(-53.76, -25.36) * mm});
            skArc(sketch, "E1244", {"start": v(-53.76, -25.36) * mm, "mid": v(-53.7, -26.14) * mm, "end": v(-53.68, -26.93) * mm});
            skArc(sketch, "E1245", {"start": v(-53.68, -26.93) * mm, "mid": v(-53.66, -27.87) * mm, "end": v(-53.65, -28.81) * mm});
            skArc(sketch, "E1246", {"start": v(20.05, -25.46) * mm, "mid": v(19.94, -25.67) * mm, "end": v(19.8, -25.87) * mm});
            skArc(sketch, "E1247", {"start": v(19.8, -25.87) * mm, "mid": v(19.69, -26.03) * mm, "end": v(19.56, -26.17) * mm});
            skArc(sketch, "E1248", {"start": v(19.56, -26.17) * mm, "mid": v(19.45, -26.26) * mm, "end": v(19.34, -26.34) * mm});
            skArc(sketch, "E1249", {"start": v(19.34, -26.34) * mm, "mid": v(19.27, -26.35) * mm, "end": v(19.2, -26.32) * mm});
            skArc(sketch, "E1250", {"start": v(19.2, -26.32) * mm, "mid": v(19.15, -26.24) * mm, "end": v(19.14, -26.15) * mm});
            skArc(sketch, "E1251", {"start": v(19.14, -26.15) * mm, "mid": v(19.16, -25.98) * mm, "end": v(19.2, -25.81) * mm});
            skArc(sketch, "E1252", {"start": v(19.2, -25.81) * mm, "mid": v(19.25, -25.6) * mm, "end": v(19.33, -25.4) * mm});
            skArc(sketch, "E1253", {"start": v(19.33, -25.4) * mm, "mid": v(19.43, -25.17) * mm, "end": v(19.54, -24.94) * mm});
            skArc(sketch, "E1254", {"start": v(19.54, -24.94) * mm, "mid": v(19.66, -24.74) * mm, "end": v(19.79, -24.53) * mm});
            skArc(sketch, "E1255", {"start": v(19.79, -24.53) * mm, "mid": v(19.9, -24.38) * mm, "end": v(20.04, -24.23) * mm});
            skArc(sketch, "E1256", {"start": v(20.04, -24.23) * mm, "mid": v(20.14, -24.14) * mm, "end": v(20.25, -24.06) * mm});
            skArc(sketch, "E1257", {"start": v(20.25, -24.06) * mm, "mid": v(20.33, -24.05) * mm, "end": v(20.4, -24.08) * mm});
            skArc(sketch, "E1258", {"start": v(20.4, -24.08) * mm, "mid": v(20.45, -24.16) * mm, "end": v(20.46, -24.25) * mm});
            skArc(sketch, "E1259", {"start": v(20.46, -24.25) * mm, "mid": v(20.44, -24.42) * mm, "end": v(20.4, -24.6) * mm});
            skArc(sketch, "E1260", {"start": v(20.4, -24.6) * mm, "mid": v(20.34, -24.8) * mm, "end": v(20.26, -25.01) * mm});
            skArc(sketch, "E1261", {"start": v(20.26, -25.01) * mm, "mid": v(20.17, -25.24) * mm, "end": v(20.05, -25.46) * mm});
            skArc(sketch, "E1262", {"start": v(27.67, -30.44) * mm, "mid": v(27.35, -30.68) * mm, "end": v(27.02, -30.9) * mm});
            skArc(sketch, "E1263", {"start": v(27.02, -30.9) * mm, "mid": v(26.73, -31.1) * mm, "end": v(26.43, -31.3) * mm});
            skArc(sketch, "E1264", {"start": v(26.43, -31.3) * mm, "mid": v(26.18, -31.45) * mm, "end": v(25.93, -31.6) * mm});
            skArc(sketch, "E1265", {"start": v(25.93, -31.6) * mm, "mid": v(25.85, -31.63) * mm, "end": v(25.75, -31.64) * mm});
            skArc(sketch, "E1266", {"start": v(25.75, -31.64) * mm, "mid": v(25.68, -31.62) * mm, "end": v(25.64, -31.54) * mm});
            skArc(sketch, "E1267", {"start": v(25.64, -31.54) * mm, "mid": v(25.6, -31.14) * mm, "end": v(25.55, -30.74) * mm});
            skArc(sketch, "E1268", {"start": v(25.55, -30.74) * mm, "mid": v(25.51, -30.25) * mm, "end": v(25.49, -29.75) * mm});
            skArc(sketch, "E1269", {"start": v(25.49, -29.75) * mm, "mid": v(25.47, -29.16) * mm, "end": v(25.47, -28.57) * mm});
            skLineSegment(sketch, "E1270", {"start": v(25.47, -28.57) * mm, "end": v(25.47, -25.5) * mm});
            skLineSegment(sketch, "E1271", {"start": v(25.47, -25.5) * mm, "end": v(27.38, -27.37) * mm});
            skLineSegment(sketch, "E1272", {"start": v(27.38, -27.37) * mm, "end": v(29.3, -29.24) * mm});
            skLineSegment(sketch, "E1273", {"start": v(29.3, -29.24) * mm, "end": v(27.67, -30.44) * mm});
            skArc(sketch, "E1274", {"start": v(-43.1, -27.5) * mm, "mid": v(-42.81, -28.06) * mm, "end": v(-42.54, -28.63) * mm});
            skArc(sketch, "E1275", {"start": v(-42.54, -28.63) * mm, "mid": v(-42.42, -28.93) * mm, "end": v(-42.35, -29.23) * mm});
            skArc(sketch, "E1276", {"start": v(-42.35, -29.23) * mm, "mid": v(-42.37, -29.35) * mm, "end": v(-42.47, -29.41) * mm});
            skArc(sketch, "E1277", {"start": v(-42.47, -29.41) * mm, "mid": v(-42.63, -29.41) * mm, "end": v(-42.77, -29.36) * mm});
            skArc(sketch, "E1278", {"start": v(-42.77, -29.36) * mm, "mid": v(-43.01, -29.16) * mm, "end": v(-43.19, -28.9) * mm});
            skArc(sketch, "E1279", {"start": v(-43.19, -28.9) * mm, "mid": v(-43.48, -28.23) * mm, "end": v(-43.76, -27.55) * mm});
            skArc(sketch, "E1280", {"start": v(-43.76, -27.55) * mm, "mid": v(-44.02, -26.88) * mm, "end": v(-44.26, -26.2) * mm});
            skArc(sketch, "E1281", {"start": v(-44.26, -26.2) * mm, "mid": v(-44.23, -26.04) * mm, "end": v(-44.1, -25.98) * mm});
            skArc(sketch, "E1282", {"start": v(-44.1, -25.98) * mm, "mid": v(-44.03, -26) * mm, "end": v(-43.98, -26.04) * mm});
            skArc(sketch, "E1283", {"start": v(-43.98, -26.04) * mm, "mid": v(-43.85, -26.23) * mm, "end": v(-43.72, -26.42) * mm});
            skArc(sketch, "E1284", {"start": v(-43.72, -26.42) * mm, "mid": v(-43.56, -26.67) * mm, "end": v(-43.41, -26.91) * mm});
            skArc(sketch, "E1285", {"start": v(-43.41, -26.91) * mm, "mid": v(-43.25, -27.2) * mm, "end": v(-43.1, -27.5) * mm});
            skArc(sketch, "E1286", {"start": v(12.68, -27.97) * mm, "mid": v(12.55, -28.27) * mm, "end": v(12.4, -28.57) * mm});
            skArc(sketch, "E1287", {"start": v(12.4, -28.57) * mm, "mid": v(12.26, -28.8) * mm, "end": v(12.1, -29.03) * mm});
            skArc(sketch, "E1288", {"start": v(12.1, -29.03) * mm, "mid": v(11.99, -29.17) * mm, "end": v(11.86, -29.3) * mm});
            skArc(sketch, "E1289", {"start": v(11.86, -29.3) * mm, "mid": v(11.77, -29.33) * mm, "end": v(11.7, -29.3) * mm});
            skArc(sketch, "E1290", {"start": v(11.7, -29.3) * mm, "mid": v(11.63, -29.2) * mm, "end": v(11.62, -29.09) * mm});
            skArc(sketch, "E1291", {"start": v(11.62, -29.09) * mm, "mid": v(11.67, -28.86) * mm, "end": v(11.72, -28.65) * mm});
            skArc(sketch, "E1292", {"start": v(11.72, -28.65) * mm, "mid": v(11.82, -28.37) * mm, "end": v(11.93, -28.1) * mm});
            skArc(sketch, "E1293", {"start": v(11.93, -28.1) * mm, "mid": v(12.07, -27.8) * mm, "end": v(12.23, -27.52) * mm});
            skArc(sketch, "E1294", {"start": v(12.23, -27.52) * mm, "mid": v(12.6, -26.89) * mm, "end": v(12.97, -26.27) * mm});
            skArc(sketch, "E1295", {"start": v(12.97, -26.27) * mm, "mid": v(13.08, -26.2) * mm, "end": v(13.2, -26.24) * mm});
            skArc(sketch, "E1296", {"start": v(13.2, -26.24) * mm, "mid": v(13.27, -26.38) * mm, "end": v(13.26, -26.54) * mm});
            skArc(sketch, "E1297", {"start": v(13.26, -26.54) * mm, "mid": v(12.98, -27.26) * mm, "end": v(12.68, -27.97) * mm});
            skArc(sketch, "E1298", {"start": v(22.46, -32.57) * mm, "mid": v(22.52, -32.9) * mm, "end": v(22.55, -33.25) * mm});
            skArc(sketch, "E1299", {"start": v(22.55, -33.25) * mm, "mid": v(22.53, -33.53) * mm, "end": v(22.46, -33.8) * mm});
            skArc(sketch, "E1300", {"start": v(22.46, -33.8) * mm, "mid": v(22.34, -34.06) * mm, "end": v(22.16, -34.3) * mm});
            skArc(sketch, "E1301", {"start": v(22.16, -34.3) * mm, "mid": v(21.9, -34.57) * mm, "end": v(21.62, -34.82) * mm});
            skArc(sketch, "E1302", {"start": v(21.62, -34.82) * mm, "mid": v(21.02, -35.27) * mm, "end": v(20.4, -35.66) * mm});
            skArc(sketch, "E1303", {"start": v(20.4, -35.66) * mm, "mid": v(20.01, -35.78) * mm, "end": v(19.62, -35.71) * mm});
            skArc(sketch, "E1304", {"start": v(19.62, -35.71) * mm, "mid": v(19.32, -35.48) * mm, "end": v(19.16, -35.14) * mm});
            skArc(sketch, "E1305", {"start": v(19.16, -35.14) * mm, "mid": v(19.06, -34.44) * mm, "end": v(19.02, -33.74) * mm});
            skArc(sketch, "E1306", {"start": v(19.02, -33.74) * mm, "mid": v(19.03, -33.3) * mm, "end": v(19.06, -32.86) * mm});
            skArc(sketch, "E1307", {"start": v(19.06, -32.86) * mm, "mid": v(19.12, -32.37) * mm, "end": v(19.19, -31.88) * mm});
            skArc(sketch, "E1308", {"start": v(19.19, -31.88) * mm, "mid": v(19.27, -31.42) * mm, "end": v(19.37, -30.96) * mm});
            skArc(sketch, "E1309", {"start": v(19.37, -30.96) * mm, "mid": v(19.46, -30.6) * mm, "end": v(19.58, -30.26) * mm});
            skLineSegment(sketch, "E1310", {"start": v(19.58, -30.26) * mm, "end": v(20.13, -28.81) * mm});
            skLineSegment(sketch, "E1311", {"start": v(20.13, -28.81) * mm, "end": v(21.13, -30.03) * mm});
            skArc(sketch, "E1312", {"start": v(21.13, -30.03) * mm, "mid": v(21.34, -30.31) * mm, "end": v(21.54, -30.6) * mm});
            skArc(sketch, "E1313", {"start": v(21.54, -30.6) * mm, "mid": v(21.74, -30.94) * mm, "end": v(21.93, -31.28) * mm});
            skArc(sketch, "E1314", {"start": v(21.93, -31.28) * mm, "mid": v(22.1, -31.63) * mm, "end": v(22.26, -31.98) * mm});
            skArc(sketch, "E1315", {"start": v(22.26, -31.98) * mm, "mid": v(22.37, -32.27) * mm, "end": v(22.46, -32.57) * mm});
            skArc(sketch, "E1316", {"start": v(11.22, -31.53) * mm, "mid": v(11.1, -31.85) * mm, "end": v(10.98, -32.16) * mm});
            skArc(sketch, "E1317", {"start": v(10.98, -32.16) * mm, "mid": v(10.83, -32.53) * mm, "end": v(10.7, -32.9) * mm});
            skArc(sketch, "E1318", {"start": v(10.7, -32.9) * mm, "mid": v(10.55, -33.26) * mm, "end": v(10.4, -33.63) * mm});
            skArc(sketch, "E1319", {"start": v(10.4, -33.63) * mm, "mid": v(10.3, -33.92) * mm, "end": v(10.18, -34.22) * mm});
            skArc(sketch, "E1320", {"start": v(10.18, -34.22) * mm, "mid": v(10.03, -34.58) * mm, "end": v(9.88, -34.93) * mm});
            skArc(sketch, "E1321", {"start": v(9.88, -34.93) * mm, "mid": v(9.8, -35.05) * mm, "end": v(9.68, -35.13) * mm});
            skArc(sketch, "E1322", {"start": v(9.68, -35.13) * mm, "mid": v(9.57, -35.14) * mm, "end": v(9.48, -35.08) * mm});
            skArc(sketch, "E1323", {"start": v(9.48, -35.08) * mm, "mid": v(9.33, -34.88) * mm, "end": v(9.2, -34.67) * mm});
            skArc(sketch, "E1324", {"start": v(9.2, -34.67) * mm, "mid": v(9.1, -34.43) * mm, "end": v(9.06, -34.17) * mm});
            skArc(sketch, "E1325", {"start": v(9.06, -34.17) * mm, "mid": v(9.07, -33.85) * mm, "end": v(9.12, -33.53) * mm});
            skArc(sketch, "E1326", {"start": v(9.12, -33.53) * mm, "mid": v(9.23, -33.13) * mm, "end": v(9.38, -32.74) * mm});
            skArc(sketch, "E1327", {"start": v(9.38, -32.74) * mm, "mid": v(9.62, -32.24) * mm, "end": v(9.87, -31.75) * mm});
            skArc(sketch, "E1328", {"start": v(9.87, -31.75) * mm, "mid": v(10.29, -31.03) * mm, "end": v(10.74, -30.33) * mm});
            skArc(sketch, "E1329", {"start": v(10.74, -30.33) * mm, "mid": v(11, -30.08) * mm, "end": v(11.34, -29.95) * mm});
            skArc(sketch, "E1330", {"start": v(11.34, -29.95) * mm, "mid": v(11.56, -30.02) * mm, "end": v(11.62, -30.24) * mm});
            skArc(sketch, "E1331", {"start": v(11.62, -30.24) * mm, "mid": v(11.44, -30.9) * mm, "end": v(11.22, -31.53) * mm});
            skArc(sketch, "E1332", {"start": v(-40.6, -31.92) * mm, "mid": v(-40.43, -32.3) * mm, "end": v(-40.27, -32.67) * mm});
            skArc(sketch, "E1333", {"start": v(-40.27, -32.67) * mm, "mid": v(-40.12, -33.05) * mm, "end": v(-39.99, -33.43) * mm});
            skArc(sketch, "E1334", {"start": v(-39.99, -33.43) * mm, "mid": v(-39.88, -33.76) * mm, "end": v(-39.79, -34.1) * mm});
            skArc(sketch, "E1335", {"start": v(-39.79, -34.1) * mm, "mid": v(-39.75, -34.3) * mm, "end": v(-39.73, -34.5) * mm});
            skArc(sketch, "E1336", {"start": v(-39.73, -34.5) * mm, "mid": v(-39.77, -34.8) * mm, "end": v(-39.89, -35.1) * mm});
            skArc(sketch, "E1337", {"start": v(-39.89, -35.1) * mm, "mid": v(-40.04, -35.2) * mm, "end": v(-40.23, -35.16) * mm});
            skArc(sketch, "E1338", {"start": v(-40.23, -35.16) * mm, "mid": v(-40.52, -34.88) * mm, "end": v(-40.73, -34.55) * mm});
            skArc(sketch, "E1339", {"start": v(-40.73, -34.55) * mm, "mid": v(-41, -33.94) * mm, "end": v(-41.25, -33.32) * mm});
            skArc(sketch, "E1340", {"start": v(-41.25, -33.32) * mm, "mid": v(-41.39, -32.93) * mm, "end": v(-41.53, -32.53) * mm});
            skArc(sketch, "E1341", {"start": v(-41.53, -32.53) * mm, "mid": v(-41.67, -32.15) * mm, "end": v(-41.8, -31.77) * mm});
            skArc(sketch, "E1342", {"start": v(-41.8, -31.77) * mm, "mid": v(-41.93, -31.44) * mm, "end": v(-42.05, -31.1) * mm});
            skArc(sketch, "E1343", {"start": v(-42.05, -31.1) * mm, "mid": v(-42.11, -30.93) * mm, "end": v(-42.18, -30.74) * mm});
            skArc(sketch, "E1344", {"start": v(-42.18, -30.74) * mm, "mid": v(-42.23, -30.49) * mm, "end": v(-42.18, -30.23) * mm});
            skArc(sketch, "E1345", {"start": v(-42.18, -30.23) * mm, "mid": v(-42.06, -30.12) * mm, "end": v(-41.9, -30.15) * mm});
            skArc(sketch, "E1346", {"start": v(-41.9, -30.15) * mm, "mid": v(-41.53, -30.47) * mm, "end": v(-41.22, -30.85) * mm});
            skArc(sketch, "E1347", {"start": v(-41.22, -30.85) * mm, "mid": v(-40.9, -31.37) * mm, "end": v(-40.6, -31.92) * mm});
            skLineSegment(sketch, "E1348", {"start": v(-36.22, -35.63) * mm, "end": v(-36.38, -37.57) * mm});
            skLineSegment(sketch, "E1349", {"start": v(-36.38, -37.57) * mm, "end": v(-37.29, -35.92) * mm});
            skArc(sketch, "E1350", {"start": v(-37.29, -35.92) * mm, "mid": v(-37.55, -35.4) * mm, "end": v(-37.8, -34.88) * mm});
            skArc(sketch, "E1351", {"start": v(-37.8, -34.88) * mm, "mid": v(-37.9, -34.56) * mm, "end": v(-37.93, -34.23) * mm});
            skArc(sketch, "E1352", {"start": v(-37.93, -34.23) * mm, "mid": v(-37.9, -33.88) * mm, "end": v(-37.8, -33.55) * mm});
            skArc(sketch, "E1353", {"start": v(-37.8, -33.55) * mm, "mid": v(-37.56, -32.95) * mm, "end": v(-37.29, -32.35) * mm});
            skLineSegment(sketch, "E1354", {"start": v(-37.29, -32.35) * mm, "end": v(-36.38, -30.44) * mm});
            skLineSegment(sketch, "E1355", {"start": v(-36.38, -30.44) * mm, "end": v(-36.22, -32.06) * mm});
            skArc(sketch, "E1356", {"start": v(-36.22, -32.06) * mm, "mid": v(-36.2, -32.44) * mm, "end": v(-36.17, -32.82) * mm});
            skArc(sketch, "E1357", {"start": v(-36.17, -32.82) * mm, "mid": v(-36.16, -33.3) * mm, "end": v(-36.16, -33.78) * mm});
            skArc(sketch, "E1358", {"start": v(-36.16, -33.78) * mm, "mid": v(-36.16, -34.27) * mm, "end": v(-36.17, -34.77) * mm});
            skArc(sketch, "E1359", {"start": v(-36.17, -34.77) * mm, "mid": v(-36.2, -35.2) * mm, "end": v(-36.22, -35.63) * mm});
            skArc(sketch, "E1360", {"start": v(16.96, -33.2) * mm, "mid": v(16.94, -33.85) * mm, "end": v(16.88, -34.5) * mm});
            skArc(sketch, "E1361", {"start": v(16.88, -34.5) * mm, "mid": v(16.77, -34.85) * mm, "end": v(16.56, -35.16) * mm});
            skArc(sketch, "E1362", {"start": v(16.56, -35.16) * mm, "mid": v(16.36, -35.24) * mm, "end": v(16.16, -35.15) * mm});
            skArc(sketch, "E1363", {"start": v(16.16, -35.15) * mm, "mid": v(15.92, -34.83) * mm, "end": v(15.74, -34.47) * mm});
            skArc(sketch, "E1364", {"start": v(15.74, -34.47) * mm, "mid": v(15.65, -34.1) * mm, "end": v(15.66, -33.72) * mm});
            skArc(sketch, "E1365", {"start": v(15.66, -33.72) * mm, "mid": v(15.76, -33.1) * mm, "end": v(15.91, -32.51) * mm});
            skArc(sketch, "E1366", {"start": v(15.91, -32.51) * mm, "mid": v(16.1, -31.94) * mm, "end": v(16.3, -31.39) * mm});
            skArc(sketch, "E1367", {"start": v(16.3, -31.39) * mm, "mid": v(16.46, -31.2) * mm, "end": v(16.7, -31.13) * mm});
            skArc(sketch, "E1368", {"start": v(16.7, -31.13) * mm, "mid": v(16.76, -31.15) * mm, "end": v(16.8, -31.22) * mm});
            skArc(sketch, "E1369", {"start": v(16.8, -31.22) * mm, "mid": v(16.84, -31.48) * mm, "end": v(16.88, -31.73) * mm});
            skArc(sketch, "E1370", {"start": v(16.88, -31.73) * mm, "mid": v(16.92, -32.07) * mm, "end": v(16.94, -32.4) * mm});
            skArc(sketch, "E1371", {"start": v(16.94, -32.4) * mm, "mid": v(16.96, -32.8) * mm, "end": v(16.96, -33.2) * mm});
            skArc(sketch, "E1372", {"start": v(6.8, -35.5) * mm, "mid": v(6.4, -36.27) * mm, "end": v(6, -37.04) * mm});
            skArc(sketch, "E1373", {"start": v(6, -37.04) * mm, "mid": v(5.93, -37.1) * mm, "end": v(5.82, -37.09) * mm});
            skArc(sketch, "E1374", {"start": v(5.82, -37.09) * mm, "mid": v(5.74, -37) * mm, "end": v(5.71, -36.88) * mm});
            skArc(sketch, "E1375", {"start": v(5.71, -36.88) * mm, "mid": v(5.77, -35.9) * mm, "end": v(5.84, -34.93) * mm});
            skArc(sketch, "E1376", {"start": v(5.84, -34.93) * mm, "mid": v(5.92, -33.82) * mm, "end": v(6, -32.7) * mm});
            skArc(sketch, "E1377", {"start": v(6, -32.7) * mm, "mid": v(6.04, -32.5) * mm, "end": v(6.12, -32.3) * mm});
            skArc(sketch, "E1378", {"start": v(6.12, -32.3) * mm, "mid": v(6.21, -32.23) * mm, "end": v(6.32, -32.28) * mm});
            skArc(sketch, "E1379", {"start": v(6.32, -32.28) * mm, "mid": v(6.6, -32.6) * mm, "end": v(6.86, -32.95) * mm});
            skArc(sketch, "E1380", {"start": v(6.86, -32.95) * mm, "mid": v(7.05, -33.24) * mm, "end": v(7.22, -33.55) * mm});
            skArc(sketch, "E1381", {"start": v(7.22, -33.55) * mm, "mid": v(7.3, -33.8) * mm, "end": v(7.32, -34.04) * mm});
            skArc(sketch, "E1382", {"start": v(7.32, -34.04) * mm, "mid": v(7.29, -34.33) * mm, "end": v(7.2, -34.61) * mm});
            skArc(sketch, "E1383", {"start": v(7.2, -34.61) * mm, "mid": v(7, -35.06) * mm, "end": v(6.8, -35.5) * mm});
            skArc(sketch, "E1384", {"start": v(-33.25, -38.22) * mm, "mid": v(-33.3, -38.25) * mm, "end": v(-33.36, -38.26) * mm});
            skArc(sketch, "E1385", {"start": v(-33.36, -38.26) * mm, "mid": v(-33.48, -38.25) * mm, "end": v(-33.6, -38.23) * mm});
            skArc(sketch, "E1386", {"start": v(-33.6, -38.23) * mm, "mid": v(-33.76, -38.2) * mm, "end": v(-33.91, -38.16) * mm});
            skArc(sketch, "E1387", {"start": v(-33.91, -38.16) * mm, "mid": v(-34.08, -38.1) * mm, "end": v(-34.25, -38.04) * mm});
            skArc(sketch, "E1388", {"start": v(-34.25, -38.04) * mm, "mid": v(-34.47, -37.92) * mm, "end": v(-34.65, -37.74) * mm});
            skArc(sketch, "E1389", {"start": v(-34.65, -37.74) * mm, "mid": v(-34.8, -37.49) * mm, "end": v(-34.9, -37.21) * mm});
            skArc(sketch, "E1390", {"start": v(-34.9, -37.21) * mm, "mid": v(-35, -36.8) * mm, "end": v(-35.04, -36.38) * mm});
            skArc(sketch, "E1391", {"start": v(-35.04, -36.38) * mm, "mid": v(-35.07, -35.72) * mm, "end": v(-35.08, -35.07) * mm});
            skLineSegment(sketch, "E1392", {"start": v(-35.08, -35.07) * mm, "end": v(-35.06, -32.42) * mm});
            skLineSegment(sketch, "E1393", {"start": v(-35.06, -32.42) * mm, "end": v(-34.08, -35.25) * mm});
            skArc(sketch, "E1394", {"start": v(-34.08, -35.25) * mm, "mid": v(-33.9, -35.8) * mm, "end": v(-33.72, -36.34) * mm});
            skArc(sketch, "E1395", {"start": v(-33.72, -36.34) * mm, "mid": v(-33.57, -36.81) * mm, "end": v(-33.44, -37.29) * mm});
            skArc(sketch, "E1396", {"start": v(-33.44, -37.29) * mm, "mid": v(-33.33, -37.7) * mm, "end": v(-33.22, -38.1) * mm});
            skArc(sketch, "E1397", {"start": v(-33.22, -38.1) * mm, "mid": v(-33.22, -38.16) * mm, "end": v(-33.25, -38.22) * mm});
            skLineSegment(sketch, "E1398.bottom", {"start": v(-128.9, 63.55) * mm, "end": v(72.38, 63.55) * mm});
            skLineSegment(sketch, "E1398.top", {"start": v(-128.9, -66.45) * mm, "end": v(72.38, -66.45) * mm});
            skLineSegment(sketch, "E1398.left", {"start": v(-128.9, 63.55) * mm, "end": v(-128.9, -66.45) * mm});
            skLineSegment(sketch, "E1398.right", {"start": v(72.38, 63.55) * mm, "end": v(72.38, -66.45) * mm});
            skSolve(sketch);
        }
        {
            var Q0;
            Q0=makeQuery(id+"F0.imprint","IMPRINT",FACE,{"disambiguationData":[TD([[makeQuery(id+"F0.imprint","IMPRINT",EDGE,{"derivedFrom":sQuery(id+"F0.wireOp",EDGE,"E0")}),1.0]])]});
            extrude(context, id + "F1", {"entities" : qUnion([Q0]), "depth" : 40 * mm});
        }
    });
